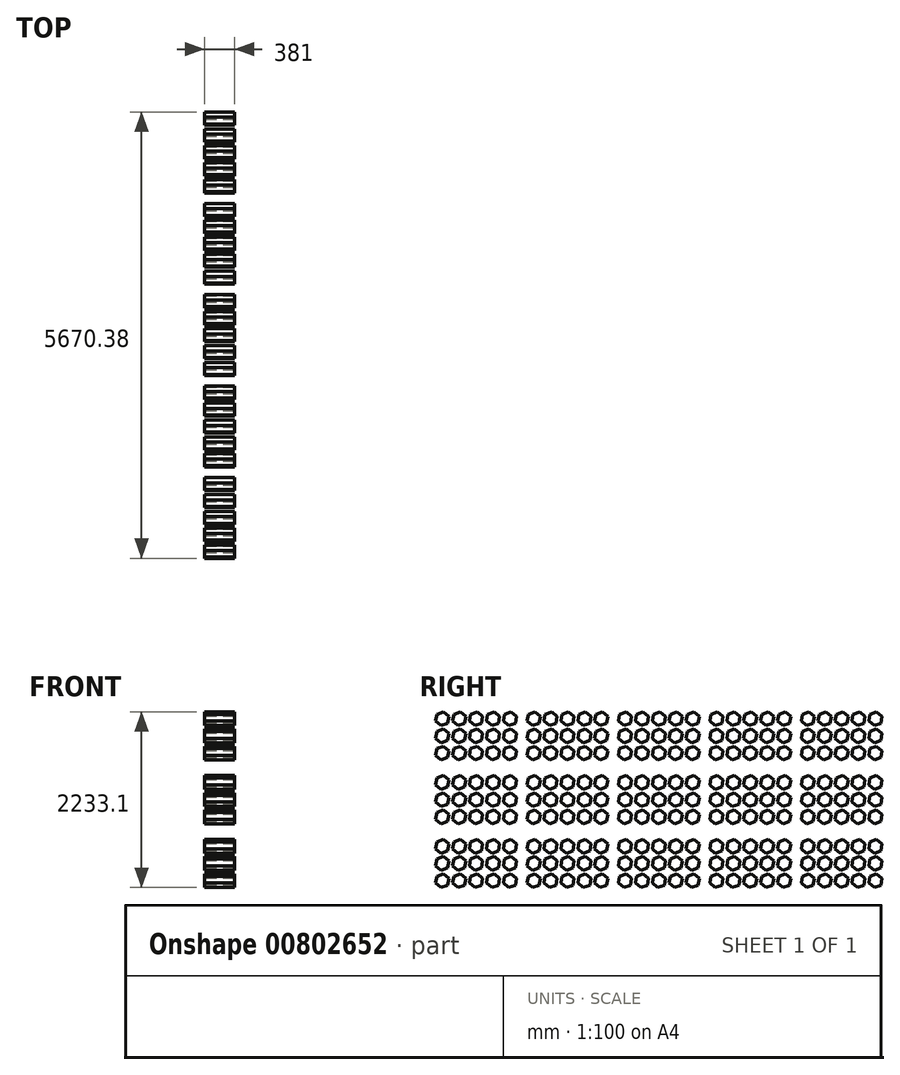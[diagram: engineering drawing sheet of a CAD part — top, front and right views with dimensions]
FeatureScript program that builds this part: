
annotation { "Feature Type Name" : "Feature", "Feature Type Description" : "" }
export const myFeature = defineFeature(function(context is Context, id is Id, definition is map)
    precondition{}
    {
        {
            var Q0;
            Q0=qCreatedBy(makeId("Right.planeOp"),FACE);
            var sketch = newSketch(context, id + "F0", { "sketchPlane" : qUnion([Q0])});
            skCircle(sketch, "E0.cCircle", {"center": v(0, 0) * mm, "radius": 77.26 * mm, "construction": true});
            skLineSegment(sketch, "E0.0", {"start": v(68.3, -57.4) * mm, "end": v(-15.56, -87.85) * mm});
            skLineSegment(sketch, "E0.1", {"start": v(-15.56, -87.85) * mm, "end": v(-83.86, -30.45) * mm});
            skLineSegment(sketch, "E0.2", {"start": v(-83.86, -30.45) * mm, "end": v(-68.3, 57.4) * mm});
            skLineSegment(sketch, "E0.3", {"start": v(-68.3, 57.4) * mm, "end": v(15.56, 87.85) * mm});
            skLineSegment(sketch, "E0.4", {"start": v(15.56, 87.85) * mm, "end": v(83.86, 30.45) * mm});
            skLineSegment(sketch, "E0.5", {"start": v(83.86, 30.45) * mm, "end": v(68.3, -57.4) * mm});
            skPoint(sketch, "E0.0.midPoint", {"position": v(26.37, -72.63) * mm});
            skCircle(sketch, "E1.0.1.0", {"center": v(0, 218.44) * mm, "radius": 77.26 * mm, "construction": true});
            skLineSegment(sketch, "E1.0.1.1", {"start": v(68.3, 161.04) * mm, "end": v(-15.56, 130.59) * mm});
            skLineSegment(sketch, "E1.0.1.2", {"start": v(-15.56, 130.59) * mm, "end": v(-83.86, 188) * mm});
            skLineSegment(sketch, "E1.0.1.3", {"start": v(-83.86, 188) * mm, "end": v(-68.3, 275.84) * mm});
            skLineSegment(sketch, "E1.0.1.4", {"start": v(-68.3, 275.84) * mm, "end": v(15.56, 306.3) * mm});
            skLineSegment(sketch, "E1.0.1.5", {"start": v(15.56, 306.3) * mm, "end": v(83.86, 248.89) * mm});
            skLineSegment(sketch, "E1.0.1.6", {"start": v(83.86, 248.89) * mm, "end": v(68.3, 161.04) * mm});
            skPoint(sketch, "E1.0.1.7", {"position": v(26.37, 145.81) * mm});
            skCircle(sketch, "E1.0.2.0", {"center": v(0, 436.88) * mm, "radius": 77.26 * mm, "construction": true});
            skLineSegment(sketch, "E1.0.2.1", {"start": v(68.3, 379.48) * mm, "end": v(-15.56, 349.03) * mm});
            skLineSegment(sketch, "E1.0.2.2", {"start": v(-15.56, 349.03) * mm, "end": v(-83.86, 406.43) * mm});
            skLineSegment(sketch, "E1.0.2.3", {"start": v(-83.86, 406.43) * mm, "end": v(-68.3, 494.28) * mm});
            skLineSegment(sketch, "E1.0.2.4", {"start": v(-68.3, 494.28) * mm, "end": v(15.56, 524.73) * mm});
            skLineSegment(sketch, "E1.0.2.5", {"start": v(15.56, 524.73) * mm, "end": v(83.86, 467.33) * mm});
            skLineSegment(sketch, "E1.0.2.6", {"start": v(83.86, 467.33) * mm, "end": v(68.3, 379.48) * mm});
            skPoint(sketch, "E1.0.2.7", {"position": v(26.37, 364.25) * mm});
            skCircle(sketch, "E1.1.0.0", {"center": v(214.88, 0) * mm, "radius": 77.26 * mm, "construction": true});
            skLineSegment(sketch, "E1.1.0.1", {"start": v(283.18, -57.4) * mm, "end": v(199.32, -87.85) * mm});
            skLineSegment(sketch, "E1.1.0.2", {"start": v(199.32, -87.85) * mm, "end": v(131.02, -30.45) * mm});
            skLineSegment(sketch, "E1.1.0.3", {"start": v(131.02, -30.45) * mm, "end": v(146.58, 57.4) * mm});
            skLineSegment(sketch, "E1.1.0.4", {"start": v(146.58, 57.4) * mm, "end": v(230.44, 87.85) * mm});
            skLineSegment(sketch, "E1.1.0.5", {"start": v(230.44, 87.85) * mm, "end": v(298.74, 30.45) * mm});
            skLineSegment(sketch, "E1.1.0.6", {"start": v(298.74, 30.45) * mm, "end": v(283.18, -57.4) * mm});
            skPoint(sketch, "E1.1.0.7", {"position": v(241.25, -72.63) * mm});
            skCircle(sketch, "E1.1.1.0", {"center": v(214.88, 218.44) * mm, "radius": 77.26 * mm, "construction": true});
            skLineSegment(sketch, "E1.1.1.1", {"start": v(283.18, 161.04) * mm, "end": v(199.32, 130.59) * mm});
            skLineSegment(sketch, "E1.1.1.2", {"start": v(199.32, 130.59) * mm, "end": v(131.02, 188) * mm});
            skLineSegment(sketch, "E1.1.1.3", {"start": v(131.02, 188) * mm, "end": v(146.58, 275.84) * mm});
            skLineSegment(sketch, "E1.1.1.4", {"start": v(146.58, 275.84) * mm, "end": v(230.44, 306.3) * mm});
            skLineSegment(sketch, "E1.1.1.5", {"start": v(230.44, 306.3) * mm, "end": v(298.74, 248.89) * mm});
            skLineSegment(sketch, "E1.1.1.6", {"start": v(298.74, 248.89) * mm, "end": v(283.18, 161.04) * mm});
            skPoint(sketch, "E1.1.1.7", {"position": v(241.25, 145.81) * mm});
            skCircle(sketch, "E1.1.2.0", {"center": v(214.88, 436.88) * mm, "radius": 77.26 * mm, "construction": true});
            skLineSegment(sketch, "E1.1.2.1", {"start": v(283.18, 379.48) * mm, "end": v(199.32, 349.03) * mm});
            skLineSegment(sketch, "E1.1.2.2", {"start": v(199.32, 349.03) * mm, "end": v(131.02, 406.43) * mm});
            skLineSegment(sketch, "E1.1.2.3", {"start": v(131.02, 406.43) * mm, "end": v(146.58, 494.28) * mm});
            skLineSegment(sketch, "E1.1.2.4", {"start": v(146.58, 494.28) * mm, "end": v(230.44, 524.73) * mm});
            skLineSegment(sketch, "E1.1.2.5", {"start": v(230.44, 524.73) * mm, "end": v(298.74, 467.33) * mm});
            skLineSegment(sketch, "E1.1.2.6", {"start": v(298.74, 467.33) * mm, "end": v(283.18, 379.48) * mm});
            skPoint(sketch, "E1.1.2.7", {"position": v(241.25, 364.25) * mm});
            skCircle(sketch, "E1.2.0.0", {"center": v(429.77, 0) * mm, "radius": 77.26 * mm, "construction": true});
            skLineSegment(sketch, "E1.2.0.1", {"start": v(498.07, -57.4) * mm, "end": v(414.2, -87.85) * mm});
            skLineSegment(sketch, "E1.2.0.2", {"start": v(414.2, -87.85) * mm, "end": v(345.9, -30.45) * mm});
            skLineSegment(sketch, "E1.2.0.3", {"start": v(345.9, -30.45) * mm, "end": v(361.47, 57.4) * mm});
            skLineSegment(sketch, "E1.2.0.4", {"start": v(361.47, 57.4) * mm, "end": v(445.33, 87.85) * mm});
            skLineSegment(sketch, "E1.2.0.5", {"start": v(445.33, 87.85) * mm, "end": v(513.63, 30.45) * mm});
            skLineSegment(sketch, "E1.2.0.6", {"start": v(513.63, 30.45) * mm, "end": v(498.07, -57.4) * mm});
            skPoint(sketch, "E1.2.0.7", {"position": v(456.14, -72.63) * mm});
            skCircle(sketch, "E1.2.1.0", {"center": v(429.77, 218.44) * mm, "radius": 77.26 * mm, "construction": true});
            skLineSegment(sketch, "E1.2.1.1", {"start": v(498.07, 161.04) * mm, "end": v(414.2, 130.59) * mm});
            skLineSegment(sketch, "E1.2.1.2", {"start": v(414.2, 130.59) * mm, "end": v(345.9, 188) * mm});
            skLineSegment(sketch, "E1.2.1.3", {"start": v(345.9, 188) * mm, "end": v(361.47, 275.84) * mm});
            skLineSegment(sketch, "E1.2.1.4", {"start": v(361.47, 275.84) * mm, "end": v(445.33, 306.3) * mm});
            skLineSegment(sketch, "E1.2.1.5", {"start": v(445.33, 306.3) * mm, "end": v(513.63, 248.89) * mm});
            skLineSegment(sketch, "E1.2.1.6", {"start": v(513.63, 248.89) * mm, "end": v(498.07, 161.04) * mm});
            skPoint(sketch, "E1.2.1.7", {"position": v(456.14, 145.81) * mm});
            skCircle(sketch, "E1.2.2.0", {"center": v(429.77, 436.88) * mm, "radius": 77.26 * mm, "construction": true});
            skLineSegment(sketch, "E1.2.2.1", {"start": v(498.07, 379.48) * mm, "end": v(414.2, 349.03) * mm});
            skLineSegment(sketch, "E1.2.2.2", {"start": v(414.2, 349.03) * mm, "end": v(345.9, 406.43) * mm});
            skLineSegment(sketch, "E1.2.2.3", {"start": v(345.9, 406.43) * mm, "end": v(361.47, 494.28) * mm});
            skLineSegment(sketch, "E1.2.2.4", {"start": v(361.47, 494.28) * mm, "end": v(445.33, 524.73) * mm});
            skLineSegment(sketch, "E1.2.2.5", {"start": v(445.33, 524.73) * mm, "end": v(513.63, 467.33) * mm});
            skLineSegment(sketch, "E1.2.2.6", {"start": v(513.63, 467.33) * mm, "end": v(498.07, 379.48) * mm});
            skPoint(sketch, "E1.2.2.7", {"position": v(456.14, 364.25) * mm});
            skCircle(sketch, "E1.3.0.0", {"center": v(644.65, 0) * mm, "radius": 77.26 * mm, "construction": true});
            skLineSegment(sketch, "E1.3.0.1", {"start": v(712.95, -57.4) * mm, "end": v(629.1, -87.85) * mm});
            skLineSegment(sketch, "E1.3.0.2", {"start": v(629.1, -87.85) * mm, "end": v(560.8, -30.45) * mm});
            skLineSegment(sketch, "E1.3.0.3", {"start": v(560.8, -30.45) * mm, "end": v(576.35, 57.4) * mm});
            skLineSegment(sketch, "E1.3.0.4", {"start": v(576.35, 57.4) * mm, "end": v(660.21, 87.85) * mm});
            skLineSegment(sketch, "E1.3.0.5", {"start": v(660.21, 87.85) * mm, "end": v(728.51, 30.45) * mm});
            skLineSegment(sketch, "E1.3.0.6", {"start": v(728.51, 30.45) * mm, "end": v(712.95, -57.4) * mm});
            skPoint(sketch, "E1.3.0.7", {"position": v(671.02, -72.63) * mm});
            skCircle(sketch, "E1.3.1.0", {"center": v(644.65, 218.44) * mm, "radius": 77.26 * mm, "construction": true});
            skLineSegment(sketch, "E1.3.1.1", {"start": v(712.95, 161.04) * mm, "end": v(629.1, 130.59) * mm});
            skLineSegment(sketch, "E1.3.1.2", {"start": v(629.1, 130.59) * mm, "end": v(560.8, 188) * mm});
            skLineSegment(sketch, "E1.3.1.3", {"start": v(560.8, 188) * mm, "end": v(576.35, 275.84) * mm});
            skLineSegment(sketch, "E1.3.1.4", {"start": v(576.35, 275.84) * mm, "end": v(660.21, 306.3) * mm});
            skLineSegment(sketch, "E1.3.1.5", {"start": v(660.21, 306.3) * mm, "end": v(728.51, 248.89) * mm});
            skLineSegment(sketch, "E1.3.1.6", {"start": v(728.51, 248.89) * mm, "end": v(712.95, 161.04) * mm});
            skPoint(sketch, "E1.3.1.7", {"position": v(671.02, 145.81) * mm});
            skCircle(sketch, "E1.3.2.0", {"center": v(644.65, 436.88) * mm, "radius": 77.26 * mm, "construction": true});
            skLineSegment(sketch, "E1.3.2.1", {"start": v(712.95, 379.48) * mm, "end": v(629.1, 349.03) * mm});
            skLineSegment(sketch, "E1.3.2.2", {"start": v(629.1, 349.03) * mm, "end": v(560.8, 406.43) * mm});
            skLineSegment(sketch, "E1.3.2.3", {"start": v(560.8, 406.43) * mm, "end": v(576.35, 494.28) * mm});
            skLineSegment(sketch, "E1.3.2.4", {"start": v(576.35, 494.28) * mm, "end": v(660.21, 524.73) * mm});
            skLineSegment(sketch, "E1.3.2.5", {"start": v(660.21, 524.73) * mm, "end": v(728.51, 467.33) * mm});
            skLineSegment(sketch, "E1.3.2.6", {"start": v(728.51, 467.33) * mm, "end": v(712.95, 379.48) * mm});
            skPoint(sketch, "E1.3.2.7", {"position": v(671.02, 364.25) * mm});
            skCircle(sketch, "E1.4.0.0", {"center": v(859.54, 0) * mm, "radius": 77.26 * mm, "construction": true});
            skLineSegment(sketch, "E1.4.0.1", {"start": v(927.84, -57.4) * mm, "end": v(843.98, -87.85) * mm});
            skLineSegment(sketch, "E1.4.0.2", {"start": v(843.98, -87.85) * mm, "end": v(775.68, -30.45) * mm});
            skLineSegment(sketch, "E1.4.0.3", {"start": v(775.68, -30.45) * mm, "end": v(791.24, 57.4) * mm});
            skLineSegment(sketch, "E1.4.0.4", {"start": v(791.24, 57.4) * mm, "end": v(875.1, 87.85) * mm});
            skLineSegment(sketch, "E1.4.0.5", {"start": v(875.1, 87.85) * mm, "end": v(943.4, 30.45) * mm});
            skLineSegment(sketch, "E1.4.0.6", {"start": v(943.4, 30.45) * mm, "end": v(927.84, -57.4) * mm});
            skPoint(sketch, "E1.4.0.7", {"position": v(885.9, -72.63) * mm});
            skCircle(sketch, "E1.4.1.0", {"center": v(859.54, 218.44) * mm, "radius": 77.26 * mm, "construction": true});
            skLineSegment(sketch, "E1.4.1.1", {"start": v(927.84, 161.04) * mm, "end": v(843.98, 130.59) * mm});
            skLineSegment(sketch, "E1.4.1.2", {"start": v(843.98, 130.59) * mm, "end": v(775.68, 188) * mm});
            skLineSegment(sketch, "E1.4.1.3", {"start": v(775.68, 188) * mm, "end": v(791.24, 275.84) * mm});
            skLineSegment(sketch, "E1.4.1.4", {"start": v(791.24, 275.84) * mm, "end": v(875.1, 306.3) * mm});
            skLineSegment(sketch, "E1.4.1.5", {"start": v(875.1, 306.3) * mm, "end": v(943.4, 248.89) * mm});
            skLineSegment(sketch, "E1.4.1.6", {"start": v(943.4, 248.89) * mm, "end": v(927.84, 161.04) * mm});
            skPoint(sketch, "E1.4.1.7", {"position": v(885.9, 145.81) * mm});
            skCircle(sketch, "E1.4.2.0", {"center": v(859.54, 436.88) * mm, "radius": 77.26 * mm, "construction": true});
            skLineSegment(sketch, "E1.4.2.1", {"start": v(927.84, 379.48) * mm, "end": v(843.98, 349.03) * mm});
            skLineSegment(sketch, "E1.4.2.2", {"start": v(843.98, 349.03) * mm, "end": v(775.68, 406.43) * mm});
            skLineSegment(sketch, "E1.4.2.3", {"start": v(775.68, 406.43) * mm, "end": v(791.24, 494.28) * mm});
            skLineSegment(sketch, "E1.4.2.4", {"start": v(791.24, 494.28) * mm, "end": v(875.1, 524.73) * mm});
            skLineSegment(sketch, "E1.4.2.5", {"start": v(875.1, 524.73) * mm, "end": v(943.4, 467.33) * mm});
            skLineSegment(sketch, "E1.4.2.6", {"start": v(943.4, 467.33) * mm, "end": v(927.84, 379.48) * mm});
            skPoint(sketch, "E1.4.2.7", {"position": v(885.9, 364.25) * mm});
            skLineSegment(sketch, "E1.direction1", {"start": v(-83.86, -30.45) * mm, "end": v(131.02, -30.45) * mm, "construction": true});
            skLineSegment(sketch, "E1.direction2", {"start": v(-83.86, -30.45) * mm, "end": v(-83.86, 188) * mm, "construction": true});
            skLineSegment(sketch, "E2.0.1.0", {"start": v(943.4, 840.7) * mm, "end": v(927.84, 752.86) * mm});
            skLineSegment(sketch, "E2.0.1.1", {"start": v(-83.86, 779.81) * mm, "end": v(-83.86, 998.25) * mm, "construction": true});
            skLineSegment(sketch, "E2.0.1.2", {"start": v(230.44, 898.11) * mm, "end": v(298.74, 840.7) * mm});
            skCircle(sketch, "E2.0.1.3", {"center": v(429.77, 810.26) * mm, "radius": 77.26 * mm, "construction": true});
            skLineSegment(sketch, "E2.0.1.4", {"start": v(414.2, 1159.29) * mm, "end": v(345.9, 1216.7) * mm});
            skPoint(sketch, "E2.0.1.5", {"position": v(885.9, 956.07) * mm});
            skPoint(sketch, "E2.0.1.6", {"position": v(241.25, 1174.51) * mm});
            skLineSegment(sketch, "E2.0.1.7", {"start": v(15.56, 1335) * mm, "end": v(83.86, 1277.59) * mm});
            skLineSegment(sketch, "E2.0.1.8", {"start": v(576.35, 867.66) * mm, "end": v(660.21, 898.11) * mm});
            skLineSegment(sketch, "E2.0.1.9", {"start": v(414.2, 940.85) * mm, "end": v(345.9, 998.25) * mm});
            skCircle(sketch, "E2.0.1.10", {"center": v(214.88, 1247.14) * mm, "radius": 77.26 * mm, "construction": true});
            skPoint(sketch, "E2.0.1.11", {"position": v(26.37, 1174.51) * mm});
            skPoint(sketch, "E2.0.1.12", {"position": v(671.02, 956.07) * mm});
            skCircle(sketch, "E2.0.1.13", {"center": v(859.54, 1028.7) * mm, "radius": 77.26 * mm, "construction": true});
            skLineSegment(sketch, "E2.0.1.14", {"start": v(83.86, 1277.59) * mm, "end": v(68.3, 1189.74) * mm});
            skCircle(sketch, "E2.0.1.15", {"center": v(644.65, 1247.14) * mm, "radius": 77.26 * mm, "construction": true});
            skCircle(sketch, "E2.0.1.16", {"center": v(859.54, 810.26) * mm, "radius": 77.26 * mm, "construction": true});
            skLineSegment(sketch, "E2.0.1.17", {"start": v(445.33, 1335) * mm, "end": v(513.63, 1277.59) * mm});
            skLineSegment(sketch, "E2.0.1.18", {"start": v(345.9, 779.81) * mm, "end": v(361.47, 867.66) * mm});
            skLineSegment(sketch, "E2.0.1.19", {"start": v(345.9, 998.25) * mm, "end": v(361.47, 1086.1) * mm});
            skPoint(sketch, "E2.0.1.20", {"position": v(671.02, 737.63) * mm});
            skPoint(sketch, "E2.0.1.21", {"position": v(26.37, 956.07) * mm});
            skPoint(sketch, "E2.0.1.22", {"position": v(456.14, 737.63) * mm});
            skPoint(sketch, "E2.0.1.23", {"position": v(885.9, 1174.51) * mm});
            skLineSegment(sketch, "E2.0.1.24", {"start": v(361.47, 1304.54) * mm, "end": v(445.33, 1335) * mm});
            skLineSegment(sketch, "E2.0.1.25", {"start": v(414.2, 722.4) * mm, "end": v(345.9, 779.81) * mm});
            skCircle(sketch, "E2.0.1.26", {"center": v(214.88, 1028.7) * mm, "radius": 77.26 * mm, "construction": true});
            skCircle(sketch, "E2.0.1.27", {"center": v(214.88, 810.26) * mm, "radius": 77.26 * mm, "construction": true});
            skLineSegment(sketch, "E2.0.1.28", {"start": v(513.63, 1277.59) * mm, "end": v(498.07, 1189.74) * mm});
            skLineSegment(sketch, "E2.0.1.29", {"start": v(361.47, 1086.1) * mm, "end": v(445.33, 1116.55) * mm});
            skLineSegment(sketch, "E2.0.1.30", {"start": v(361.47, 867.66) * mm, "end": v(445.33, 898.11) * mm});
            skLineSegment(sketch, "E2.0.1.31", {"start": v(199.32, 940.85) * mm, "end": v(131.02, 998.25) * mm});
            skLineSegment(sketch, "E2.0.1.32", {"start": v(775.68, 998.25) * mm, "end": v(791.24, 1086.1) * mm});
            skPoint(sketch, "E2.0.1.33", {"position": v(241.25, 737.63) * mm});
            skPoint(sketch, "E2.0.1.34", {"position": v(671.02, 1174.51) * mm});
            skLineSegment(sketch, "E2.0.1.35", {"start": v(629.1, 1159.29) * mm, "end": v(560.8, 1216.7) * mm});
            skCircle(sketch, "E2.0.1.36", {"center": v(644.65, 1028.7) * mm, "radius": 77.26 * mm, "construction": true});
            skCircle(sketch, "E2.0.1.37", {"center": v(644.65, 810.26) * mm, "radius": 77.26 * mm, "construction": true});
            skLineSegment(sketch, "E2.0.1.38", {"start": v(445.33, 898.11) * mm, "end": v(513.63, 840.7) * mm});
            skLineSegment(sketch, "E2.0.1.39", {"start": v(791.24, 1304.54) * mm, "end": v(875.1, 1335) * mm});
            skLineSegment(sketch, "E2.0.1.40", {"start": v(791.24, 1086.1) * mm, "end": v(875.1, 1116.55) * mm});
            skLineSegment(sketch, "E2.0.1.41", {"start": v(83.86, 1059.15) * mm, "end": v(68.3, 971.3) * mm});
            skCircle(sketch, "E2.0.1.42", {"center": v(0, 1247.14) * mm, "radius": 77.26 * mm, "construction": true});
            skCircle(sketch, "E2.0.1.43", {"center": v(0, 810.26) * mm, "radius": 77.26 * mm, "construction": true});
            skLineSegment(sketch, "E2.0.1.44", {"start": v(-15.56, 722.4) * mm, "end": v(-83.86, 779.81) * mm});
            skLineSegment(sketch, "E2.0.1.45", {"start": v(-68.3, 867.66) * mm, "end": v(15.56, 898.11) * mm});
            skCircle(sketch, "E2.0.1.46", {"center": v(0, 1028.7) * mm, "radius": 77.26 * mm, "construction": true});
            skLineSegment(sketch, "E2.0.1.47", {"start": v(-15.56, 940.85) * mm, "end": v(-83.86, 998.25) * mm});
            skLineSegment(sketch, "E2.0.1.48", {"start": v(-83.86, 998.25) * mm, "end": v(-68.3, 1086.1) * mm});
            skLineSegment(sketch, "E2.0.1.49", {"start": v(-68.3, 1086.1) * mm, "end": v(15.56, 1116.55) * mm});
            skLineSegment(sketch, "E2.0.1.50", {"start": v(15.56, 1116.55) * mm, "end": v(83.86, 1059.15) * mm});
            skPoint(sketch, "E2.0.1.51", {"position": v(456.14, 956.07) * mm});
            skLineSegment(sketch, "E2.0.1.52", {"start": v(513.63, 1059.15) * mm, "end": v(498.07, 971.3) * mm});
            skLineSegment(sketch, "E2.0.1.53", {"start": v(146.58, 1304.54) * mm, "end": v(230.44, 1335) * mm});
            skLineSegment(sketch, "E2.0.1.54", {"start": v(875.1, 1335) * mm, "end": v(943.4, 1277.59) * mm});
            skLineSegment(sketch, "E2.0.1.55", {"start": v(-15.56, 1159.29) * mm, "end": v(-83.86, 1216.7) * mm});
            skLineSegment(sketch, "E2.0.1.56", {"start": v(513.63, 840.7) * mm, "end": v(498.07, 752.86) * mm});
            skCircle(sketch, "E2.0.1.57", {"center": v(429.77, 1247.14) * mm, "radius": 77.26 * mm, "construction": true});
            skLineSegment(sketch, "E2.0.1.58", {"start": v(943.4, 1277.59) * mm, "end": v(927.84, 1189.74) * mm});
            skLineSegment(sketch, "E2.0.1.59", {"start": v(629.1, 940.85) * mm, "end": v(560.8, 998.25) * mm});
            skPoint(sketch, "E2.0.1.60", {"position": v(241.25, 956.07) * mm});
            skPoint(sketch, "E2.0.1.61", {"position": v(885.9, 737.63) * mm});
            skLineSegment(sketch, "E2.0.1.62", {"start": v(576.35, 1304.54) * mm, "end": v(660.21, 1335) * mm});
            skCircle(sketch, "E2.0.1.63", {"center": v(429.77, 1028.7) * mm, "radius": 77.26 * mm, "construction": true});
            skLineSegment(sketch, "E2.0.1.64", {"start": v(943.4, 1059.15) * mm, "end": v(927.84, 971.3) * mm});
            skLineSegment(sketch, "E2.0.1.65", {"start": v(146.58, 867.66) * mm, "end": v(230.44, 898.11) * mm});
            skLineSegment(sketch, "E2.0.1.66", {"start": v(-83.86, 779.81) * mm, "end": v(131.02, 779.81) * mm, "construction": true});
            skLineSegment(sketch, "E2.0.1.67", {"start": v(875.1, 898.11) * mm, "end": v(943.4, 840.7) * mm});
            skLineSegment(sketch, "E2.0.1.68", {"start": v(-68.3, 1304.54) * mm, "end": v(15.56, 1335) * mm});
            skLineSegment(sketch, "E2.0.1.69", {"start": v(660.21, 1335) * mm, "end": v(728.51, 1277.59) * mm});
            skCircle(sketch, "E2.0.1.70", {"center": v(859.54, 1247.14) * mm, "radius": 77.26 * mm, "construction": true});
            skPoint(sketch, "E2.0.1.71", {"position": v(456.14, 1174.51) * mm});
            skPoint(sketch, "E2.0.1.72", {"position": v(26.37, 737.63) * mm});
            skLineSegment(sketch, "E2.0.1.73", {"start": v(576.35, 1086.1) * mm, "end": v(660.21, 1116.55) * mm});
            skLineSegment(sketch, "E2.0.1.74", {"start": v(728.51, 1277.59) * mm, "end": v(712.95, 1189.74) * mm});
            skLineSegment(sketch, "E2.0.1.75", {"start": v(927.84, 1189.74) * mm, "end": v(843.98, 1159.29) * mm});
            skLineSegment(sketch, "E2.0.1.76", {"start": v(345.9, 1216.7) * mm, "end": v(361.47, 1304.54) * mm});
            skLineSegment(sketch, "E2.0.1.77", {"start": v(498.07, 752.86) * mm, "end": v(414.2, 722.4) * mm});
            skLineSegment(sketch, "E2.0.1.78", {"start": v(298.74, 840.7) * mm, "end": v(283.18, 752.86) * mm});
            skLineSegment(sketch, "E2.0.1.79", {"start": v(660.21, 1116.55) * mm, "end": v(728.51, 1059.15) * mm});
            skLineSegment(sketch, "E2.0.1.80", {"start": v(660.21, 898.11) * mm, "end": v(728.51, 840.7) * mm});
            skLineSegment(sketch, "E2.0.1.81", {"start": v(283.18, 1189.74) * mm, "end": v(199.32, 1159.29) * mm});
            skLineSegment(sketch, "E2.0.1.82", {"start": v(283.18, 971.3) * mm, "end": v(199.32, 940.85) * mm});
            skLineSegment(sketch, "E2.0.1.83", {"start": v(843.98, 1159.29) * mm, "end": v(775.68, 1216.7) * mm});
            skLineSegment(sketch, "E2.0.1.84", {"start": v(843.98, 940.85) * mm, "end": v(775.68, 998.25) * mm});
            skLineSegment(sketch, "E2.0.1.85", {"start": v(927.84, 971.3) * mm, "end": v(843.98, 940.85) * mm});
            skLineSegment(sketch, "E2.0.1.86", {"start": v(728.51, 1059.15) * mm, "end": v(712.95, 971.3) * mm});
            skLineSegment(sketch, "E2.0.1.87", {"start": v(712.95, 1189.74) * mm, "end": v(629.1, 1159.29) * mm});
            skLineSegment(sketch, "E2.0.1.88", {"start": v(927.84, 752.86) * mm, "end": v(843.98, 722.4) * mm});
            skLineSegment(sketch, "E2.0.1.89", {"start": v(728.51, 840.7) * mm, "end": v(712.95, 752.86) * mm});
            skLineSegment(sketch, "E2.0.1.90", {"start": v(199.32, 1159.29) * mm, "end": v(131.02, 1216.7) * mm});
            skLineSegment(sketch, "E2.0.1.91", {"start": v(775.68, 1216.7) * mm, "end": v(791.24, 1304.54) * mm});
            skLineSegment(sketch, "E2.0.1.92", {"start": v(283.18, 752.86) * mm, "end": v(199.32, 722.4) * mm});
            skLineSegment(sketch, "E2.0.1.93", {"start": v(843.98, 722.4) * mm, "end": v(775.68, 779.81) * mm});
            skLineSegment(sketch, "E2.0.1.94", {"start": v(445.33, 1116.55) * mm, "end": v(513.63, 1059.15) * mm});
            skLineSegment(sketch, "E2.0.1.95", {"start": v(131.02, 1216.7) * mm, "end": v(146.58, 1304.54) * mm});
            skLineSegment(sketch, "E2.0.1.96", {"start": v(131.02, 998.25) * mm, "end": v(146.58, 1086.1) * mm});
            skLineSegment(sketch, "E2.0.1.97", {"start": v(68.3, 1189.74) * mm, "end": v(-15.56, 1159.29) * mm});
            skLineSegment(sketch, "E2.0.1.98", {"start": v(68.3, 752.86) * mm, "end": v(-15.56, 722.4) * mm});
            skLineSegment(sketch, "E2.0.1.99", {"start": v(-83.86, 779.81) * mm, "end": v(-68.3, 867.66) * mm});
            skLineSegment(sketch, "E2.0.1.100", {"start": v(15.56, 898.11) * mm, "end": v(83.86, 840.7) * mm});
            skLineSegment(sketch, "E2.0.1.101", {"start": v(83.86, 840.7) * mm, "end": v(68.3, 752.86) * mm});
            skLineSegment(sketch, "E2.0.1.102", {"start": v(68.3, 971.3) * mm, "end": v(-15.56, 940.85) * mm});
            skLineSegment(sketch, "E2.0.1.103", {"start": v(875.1, 1116.55) * mm, "end": v(943.4, 1059.15) * mm});
            skLineSegment(sketch, "E2.0.1.104", {"start": v(199.32, 722.4) * mm, "end": v(131.02, 779.81) * mm});
            skLineSegment(sketch, "E2.0.1.105", {"start": v(775.68, 779.81) * mm, "end": v(791.24, 867.66) * mm});
            skLineSegment(sketch, "E2.0.1.106", {"start": v(712.95, 971.3) * mm, "end": v(629.1, 940.85) * mm});
            skLineSegment(sketch, "E2.0.1.107", {"start": v(560.8, 1216.7) * mm, "end": v(576.35, 1304.54) * mm});
            skLineSegment(sketch, "E2.0.1.108", {"start": v(712.95, 752.86) * mm, "end": v(629.1, 722.4) * mm});
            skLineSegment(sketch, "E2.0.1.109", {"start": v(146.58, 1086.1) * mm, "end": v(230.44, 1116.55) * mm});
            skLineSegment(sketch, "E2.0.1.110", {"start": v(230.44, 1335) * mm, "end": v(298.74, 1277.59) * mm});
            skLineSegment(sketch, "E2.0.1.111", {"start": v(131.02, 779.81) * mm, "end": v(146.58, 867.66) * mm});
            skLineSegment(sketch, "E2.0.1.112", {"start": v(791.24, 867.66) * mm, "end": v(875.1, 898.11) * mm});
            skLineSegment(sketch, "E2.0.1.113", {"start": v(-83.86, 1216.7) * mm, "end": v(-68.3, 1304.54) * mm});
            skLineSegment(sketch, "E2.0.1.114", {"start": v(629.1, 722.4) * mm, "end": v(560.8, 779.81) * mm});
            skLineSegment(sketch, "E2.0.1.115", {"start": v(230.44, 1116.55) * mm, "end": v(298.74, 1059.15) * mm});
            skLineSegment(sketch, "E2.0.1.116", {"start": v(498.07, 1189.74) * mm, "end": v(414.2, 1159.29) * mm});
            skLineSegment(sketch, "E2.0.1.117", {"start": v(298.74, 1277.59) * mm, "end": v(283.18, 1189.74) * mm});
            skLineSegment(sketch, "E2.0.1.118", {"start": v(560.8, 998.25) * mm, "end": v(576.35, 1086.1) * mm});
            skLineSegment(sketch, "E2.0.1.119", {"start": v(560.8, 779.81) * mm, "end": v(576.35, 867.66) * mm});
            skLineSegment(sketch, "E2.0.1.120", {"start": v(498.07, 971.3) * mm, "end": v(414.2, 940.85) * mm});
            skLineSegment(sketch, "E2.0.1.121", {"start": v(298.74, 1059.15) * mm, "end": v(283.18, 971.3) * mm});
            skLineSegment(sketch, "E2.0.2.0", {"start": v(943.4, 1650.97) * mm, "end": v(927.84, 1563.12) * mm});
            skLineSegment(sketch, "E2.0.2.1", {"start": v(-83.86, 1590.07) * mm, "end": v(-83.86, 1808.51) * mm, "construction": true});
            skLineSegment(sketch, "E2.0.2.2", {"start": v(230.44, 1708.37) * mm, "end": v(298.74, 1650.97) * mm});
            skCircle(sketch, "E2.0.2.3", {"center": v(429.77, 1620.52) * mm, "radius": 77.26 * mm, "construction": true});
            skLineSegment(sketch, "E2.0.2.4", {"start": v(414.2, 1969.55) * mm, "end": v(345.9, 2026.95) * mm});
            skPoint(sketch, "E2.0.2.5", {"position": v(885.9, 1766.33) * mm});
            skPoint(sketch, "E2.0.2.6", {"position": v(241.25, 1984.77) * mm});
            skLineSegment(sketch, "E2.0.2.7", {"start": v(15.56, 2145.25) * mm, "end": v(83.86, 2087.85) * mm});
            skLineSegment(sketch, "E2.0.2.8", {"start": v(576.35, 1677.92) * mm, "end": v(660.21, 1708.37) * mm});
            skLineSegment(sketch, "E2.0.2.9", {"start": v(414.2, 1751.1) * mm, "end": v(345.9, 1808.51) * mm});
            skCircle(sketch, "E2.0.2.10", {"center": v(214.88, 2057.4) * mm, "radius": 77.26 * mm, "construction": true});
            skPoint(sketch, "E2.0.2.11", {"position": v(26.37, 1984.77) * mm});
            skPoint(sketch, "E2.0.2.12", {"position": v(671.02, 1766.33) * mm});
            skCircle(sketch, "E2.0.2.13", {"center": v(859.54, 1838.96) * mm, "radius": 77.26 * mm, "construction": true});
            skLineSegment(sketch, "E2.0.2.14", {"start": v(83.86, 2087.85) * mm, "end": v(68.3, 2000) * mm});
            skCircle(sketch, "E2.0.2.15", {"center": v(644.65, 2057.4) * mm, "radius": 77.26 * mm, "construction": true});
            skCircle(sketch, "E2.0.2.16", {"center": v(859.54, 1620.52) * mm, "radius": 77.26 * mm, "construction": true});
            skLineSegment(sketch, "E2.0.2.17", {"start": v(445.33, 2145.25) * mm, "end": v(513.63, 2087.85) * mm});
            skLineSegment(sketch, "E2.0.2.18", {"start": v(345.9, 1590.07) * mm, "end": v(361.47, 1677.92) * mm});
            skLineSegment(sketch, "E2.0.2.19", {"start": v(345.9, 1808.51) * mm, "end": v(361.47, 1896.36) * mm});
            skPoint(sketch, "E2.0.2.20", {"position": v(671.02, 1547.9) * mm});
            skPoint(sketch, "E2.0.2.21", {"position": v(26.37, 1766.33) * mm});
            skPoint(sketch, "E2.0.2.22", {"position": v(456.14, 1547.9) * mm});
            skPoint(sketch, "E2.0.2.23", {"position": v(885.9, 1984.77) * mm});
            skLineSegment(sketch, "E2.0.2.24", {"start": v(361.47, 2114.8) * mm, "end": v(445.33, 2145.25) * mm});
            skLineSegment(sketch, "E2.0.2.25", {"start": v(414.2, 1532.67) * mm, "end": v(345.9, 1590.07) * mm});
            skCircle(sketch, "E2.0.2.26", {"center": v(214.88, 1838.96) * mm, "radius": 77.26 * mm, "construction": true});
            skCircle(sketch, "E2.0.2.27", {"center": v(214.88, 1620.52) * mm, "radius": 77.26 * mm, "construction": true});
            skLineSegment(sketch, "E2.0.2.28", {"start": v(513.63, 2087.85) * mm, "end": v(498.07, 2000) * mm});
            skLineSegment(sketch, "E2.0.2.29", {"start": v(361.47, 1896.36) * mm, "end": v(445.33, 1926.81) * mm});
            skLineSegment(sketch, "E2.0.2.30", {"start": v(361.47, 1677.92) * mm, "end": v(445.33, 1708.37) * mm});
            skLineSegment(sketch, "E2.0.2.31", {"start": v(199.32, 1751.1) * mm, "end": v(131.02, 1808.51) * mm});
            skLineSegment(sketch, "E2.0.2.32", {"start": v(775.68, 1808.51) * mm, "end": v(791.24, 1896.36) * mm});
            skPoint(sketch, "E2.0.2.33", {"position": v(241.25, 1547.9) * mm});
            skPoint(sketch, "E2.0.2.34", {"position": v(671.02, 1984.77) * mm});
            skLineSegment(sketch, "E2.0.2.35", {"start": v(629.1, 1969.55) * mm, "end": v(560.8, 2026.95) * mm});
            skCircle(sketch, "E2.0.2.36", {"center": v(644.65, 1838.96) * mm, "radius": 77.26 * mm, "construction": true});
            skCircle(sketch, "E2.0.2.37", {"center": v(644.65, 1620.52) * mm, "radius": 77.26 * mm, "construction": true});
            skLineSegment(sketch, "E2.0.2.38", {"start": v(445.33, 1708.37) * mm, "end": v(513.63, 1650.97) * mm});
            skLineSegment(sketch, "E2.0.2.39", {"start": v(791.24, 2114.8) * mm, "end": v(875.1, 2145.25) * mm});
            skLineSegment(sketch, "E2.0.2.40", {"start": v(791.24, 1896.36) * mm, "end": v(875.1, 1926.81) * mm});
            skLineSegment(sketch, "E2.0.2.41", {"start": v(83.86, 1869.4) * mm, "end": v(68.3, 1781.56) * mm});
            skCircle(sketch, "E2.0.2.42", {"center": v(0, 2057.4) * mm, "radius": 77.26 * mm, "construction": true});
            skCircle(sketch, "E2.0.2.43", {"center": v(0, 1620.52) * mm, "radius": 77.26 * mm, "construction": true});
            skLineSegment(sketch, "E2.0.2.44", {"start": v(-15.56, 1532.67) * mm, "end": v(-83.86, 1590.07) * mm});
            skLineSegment(sketch, "E2.0.2.45", {"start": v(-68.3, 1677.92) * mm, "end": v(15.56, 1708.37) * mm});
            skCircle(sketch, "E2.0.2.46", {"center": v(0, 1838.96) * mm, "radius": 77.26 * mm, "construction": true});
            skLineSegment(sketch, "E2.0.2.47", {"start": v(-15.56, 1751.1) * mm, "end": v(-83.86, 1808.51) * mm});
            skLineSegment(sketch, "E2.0.2.48", {"start": v(-83.86, 1808.51) * mm, "end": v(-68.3, 1896.36) * mm});
            skLineSegment(sketch, "E2.0.2.49", {"start": v(-68.3, 1896.36) * mm, "end": v(15.56, 1926.81) * mm});
            skLineSegment(sketch, "E2.0.2.50", {"start": v(15.56, 1926.81) * mm, "end": v(83.86, 1869.4) * mm});
            skPoint(sketch, "E2.0.2.51", {"position": v(456.14, 1766.33) * mm});
            skLineSegment(sketch, "E2.0.2.52", {"start": v(513.63, 1869.4) * mm, "end": v(498.07, 1781.56) * mm});
            skLineSegment(sketch, "E2.0.2.53", {"start": v(146.58, 2114.8) * mm, "end": v(230.44, 2145.25) * mm});
            skLineSegment(sketch, "E2.0.2.54", {"start": v(875.1, 2145.25) * mm, "end": v(943.4, 2087.85) * mm});
            skLineSegment(sketch, "E2.0.2.55", {"start": v(-15.56, 1969.55) * mm, "end": v(-83.86, 2026.95) * mm});
            skLineSegment(sketch, "E2.0.2.56", {"start": v(513.63, 1650.97) * mm, "end": v(498.07, 1563.12) * mm});
            skCircle(sketch, "E2.0.2.57", {"center": v(429.77, 2057.4) * mm, "radius": 77.26 * mm, "construction": true});
            skLineSegment(sketch, "E2.0.2.58", {"start": v(943.4, 2087.85) * mm, "end": v(927.84, 2000) * mm});
            skLineSegment(sketch, "E2.0.2.59", {"start": v(629.1, 1751.1) * mm, "end": v(560.8, 1808.51) * mm});
            skPoint(sketch, "E2.0.2.60", {"position": v(241.25, 1766.33) * mm});
            skPoint(sketch, "E2.0.2.61", {"position": v(885.9, 1547.9) * mm});
            skLineSegment(sketch, "E2.0.2.62", {"start": v(576.35, 2114.8) * mm, "end": v(660.21, 2145.25) * mm});
            skCircle(sketch, "E2.0.2.63", {"center": v(429.77, 1838.96) * mm, "radius": 77.26 * mm, "construction": true});
            skLineSegment(sketch, "E2.0.2.64", {"start": v(943.4, 1869.4) * mm, "end": v(927.84, 1781.56) * mm});
            skLineSegment(sketch, "E2.0.2.65", {"start": v(146.58, 1677.92) * mm, "end": v(230.44, 1708.37) * mm});
            skLineSegment(sketch, "E2.0.2.66", {"start": v(-83.86, 1590.07) * mm, "end": v(131.02, 1590.07) * mm, "construction": true});
            skLineSegment(sketch, "E2.0.2.67", {"start": v(875.1, 1708.37) * mm, "end": v(943.4, 1650.97) * mm});
            skLineSegment(sketch, "E2.0.2.68", {"start": v(-68.3, 2114.8) * mm, "end": v(15.56, 2145.25) * mm});
            skLineSegment(sketch, "E2.0.2.69", {"start": v(660.21, 2145.25) * mm, "end": v(728.51, 2087.85) * mm});
            skCircle(sketch, "E2.0.2.70", {"center": v(859.54, 2057.4) * mm, "radius": 77.26 * mm, "construction": true});
            skPoint(sketch, "E2.0.2.71", {"position": v(456.14, 1984.77) * mm});
            skPoint(sketch, "E2.0.2.72", {"position": v(26.37, 1547.9) * mm});
            skLineSegment(sketch, "E2.0.2.73", {"start": v(576.35, 1896.36) * mm, "end": v(660.21, 1926.81) * mm});
            skLineSegment(sketch, "E2.0.2.74", {"start": v(728.51, 2087.85) * mm, "end": v(712.95, 2000) * mm});
            skLineSegment(sketch, "E2.0.2.75", {"start": v(927.84, 2000) * mm, "end": v(843.98, 1969.55) * mm});
            skLineSegment(sketch, "E2.0.2.76", {"start": v(345.9, 2026.95) * mm, "end": v(361.47, 2114.8) * mm});
            skLineSegment(sketch, "E2.0.2.77", {"start": v(498.07, 1563.12) * mm, "end": v(414.2, 1532.67) * mm});
            skLineSegment(sketch, "E2.0.2.78", {"start": v(298.74, 1650.97) * mm, "end": v(283.18, 1563.12) * mm});
            skLineSegment(sketch, "E2.0.2.79", {"start": v(660.21, 1926.81) * mm, "end": v(728.51, 1869.4) * mm});
            skLineSegment(sketch, "E2.0.2.80", {"start": v(660.21, 1708.37) * mm, "end": v(728.51, 1650.97) * mm});
            skLineSegment(sketch, "E2.0.2.81", {"start": v(283.18, 2000) * mm, "end": v(199.32, 1969.55) * mm});
            skLineSegment(sketch, "E2.0.2.82", {"start": v(283.18, 1781.56) * mm, "end": v(199.32, 1751.1) * mm});
            skLineSegment(sketch, "E2.0.2.83", {"start": v(843.98, 1969.55) * mm, "end": v(775.68, 2026.95) * mm});
            skLineSegment(sketch, "E2.0.2.84", {"start": v(843.98, 1751.1) * mm, "end": v(775.68, 1808.51) * mm});
            skLineSegment(sketch, "E2.0.2.85", {"start": v(927.84, 1781.56) * mm, "end": v(843.98, 1751.1) * mm});
            skLineSegment(sketch, "E2.0.2.86", {"start": v(728.51, 1869.4) * mm, "end": v(712.95, 1781.56) * mm});
            skLineSegment(sketch, "E2.0.2.87", {"start": v(712.95, 2000) * mm, "end": v(629.1, 1969.55) * mm});
            skLineSegment(sketch, "E2.0.2.88", {"start": v(927.84, 1563.12) * mm, "end": v(843.98, 1532.67) * mm});
            skLineSegment(sketch, "E2.0.2.89", {"start": v(728.51, 1650.97) * mm, "end": v(712.95, 1563.12) * mm});
            skLineSegment(sketch, "E2.0.2.90", {"start": v(199.32, 1969.55) * mm, "end": v(131.02, 2026.95) * mm});
            skLineSegment(sketch, "E2.0.2.91", {"start": v(775.68, 2026.95) * mm, "end": v(791.24, 2114.8) * mm});
            skLineSegment(sketch, "E2.0.2.92", {"start": v(283.18, 1563.12) * mm, "end": v(199.32, 1532.67) * mm});
            skLineSegment(sketch, "E2.0.2.93", {"start": v(843.98, 1532.67) * mm, "end": v(775.68, 1590.07) * mm});
            skLineSegment(sketch, "E2.0.2.94", {"start": v(445.33, 1926.81) * mm, "end": v(513.63, 1869.4) * mm});
            skLineSegment(sketch, "E2.0.2.95", {"start": v(131.02, 2026.95) * mm, "end": v(146.58, 2114.8) * mm});
            skLineSegment(sketch, "E2.0.2.96", {"start": v(131.02, 1808.51) * mm, "end": v(146.58, 1896.36) * mm});
            skLineSegment(sketch, "E2.0.2.97", {"start": v(68.3, 2000) * mm, "end": v(-15.56, 1969.55) * mm});
            skLineSegment(sketch, "E2.0.2.98", {"start": v(68.3, 1563.12) * mm, "end": v(-15.56, 1532.67) * mm});
            skLineSegment(sketch, "E2.0.2.99", {"start": v(-83.86, 1590.07) * mm, "end": v(-68.3, 1677.92) * mm});
            skLineSegment(sketch, "E2.0.2.100", {"start": v(15.56, 1708.37) * mm, "end": v(83.86, 1650.97) * mm});
            skLineSegment(sketch, "E2.0.2.101", {"start": v(83.86, 1650.97) * mm, "end": v(68.3, 1563.12) * mm});
            skLineSegment(sketch, "E2.0.2.102", {"start": v(68.3, 1781.56) * mm, "end": v(-15.56, 1751.1) * mm});
            skLineSegment(sketch, "E2.0.2.103", {"start": v(875.1, 1926.81) * mm, "end": v(943.4, 1869.4) * mm});
            skLineSegment(sketch, "E2.0.2.104", {"start": v(199.32, 1532.67) * mm, "end": v(131.02, 1590.07) * mm});
            skLineSegment(sketch, "E2.0.2.105", {"start": v(775.68, 1590.07) * mm, "end": v(791.24, 1677.92) * mm});
            skLineSegment(sketch, "E2.0.2.106", {"start": v(712.95, 1781.56) * mm, "end": v(629.1, 1751.1) * mm});
            skLineSegment(sketch, "E2.0.2.107", {"start": v(560.8, 2026.95) * mm, "end": v(576.35, 2114.8) * mm});
            skLineSegment(sketch, "E2.0.2.108", {"start": v(712.95, 1563.12) * mm, "end": v(629.1, 1532.67) * mm});
            skLineSegment(sketch, "E2.0.2.109", {"start": v(146.58, 1896.36) * mm, "end": v(230.44, 1926.81) * mm});
            skLineSegment(sketch, "E2.0.2.110", {"start": v(230.44, 2145.25) * mm, "end": v(298.74, 2087.85) * mm});
            skLineSegment(sketch, "E2.0.2.111", {"start": v(131.02, 1590.07) * mm, "end": v(146.58, 1677.92) * mm});
            skLineSegment(sketch, "E2.0.2.112", {"start": v(791.24, 1677.92) * mm, "end": v(875.1, 1708.37) * mm});
            skLineSegment(sketch, "E2.0.2.113", {"start": v(-83.86, 2026.95) * mm, "end": v(-68.3, 2114.8) * mm});
            skLineSegment(sketch, "E2.0.2.114", {"start": v(629.1, 1532.67) * mm, "end": v(560.8, 1590.07) * mm});
            skLineSegment(sketch, "E2.0.2.115", {"start": v(230.44, 1926.81) * mm, "end": v(298.74, 1869.4) * mm});
            skLineSegment(sketch, "E2.0.2.116", {"start": v(498.07, 2000) * mm, "end": v(414.2, 1969.55) * mm});
            skLineSegment(sketch, "E2.0.2.117", {"start": v(298.74, 2087.85) * mm, "end": v(283.18, 2000) * mm});
            skLineSegment(sketch, "E2.0.2.118", {"start": v(560.8, 1808.51) * mm, "end": v(576.35, 1896.36) * mm});
            skLineSegment(sketch, "E2.0.2.119", {"start": v(560.8, 1590.07) * mm, "end": v(576.35, 1677.92) * mm});
            skLineSegment(sketch, "E2.0.2.120", {"start": v(498.07, 1781.56) * mm, "end": v(414.2, 1751.1) * mm});
            skLineSegment(sketch, "E2.0.2.121", {"start": v(298.74, 1869.4) * mm, "end": v(283.18, 1781.56) * mm});
            skLineSegment(sketch, "E2.1.0.0", {"start": v(2104.18, 30.45) * mm, "end": v(2088.62, -57.4) * mm});
            skLineSegment(sketch, "E2.1.0.1", {"start": v(1076.92, -30.45) * mm, "end": v(1076.92, 188) * mm, "construction": true});
            skLineSegment(sketch, "E2.1.0.2", {"start": v(1391.22, 87.85) * mm, "end": v(1459.52, 30.45) * mm});
            skCircle(sketch, "E2.1.0.3", {"center": v(1590.55, 0) * mm, "radius": 77.26 * mm, "construction": true});
            skLineSegment(sketch, "E2.1.0.4", {"start": v(1574.99, 349.03) * mm, "end": v(1506.69, 406.43) * mm});
            skPoint(sketch, "E2.1.0.5", {"position": v(2046.69, 145.81) * mm});
            skPoint(sketch, "E2.1.0.6", {"position": v(1402.03, 364.25) * mm});
            skLineSegment(sketch, "E2.1.0.7", {"start": v(1176.34, 524.73) * mm, "end": v(1244.64, 467.33) * mm});
            skLineSegment(sketch, "E2.1.0.8", {"start": v(1737.13, 57.4) * mm, "end": v(1821, 87.85) * mm});
            skLineSegment(sketch, "E2.1.0.9", {"start": v(1574.99, 130.59) * mm, "end": v(1506.69, 188) * mm});
            skCircle(sketch, "E2.1.0.10", {"center": v(1375.66, 436.88) * mm, "radius": 77.26 * mm, "construction": true});
            skPoint(sketch, "E2.1.0.11", {"position": v(1187.15, 364.25) * mm});
            skPoint(sketch, "E2.1.0.12", {"position": v(1831.8, 145.81) * mm});
            skCircle(sketch, "E2.1.0.13", {"center": v(2020.32, 218.44) * mm, "radius": 77.26 * mm, "construction": true});
            skLineSegment(sketch, "E2.1.0.14", {"start": v(1244.64, 467.33) * mm, "end": v(1229.08, 379.48) * mm});
            skCircle(sketch, "E2.1.0.15", {"center": v(1805.43, 436.88) * mm, "radius": 77.26 * mm, "construction": true});
            skCircle(sketch, "E2.1.0.16", {"center": v(2020.32, 0) * mm, "radius": 77.26 * mm, "construction": true});
            skLineSegment(sketch, "E2.1.0.17", {"start": v(1606.1, 524.73) * mm, "end": v(1674.4, 467.33) * mm});
            skLineSegment(sketch, "E2.1.0.18", {"start": v(1506.69, -30.45) * mm, "end": v(1522.25, 57.4) * mm});
            skLineSegment(sketch, "E2.1.0.19", {"start": v(1506.69, 188) * mm, "end": v(1522.25, 275.84) * mm});
            skPoint(sketch, "E2.1.0.20", {"position": v(1831.8, -72.63) * mm});
            skPoint(sketch, "E2.1.0.21", {"position": v(1187.15, 145.81) * mm});
            skPoint(sketch, "E2.1.0.22", {"position": v(1616.92, -72.63) * mm});
            skPoint(sketch, "E2.1.0.23", {"position": v(2046.69, 364.25) * mm});
            skLineSegment(sketch, "E2.1.0.24", {"start": v(1522.25, 494.28) * mm, "end": v(1606.1, 524.73) * mm});
            skLineSegment(sketch, "E2.1.0.25", {"start": v(1574.99, -87.85) * mm, "end": v(1506.69, -30.45) * mm});
            skCircle(sketch, "E2.1.0.26", {"center": v(1375.66, 218.44) * mm, "radius": 77.26 * mm, "construction": true});
            skCircle(sketch, "E2.1.0.27", {"center": v(1375.66, 0) * mm, "radius": 77.26 * mm, "construction": true});
            skLineSegment(sketch, "E2.1.0.28", {"start": v(1674.4, 467.33) * mm, "end": v(1658.85, 379.48) * mm});
            skLineSegment(sketch, "E2.1.0.29", {"start": v(1522.25, 275.84) * mm, "end": v(1606.1, 306.3) * mm});
            skLineSegment(sketch, "E2.1.0.30", {"start": v(1522.25, 57.4) * mm, "end": v(1606.1, 87.85) * mm});
            skLineSegment(sketch, "E2.1.0.31", {"start": v(1360.1, 130.59) * mm, "end": v(1291.8, 188) * mm});
            skLineSegment(sketch, "E2.1.0.32", {"start": v(1936.46, 188) * mm, "end": v(1952.02, 275.84) * mm});
            skPoint(sketch, "E2.1.0.33", {"position": v(1402.03, -72.63) * mm});
            skPoint(sketch, "E2.1.0.34", {"position": v(1831.8, 364.25) * mm});
            skLineSegment(sketch, "E2.1.0.35", {"start": v(1789.87, 349.03) * mm, "end": v(1721.57, 406.43) * mm});
            skCircle(sketch, "E2.1.0.36", {"center": v(1805.43, 218.44) * mm, "radius": 77.26 * mm, "construction": true});
            skCircle(sketch, "E2.1.0.37", {"center": v(1805.43, 0) * mm, "radius": 77.26 * mm, "construction": true});
            skLineSegment(sketch, "E2.1.0.38", {"start": v(1606.1, 87.85) * mm, "end": v(1674.4, 30.45) * mm});
            skLineSegment(sketch, "E2.1.0.39", {"start": v(1952.02, 494.28) * mm, "end": v(2035.88, 524.73) * mm});
            skLineSegment(sketch, "E2.1.0.40", {"start": v(1952.02, 275.84) * mm, "end": v(2035.88, 306.3) * mm});
            skLineSegment(sketch, "E2.1.0.41", {"start": v(1244.64, 248.89) * mm, "end": v(1229.08, 161.04) * mm});
            skCircle(sketch, "E2.1.0.42", {"center": v(1160.78, 436.88) * mm, "radius": 77.26 * mm, "construction": true});
            skCircle(sketch, "E2.1.0.43", {"center": v(1160.78, 0) * mm, "radius": 77.26 * mm, "construction": true});
            skLineSegment(sketch, "E2.1.0.44", {"start": v(1145.22, -87.85) * mm, "end": v(1076.92, -30.45) * mm});
            skLineSegment(sketch, "E2.1.0.45", {"start": v(1092.48, 57.4) * mm, "end": v(1176.34, 87.85) * mm});
            skCircle(sketch, "E2.1.0.46", {"center": v(1160.78, 218.44) * mm, "radius": 77.26 * mm, "construction": true});
            skLineSegment(sketch, "E2.1.0.47", {"start": v(1145.22, 130.59) * mm, "end": v(1076.92, 188) * mm});
            skLineSegment(sketch, "E2.1.0.48", {"start": v(1076.92, 188) * mm, "end": v(1092.48, 275.84) * mm});
            skLineSegment(sketch, "E2.1.0.49", {"start": v(1092.48, 275.84) * mm, "end": v(1176.34, 306.3) * mm});
            skLineSegment(sketch, "E2.1.0.50", {"start": v(1176.34, 306.3) * mm, "end": v(1244.64, 248.89) * mm});
            skPoint(sketch, "E2.1.0.51", {"position": v(1616.92, 145.81) * mm});
            skLineSegment(sketch, "E2.1.0.52", {"start": v(1674.4, 248.89) * mm, "end": v(1658.85, 161.04) * mm});
            skLineSegment(sketch, "E2.1.0.53", {"start": v(1307.36, 494.28) * mm, "end": v(1391.22, 524.73) * mm});
            skLineSegment(sketch, "E2.1.0.54", {"start": v(2035.88, 524.73) * mm, "end": v(2104.18, 467.33) * mm});
            skLineSegment(sketch, "E2.1.0.55", {"start": v(1145.22, 349.03) * mm, "end": v(1076.92, 406.43) * mm});
            skLineSegment(sketch, "E2.1.0.56", {"start": v(1674.4, 30.45) * mm, "end": v(1658.85, -57.4) * mm});
            skCircle(sketch, "E2.1.0.57", {"center": v(1590.55, 436.88) * mm, "radius": 77.26 * mm, "construction": true});
            skLineSegment(sketch, "E2.1.0.58", {"start": v(2104.18, 467.33) * mm, "end": v(2088.62, 379.48) * mm});
            skLineSegment(sketch, "E2.1.0.59", {"start": v(1789.87, 130.59) * mm, "end": v(1721.57, 188) * mm});
            skPoint(sketch, "E2.1.0.60", {"position": v(1402.03, 145.81) * mm});
            skPoint(sketch, "E2.1.0.61", {"position": v(2046.69, -72.63) * mm});
            skLineSegment(sketch, "E2.1.0.62", {"start": v(1737.13, 494.28) * mm, "end": v(1821, 524.73) * mm});
            skCircle(sketch, "E2.1.0.63", {"center": v(1590.55, 218.44) * mm, "radius": 77.26 * mm, "construction": true});
            skLineSegment(sketch, "E2.1.0.64", {"start": v(2104.18, 248.89) * mm, "end": v(2088.62, 161.04) * mm});
            skLineSegment(sketch, "E2.1.0.65", {"start": v(1307.36, 57.4) * mm, "end": v(1391.22, 87.85) * mm});
            skLineSegment(sketch, "E2.1.0.66", {"start": v(1076.92, -30.45) * mm, "end": v(1291.8, -30.45) * mm, "construction": true});
            skLineSegment(sketch, "E2.1.0.67", {"start": v(2035.88, 87.85) * mm, "end": v(2104.18, 30.45) * mm});
            skLineSegment(sketch, "E2.1.0.68", {"start": v(1092.48, 494.28) * mm, "end": v(1176.34, 524.73) * mm});
            skLineSegment(sketch, "E2.1.0.69", {"start": v(1821, 524.73) * mm, "end": v(1889.3, 467.33) * mm});
            skCircle(sketch, "E2.1.0.70", {"center": v(2020.32, 436.88) * mm, "radius": 77.26 * mm, "construction": true});
            skPoint(sketch, "E2.1.0.71", {"position": v(1616.92, 364.25) * mm});
            skPoint(sketch, "E2.1.0.72", {"position": v(1187.15, -72.63) * mm});
            skLineSegment(sketch, "E2.1.0.73", {"start": v(1737.13, 275.84) * mm, "end": v(1821, 306.3) * mm});
            skLineSegment(sketch, "E2.1.0.74", {"start": v(1889.3, 467.33) * mm, "end": v(1873.73, 379.48) * mm});
            skLineSegment(sketch, "E2.1.0.75", {"start": v(2088.62, 379.48) * mm, "end": v(2004.76, 349.03) * mm});
            skLineSegment(sketch, "E2.1.0.76", {"start": v(1506.69, 406.43) * mm, "end": v(1522.25, 494.28) * mm});
            skLineSegment(sketch, "E2.1.0.77", {"start": v(1658.85, -57.4) * mm, "end": v(1574.99, -87.85) * mm});
            skLineSegment(sketch, "E2.1.0.78", {"start": v(1459.52, 30.45) * mm, "end": v(1443.96, -57.4) * mm});
            skLineSegment(sketch, "E2.1.0.79", {"start": v(1821, 306.3) * mm, "end": v(1889.3, 248.89) * mm});
            skLineSegment(sketch, "E2.1.0.80", {"start": v(1821, 87.85) * mm, "end": v(1889.3, 30.45) * mm});
            skLineSegment(sketch, "E2.1.0.81", {"start": v(1443.96, 379.48) * mm, "end": v(1360.1, 349.03) * mm});
            skLineSegment(sketch, "E2.1.0.82", {"start": v(1443.96, 161.04) * mm, "end": v(1360.1, 130.59) * mm});
            skLineSegment(sketch, "E2.1.0.83", {"start": v(2004.76, 349.03) * mm, "end": v(1936.46, 406.43) * mm});
            skLineSegment(sketch, "E2.1.0.84", {"start": v(2004.76, 130.59) * mm, "end": v(1936.46, 188) * mm});
            skLineSegment(sketch, "E2.1.0.85", {"start": v(2088.62, 161.04) * mm, "end": v(2004.76, 130.59) * mm});
            skLineSegment(sketch, "E2.1.0.86", {"start": v(1889.3, 248.89) * mm, "end": v(1873.73, 161.04) * mm});
            skLineSegment(sketch, "E2.1.0.87", {"start": v(1873.73, 379.48) * mm, "end": v(1789.87, 349.03) * mm});
            skLineSegment(sketch, "E2.1.0.88", {"start": v(2088.62, -57.4) * mm, "end": v(2004.76, -87.85) * mm});
            skLineSegment(sketch, "E2.1.0.89", {"start": v(1889.3, 30.45) * mm, "end": v(1873.73, -57.4) * mm});
            skLineSegment(sketch, "E2.1.0.90", {"start": v(1360.1, 349.03) * mm, "end": v(1291.8, 406.43) * mm});
            skLineSegment(sketch, "E2.1.0.91", {"start": v(1936.46, 406.43) * mm, "end": v(1952.02, 494.28) * mm});
            skLineSegment(sketch, "E2.1.0.92", {"start": v(1443.96, -57.4) * mm, "end": v(1360.1, -87.85) * mm});
            skLineSegment(sketch, "E2.1.0.93", {"start": v(2004.76, -87.85) * mm, "end": v(1936.46, -30.45) * mm});
            skLineSegment(sketch, "E2.1.0.94", {"start": v(1606.1, 306.3) * mm, "end": v(1674.4, 248.89) * mm});
            skLineSegment(sketch, "E2.1.0.95", {"start": v(1291.8, 406.43) * mm, "end": v(1307.36, 494.28) * mm});
            skLineSegment(sketch, "E2.1.0.96", {"start": v(1291.8, 188) * mm, "end": v(1307.36, 275.84) * mm});
            skLineSegment(sketch, "E2.1.0.97", {"start": v(1229.08, 379.48) * mm, "end": v(1145.22, 349.03) * mm});
            skLineSegment(sketch, "E2.1.0.98", {"start": v(1229.08, -57.4) * mm, "end": v(1145.22, -87.85) * mm});
            skLineSegment(sketch, "E2.1.0.99", {"start": v(1076.92, -30.45) * mm, "end": v(1092.48, 57.4) * mm});
            skLineSegment(sketch, "E2.1.0.100", {"start": v(1176.34, 87.85) * mm, "end": v(1244.64, 30.45) * mm});
            skLineSegment(sketch, "E2.1.0.101", {"start": v(1244.64, 30.45) * mm, "end": v(1229.08, -57.4) * mm});
            skLineSegment(sketch, "E2.1.0.102", {"start": v(1229.08, 161.04) * mm, "end": v(1145.22, 130.59) * mm});
            skLineSegment(sketch, "E2.1.0.103", {"start": v(2035.88, 306.3) * mm, "end": v(2104.18, 248.89) * mm});
            skLineSegment(sketch, "E2.1.0.104", {"start": v(1360.1, -87.85) * mm, "end": v(1291.8, -30.45) * mm});
            skLineSegment(sketch, "E2.1.0.105", {"start": v(1936.46, -30.45) * mm, "end": v(1952.02, 57.4) * mm});
            skLineSegment(sketch, "E2.1.0.106", {"start": v(1873.73, 161.04) * mm, "end": v(1789.87, 130.59) * mm});
            skLineSegment(sketch, "E2.1.0.107", {"start": v(1721.57, 406.43) * mm, "end": v(1737.13, 494.28) * mm});
            skLineSegment(sketch, "E2.1.0.108", {"start": v(1873.73, -57.4) * mm, "end": v(1789.87, -87.85) * mm});
            skLineSegment(sketch, "E2.1.0.109", {"start": v(1307.36, 275.84) * mm, "end": v(1391.22, 306.3) * mm});
            skLineSegment(sketch, "E2.1.0.110", {"start": v(1391.22, 524.73) * mm, "end": v(1459.52, 467.33) * mm});
            skLineSegment(sketch, "E2.1.0.111", {"start": v(1291.8, -30.45) * mm, "end": v(1307.36, 57.4) * mm});
            skLineSegment(sketch, "E2.1.0.112", {"start": v(1952.02, 57.4) * mm, "end": v(2035.88, 87.85) * mm});
            skLineSegment(sketch, "E2.1.0.113", {"start": v(1076.92, 406.43) * mm, "end": v(1092.48, 494.28) * mm});
            skLineSegment(sketch, "E2.1.0.114", {"start": v(1789.87, -87.85) * mm, "end": v(1721.57, -30.45) * mm});
            skLineSegment(sketch, "E2.1.0.115", {"start": v(1391.22, 306.3) * mm, "end": v(1459.52, 248.89) * mm});
            skLineSegment(sketch, "E2.1.0.116", {"start": v(1658.85, 379.48) * mm, "end": v(1574.99, 349.03) * mm});
            skLineSegment(sketch, "E2.1.0.117", {"start": v(1459.52, 467.33) * mm, "end": v(1443.96, 379.48) * mm});
            skLineSegment(sketch, "E2.1.0.118", {"start": v(1721.57, 188) * mm, "end": v(1737.13, 275.84) * mm});
            skLineSegment(sketch, "E2.1.0.119", {"start": v(1721.57, -30.45) * mm, "end": v(1737.13, 57.4) * mm});
            skLineSegment(sketch, "E2.1.0.120", {"start": v(1658.85, 161.04) * mm, "end": v(1574.99, 130.59) * mm});
            skLineSegment(sketch, "E2.1.0.121", {"start": v(1459.52, 248.89) * mm, "end": v(1443.96, 161.04) * mm});
            skLineSegment(sketch, "E2.1.1.0", {"start": v(2104.18, 840.7) * mm, "end": v(2088.62, 752.86) * mm});
            skLineSegment(sketch, "E2.1.1.1", {"start": v(1076.92, 779.81) * mm, "end": v(1076.92, 998.25) * mm, "construction": true});
            skLineSegment(sketch, "E2.1.1.2", {"start": v(1391.22, 898.11) * mm, "end": v(1459.52, 840.7) * mm});
            skCircle(sketch, "E2.1.1.3", {"center": v(1590.55, 810.26) * mm, "radius": 77.26 * mm, "construction": true});
            skLineSegment(sketch, "E2.1.1.4", {"start": v(1574.99, 1159.29) * mm, "end": v(1506.69, 1216.7) * mm});
            skPoint(sketch, "E2.1.1.5", {"position": v(2046.69, 956.07) * mm});
            skPoint(sketch, "E2.1.1.6", {"position": v(1402.03, 1174.51) * mm});
            skLineSegment(sketch, "E2.1.1.7", {"start": v(1176.34, 1335) * mm, "end": v(1244.64, 1277.59) * mm});
            skLineSegment(sketch, "E2.1.1.8", {"start": v(1737.13, 867.66) * mm, "end": v(1821, 898.11) * mm});
            skLineSegment(sketch, "E2.1.1.9", {"start": v(1574.99, 940.85) * mm, "end": v(1506.69, 998.25) * mm});
            skCircle(sketch, "E2.1.1.10", {"center": v(1375.66, 1247.14) * mm, "radius": 77.26 * mm, "construction": true});
            skPoint(sketch, "E2.1.1.11", {"position": v(1187.15, 1174.51) * mm});
            skPoint(sketch, "E2.1.1.12", {"position": v(1831.8, 956.07) * mm});
            skCircle(sketch, "E2.1.1.13", {"center": v(2020.32, 1028.7) * mm, "radius": 77.26 * mm, "construction": true});
            skLineSegment(sketch, "E2.1.1.14", {"start": v(1244.64, 1277.59) * mm, "end": v(1229.08, 1189.74) * mm});
            skCircle(sketch, "E2.1.1.15", {"center": v(1805.43, 1247.14) * mm, "radius": 77.26 * mm, "construction": true});
            skCircle(sketch, "E2.1.1.16", {"center": v(2020.32, 810.26) * mm, "radius": 77.26 * mm, "construction": true});
            skLineSegment(sketch, "E2.1.1.17", {"start": v(1606.1, 1335) * mm, "end": v(1674.4, 1277.59) * mm});
            skLineSegment(sketch, "E2.1.1.18", {"start": v(1506.69, 779.81) * mm, "end": v(1522.25, 867.66) * mm});
            skLineSegment(sketch, "E2.1.1.19", {"start": v(1506.69, 998.25) * mm, "end": v(1522.25, 1086.1) * mm});
            skPoint(sketch, "E2.1.1.20", {"position": v(1831.8, 737.63) * mm});
            skPoint(sketch, "E2.1.1.21", {"position": v(1187.15, 956.07) * mm});
            skPoint(sketch, "E2.1.1.22", {"position": v(1616.92, 737.63) * mm});
            skPoint(sketch, "E2.1.1.23", {"position": v(2046.69, 1174.51) * mm});
            skLineSegment(sketch, "E2.1.1.24", {"start": v(1522.25, 1304.54) * mm, "end": v(1606.1, 1335) * mm});
            skLineSegment(sketch, "E2.1.1.25", {"start": v(1574.99, 722.4) * mm, "end": v(1506.69, 779.81) * mm});
            skCircle(sketch, "E2.1.1.26", {"center": v(1375.66, 1028.7) * mm, "radius": 77.26 * mm, "construction": true});
            skCircle(sketch, "E2.1.1.27", {"center": v(1375.66, 810.26) * mm, "radius": 77.26 * mm, "construction": true});
            skLineSegment(sketch, "E2.1.1.28", {"start": v(1674.4, 1277.59) * mm, "end": v(1658.85, 1189.74) * mm});
            skLineSegment(sketch, "E2.1.1.29", {"start": v(1522.25, 1086.1) * mm, "end": v(1606.1, 1116.55) * mm});
            skLineSegment(sketch, "E2.1.1.30", {"start": v(1522.25, 867.66) * mm, "end": v(1606.1, 898.11) * mm});
            skLineSegment(sketch, "E2.1.1.31", {"start": v(1360.1, 940.85) * mm, "end": v(1291.8, 998.25) * mm});
            skLineSegment(sketch, "E2.1.1.32", {"start": v(1936.46, 998.25) * mm, "end": v(1952.02, 1086.1) * mm});
            skPoint(sketch, "E2.1.1.33", {"position": v(1402.03, 737.63) * mm});
            skPoint(sketch, "E2.1.1.34", {"position": v(1831.8, 1174.51) * mm});
            skLineSegment(sketch, "E2.1.1.35", {"start": v(1789.87, 1159.29) * mm, "end": v(1721.57, 1216.7) * mm});
            skCircle(sketch, "E2.1.1.36", {"center": v(1805.43, 1028.7) * mm, "radius": 77.26 * mm, "construction": true});
            skCircle(sketch, "E2.1.1.37", {"center": v(1805.43, 810.26) * mm, "radius": 77.26 * mm, "construction": true});
            skLineSegment(sketch, "E2.1.1.38", {"start": v(1606.1, 898.11) * mm, "end": v(1674.4, 840.7) * mm});
            skLineSegment(sketch, "E2.1.1.39", {"start": v(1952.02, 1304.54) * mm, "end": v(2035.88, 1335) * mm});
            skLineSegment(sketch, "E2.1.1.40", {"start": v(1952.02, 1086.1) * mm, "end": v(2035.88, 1116.55) * mm});
            skLineSegment(sketch, "E2.1.1.41", {"start": v(1244.64, 1059.15) * mm, "end": v(1229.08, 971.3) * mm});
            skCircle(sketch, "E2.1.1.42", {"center": v(1160.78, 1247.14) * mm, "radius": 77.26 * mm, "construction": true});
            skCircle(sketch, "E2.1.1.43", {"center": v(1160.78, 810.26) * mm, "radius": 77.26 * mm, "construction": true});
            skLineSegment(sketch, "E2.1.1.44", {"start": v(1145.22, 722.4) * mm, "end": v(1076.92, 779.81) * mm});
            skLineSegment(sketch, "E2.1.1.45", {"start": v(1092.48, 867.66) * mm, "end": v(1176.34, 898.11) * mm});
            skCircle(sketch, "E2.1.1.46", {"center": v(1160.78, 1028.7) * mm, "radius": 77.26 * mm, "construction": true});
            skLineSegment(sketch, "E2.1.1.47", {"start": v(1145.22, 940.85) * mm, "end": v(1076.92, 998.25) * mm});
            skLineSegment(sketch, "E2.1.1.48", {"start": v(1076.92, 998.25) * mm, "end": v(1092.48, 1086.1) * mm});
            skLineSegment(sketch, "E2.1.1.49", {"start": v(1092.48, 1086.1) * mm, "end": v(1176.34, 1116.55) * mm});
            skLineSegment(sketch, "E2.1.1.50", {"start": v(1176.34, 1116.55) * mm, "end": v(1244.64, 1059.15) * mm});
            skPoint(sketch, "E2.1.1.51", {"position": v(1616.92, 956.07) * mm});
            skLineSegment(sketch, "E2.1.1.52", {"start": v(1674.4, 1059.15) * mm, "end": v(1658.85, 971.3) * mm});
            skLineSegment(sketch, "E2.1.1.53", {"start": v(1307.36, 1304.54) * mm, "end": v(1391.22, 1335) * mm});
            skLineSegment(sketch, "E2.1.1.54", {"start": v(2035.88, 1335) * mm, "end": v(2104.18, 1277.59) * mm});
            skLineSegment(sketch, "E2.1.1.55", {"start": v(1145.22, 1159.29) * mm, "end": v(1076.92, 1216.7) * mm});
            skLineSegment(sketch, "E2.1.1.56", {"start": v(1674.4, 840.7) * mm, "end": v(1658.85, 752.86) * mm});
            skCircle(sketch, "E2.1.1.57", {"center": v(1590.55, 1247.14) * mm, "radius": 77.26 * mm, "construction": true});
            skLineSegment(sketch, "E2.1.1.58", {"start": v(2104.18, 1277.59) * mm, "end": v(2088.62, 1189.74) * mm});
            skLineSegment(sketch, "E2.1.1.59", {"start": v(1789.87, 940.85) * mm, "end": v(1721.57, 998.25) * mm});
            skPoint(sketch, "E2.1.1.60", {"position": v(1402.03, 956.07) * mm});
            skPoint(sketch, "E2.1.1.61", {"position": v(2046.69, 737.63) * mm});
            skLineSegment(sketch, "E2.1.1.62", {"start": v(1737.13, 1304.54) * mm, "end": v(1821, 1335) * mm});
            skCircle(sketch, "E2.1.1.63", {"center": v(1590.55, 1028.7) * mm, "radius": 77.26 * mm, "construction": true});
            skLineSegment(sketch, "E2.1.1.64", {"start": v(2104.18, 1059.15) * mm, "end": v(2088.62, 971.3) * mm});
            skLineSegment(sketch, "E2.1.1.65", {"start": v(1307.36, 867.66) * mm, "end": v(1391.22, 898.11) * mm});
            skLineSegment(sketch, "E2.1.1.66", {"start": v(1076.92, 779.81) * mm, "end": v(1291.8, 779.81) * mm, "construction": true});
            skLineSegment(sketch, "E2.1.1.67", {"start": v(2035.88, 898.11) * mm, "end": v(2104.18, 840.7) * mm});
            skLineSegment(sketch, "E2.1.1.68", {"start": v(1092.48, 1304.54) * mm, "end": v(1176.34, 1335) * mm});
            skLineSegment(sketch, "E2.1.1.69", {"start": v(1821, 1335) * mm, "end": v(1889.3, 1277.59) * mm});
            skCircle(sketch, "E2.1.1.70", {"center": v(2020.32, 1247.14) * mm, "radius": 77.26 * mm, "construction": true});
            skPoint(sketch, "E2.1.1.71", {"position": v(1616.92, 1174.51) * mm});
            skPoint(sketch, "E2.1.1.72", {"position": v(1187.15, 737.63) * mm});
            skLineSegment(sketch, "E2.1.1.73", {"start": v(1737.13, 1086.1) * mm, "end": v(1821, 1116.55) * mm});
            skLineSegment(sketch, "E2.1.1.74", {"start": v(1889.3, 1277.59) * mm, "end": v(1873.73, 1189.74) * mm});
            skLineSegment(sketch, "E2.1.1.75", {"start": v(2088.62, 1189.74) * mm, "end": v(2004.76, 1159.29) * mm});
            skLineSegment(sketch, "E2.1.1.76", {"start": v(1506.69, 1216.7) * mm, "end": v(1522.25, 1304.54) * mm});
            skLineSegment(sketch, "E2.1.1.77", {"start": v(1658.85, 752.86) * mm, "end": v(1574.99, 722.4) * mm});
            skLineSegment(sketch, "E2.1.1.78", {"start": v(1459.52, 840.7) * mm, "end": v(1443.96, 752.86) * mm});
            skLineSegment(sketch, "E2.1.1.79", {"start": v(1821, 1116.55) * mm, "end": v(1889.3, 1059.15) * mm});
            skLineSegment(sketch, "E2.1.1.80", {"start": v(1821, 898.11) * mm, "end": v(1889.3, 840.7) * mm});
            skLineSegment(sketch, "E2.1.1.81", {"start": v(1443.96, 1189.74) * mm, "end": v(1360.1, 1159.29) * mm});
            skLineSegment(sketch, "E2.1.1.82", {"start": v(1443.96, 971.3) * mm, "end": v(1360.1, 940.85) * mm});
            skLineSegment(sketch, "E2.1.1.83", {"start": v(2004.76, 1159.29) * mm, "end": v(1936.46, 1216.7) * mm});
            skLineSegment(sketch, "E2.1.1.84", {"start": v(2004.76, 940.85) * mm, "end": v(1936.46, 998.25) * mm});
            skLineSegment(sketch, "E2.1.1.85", {"start": v(2088.62, 971.3) * mm, "end": v(2004.76, 940.85) * mm});
            skLineSegment(sketch, "E2.1.1.86", {"start": v(1889.3, 1059.15) * mm, "end": v(1873.73, 971.3) * mm});
            skLineSegment(sketch, "E2.1.1.87", {"start": v(1873.73, 1189.74) * mm, "end": v(1789.87, 1159.29) * mm});
            skLineSegment(sketch, "E2.1.1.88", {"start": v(2088.62, 752.86) * mm, "end": v(2004.76, 722.4) * mm});
            skLineSegment(sketch, "E2.1.1.89", {"start": v(1889.3, 840.7) * mm, "end": v(1873.73, 752.86) * mm});
            skLineSegment(sketch, "E2.1.1.90", {"start": v(1360.1, 1159.29) * mm, "end": v(1291.8, 1216.7) * mm});
            skLineSegment(sketch, "E2.1.1.91", {"start": v(1936.46, 1216.7) * mm, "end": v(1952.02, 1304.54) * mm});
            skLineSegment(sketch, "E2.1.1.92", {"start": v(1443.96, 752.86) * mm, "end": v(1360.1, 722.4) * mm});
            skLineSegment(sketch, "E2.1.1.93", {"start": v(2004.76, 722.4) * mm, "end": v(1936.46, 779.81) * mm});
            skLineSegment(sketch, "E2.1.1.94", {"start": v(1606.1, 1116.55) * mm, "end": v(1674.4, 1059.15) * mm});
            skLineSegment(sketch, "E2.1.1.95", {"start": v(1291.8, 1216.7) * mm, "end": v(1307.36, 1304.54) * mm});
            skLineSegment(sketch, "E2.1.1.96", {"start": v(1291.8, 998.25) * mm, "end": v(1307.36, 1086.1) * mm});
            skLineSegment(sketch, "E2.1.1.97", {"start": v(1229.08, 1189.74) * mm, "end": v(1145.22, 1159.29) * mm});
            skLineSegment(sketch, "E2.1.1.98", {"start": v(1229.08, 752.86) * mm, "end": v(1145.22, 722.4) * mm});
            skLineSegment(sketch, "E2.1.1.99", {"start": v(1076.92, 779.81) * mm, "end": v(1092.48, 867.66) * mm});
            skLineSegment(sketch, "E2.1.1.100", {"start": v(1176.34, 898.11) * mm, "end": v(1244.64, 840.7) * mm});
            skLineSegment(sketch, "E2.1.1.101", {"start": v(1244.64, 840.7) * mm, "end": v(1229.08, 752.86) * mm});
            skLineSegment(sketch, "E2.1.1.102", {"start": v(1229.08, 971.3) * mm, "end": v(1145.22, 940.85) * mm});
            skLineSegment(sketch, "E2.1.1.103", {"start": v(2035.88, 1116.55) * mm, "end": v(2104.18, 1059.15) * mm});
            skLineSegment(sketch, "E2.1.1.104", {"start": v(1360.1, 722.4) * mm, "end": v(1291.8, 779.81) * mm});
            skLineSegment(sketch, "E2.1.1.105", {"start": v(1936.46, 779.81) * mm, "end": v(1952.02, 867.66) * mm});
            skLineSegment(sketch, "E2.1.1.106", {"start": v(1873.73, 971.3) * mm, "end": v(1789.87, 940.85) * mm});
            skLineSegment(sketch, "E2.1.1.107", {"start": v(1721.57, 1216.7) * mm, "end": v(1737.13, 1304.54) * mm});
            skLineSegment(sketch, "E2.1.1.108", {"start": v(1873.73, 752.86) * mm, "end": v(1789.87, 722.4) * mm});
            skLineSegment(sketch, "E2.1.1.109", {"start": v(1307.36, 1086.1) * mm, "end": v(1391.22, 1116.55) * mm});
            skLineSegment(sketch, "E2.1.1.110", {"start": v(1391.22, 1335) * mm, "end": v(1459.52, 1277.59) * mm});
            skLineSegment(sketch, "E2.1.1.111", {"start": v(1291.8, 779.81) * mm, "end": v(1307.36, 867.66) * mm});
            skLineSegment(sketch, "E2.1.1.112", {"start": v(1952.02, 867.66) * mm, "end": v(2035.88, 898.11) * mm});
            skLineSegment(sketch, "E2.1.1.113", {"start": v(1076.92, 1216.7) * mm, "end": v(1092.48, 1304.54) * mm});
            skLineSegment(sketch, "E2.1.1.114", {"start": v(1789.87, 722.4) * mm, "end": v(1721.57, 779.81) * mm});
            skLineSegment(sketch, "E2.1.1.115", {"start": v(1391.22, 1116.55) * mm, "end": v(1459.52, 1059.15) * mm});
            skLineSegment(sketch, "E2.1.1.116", {"start": v(1658.85, 1189.74) * mm, "end": v(1574.99, 1159.29) * mm});
            skLineSegment(sketch, "E2.1.1.117", {"start": v(1459.52, 1277.59) * mm, "end": v(1443.96, 1189.74) * mm});
            skLineSegment(sketch, "E2.1.1.118", {"start": v(1721.57, 998.25) * mm, "end": v(1737.13, 1086.1) * mm});
            skLineSegment(sketch, "E2.1.1.119", {"start": v(1721.57, 779.81) * mm, "end": v(1737.13, 867.66) * mm});
            skLineSegment(sketch, "E2.1.1.120", {"start": v(1658.85, 971.3) * mm, "end": v(1574.99, 940.85) * mm});
            skLineSegment(sketch, "E2.1.1.121", {"start": v(1459.52, 1059.15) * mm, "end": v(1443.96, 971.3) * mm});
            skLineSegment(sketch, "E2.1.2.0", {"start": v(2104.18, 1650.97) * mm, "end": v(2088.62, 1563.12) * mm});
            skLineSegment(sketch, "E2.1.2.1", {"start": v(1076.92, 1590.07) * mm, "end": v(1076.92, 1808.51) * mm, "construction": true});
            skLineSegment(sketch, "E2.1.2.2", {"start": v(1391.22, 1708.37) * mm, "end": v(1459.52, 1650.97) * mm});
            skCircle(sketch, "E2.1.2.3", {"center": v(1590.55, 1620.52) * mm, "radius": 77.26 * mm, "construction": true});
            skLineSegment(sketch, "E2.1.2.4", {"start": v(1574.99, 1969.55) * mm, "end": v(1506.69, 2026.95) * mm});
            skPoint(sketch, "E2.1.2.5", {"position": v(2046.69, 1766.33) * mm});
            skPoint(sketch, "E2.1.2.6", {"position": v(1402.03, 1984.77) * mm});
            skLineSegment(sketch, "E2.1.2.7", {"start": v(1176.34, 2145.25) * mm, "end": v(1244.64, 2087.85) * mm});
            skLineSegment(sketch, "E2.1.2.8", {"start": v(1737.13, 1677.92) * mm, "end": v(1821, 1708.37) * mm});
            skLineSegment(sketch, "E2.1.2.9", {"start": v(1574.99, 1751.1) * mm, "end": v(1506.69, 1808.51) * mm});
            skCircle(sketch, "E2.1.2.10", {"center": v(1375.66, 2057.4) * mm, "radius": 77.26 * mm, "construction": true});
            skPoint(sketch, "E2.1.2.11", {"position": v(1187.15, 1984.77) * mm});
            skPoint(sketch, "E2.1.2.12", {"position": v(1831.8, 1766.33) * mm});
            skCircle(sketch, "E2.1.2.13", {"center": v(2020.32, 1838.96) * mm, "radius": 77.26 * mm, "construction": true});
            skLineSegment(sketch, "E2.1.2.14", {"start": v(1244.64, 2087.85) * mm, "end": v(1229.08, 2000) * mm});
            skCircle(sketch, "E2.1.2.15", {"center": v(1805.43, 2057.4) * mm, "radius": 77.26 * mm, "construction": true});
            skCircle(sketch, "E2.1.2.16", {"center": v(2020.32, 1620.52) * mm, "radius": 77.26 * mm, "construction": true});
            skLineSegment(sketch, "E2.1.2.17", {"start": v(1606.1, 2145.25) * mm, "end": v(1674.4, 2087.85) * mm});
            skLineSegment(sketch, "E2.1.2.18", {"start": v(1506.69, 1590.07) * mm, "end": v(1522.25, 1677.92) * mm});
            skLineSegment(sketch, "E2.1.2.19", {"start": v(1506.69, 1808.51) * mm, "end": v(1522.25, 1896.36) * mm});
            skPoint(sketch, "E2.1.2.20", {"position": v(1831.8, 1547.9) * mm});
            skPoint(sketch, "E2.1.2.21", {"position": v(1187.15, 1766.33) * mm});
            skPoint(sketch, "E2.1.2.22", {"position": v(1616.92, 1547.9) * mm});
            skPoint(sketch, "E2.1.2.23", {"position": v(2046.69, 1984.77) * mm});
            skLineSegment(sketch, "E2.1.2.24", {"start": v(1522.25, 2114.8) * mm, "end": v(1606.1, 2145.25) * mm});
            skLineSegment(sketch, "E2.1.2.25", {"start": v(1574.99, 1532.67) * mm, "end": v(1506.69, 1590.07) * mm});
            skCircle(sketch, "E2.1.2.26", {"center": v(1375.66, 1838.96) * mm, "radius": 77.26 * mm, "construction": true});
            skCircle(sketch, "E2.1.2.27", {"center": v(1375.66, 1620.52) * mm, "radius": 77.26 * mm, "construction": true});
            skLineSegment(sketch, "E2.1.2.28", {"start": v(1674.4, 2087.85) * mm, "end": v(1658.85, 2000) * mm});
            skLineSegment(sketch, "E2.1.2.29", {"start": v(1522.25, 1896.36) * mm, "end": v(1606.1, 1926.81) * mm});
            skLineSegment(sketch, "E2.1.2.30", {"start": v(1522.25, 1677.92) * mm, "end": v(1606.1, 1708.37) * mm});
            skLineSegment(sketch, "E2.1.2.31", {"start": v(1360.1, 1751.1) * mm, "end": v(1291.8, 1808.51) * mm});
            skLineSegment(sketch, "E2.1.2.32", {"start": v(1936.46, 1808.51) * mm, "end": v(1952.02, 1896.36) * mm});
            skPoint(sketch, "E2.1.2.33", {"position": v(1402.03, 1547.9) * mm});
            skPoint(sketch, "E2.1.2.34", {"position": v(1831.8, 1984.77) * mm});
            skLineSegment(sketch, "E2.1.2.35", {"start": v(1789.87, 1969.55) * mm, "end": v(1721.57, 2026.95) * mm});
            skCircle(sketch, "E2.1.2.36", {"center": v(1805.43, 1838.96) * mm, "radius": 77.26 * mm, "construction": true});
            skCircle(sketch, "E2.1.2.37", {"center": v(1805.43, 1620.52) * mm, "radius": 77.26 * mm, "construction": true});
            skLineSegment(sketch, "E2.1.2.38", {"start": v(1606.1, 1708.37) * mm, "end": v(1674.4, 1650.97) * mm});
            skLineSegment(sketch, "E2.1.2.39", {"start": v(1952.02, 2114.8) * mm, "end": v(2035.88, 2145.25) * mm});
            skLineSegment(sketch, "E2.1.2.40", {"start": v(1952.02, 1896.36) * mm, "end": v(2035.88, 1926.81) * mm});
            skLineSegment(sketch, "E2.1.2.41", {"start": v(1244.64, 1869.4) * mm, "end": v(1229.08, 1781.56) * mm});
            skCircle(sketch, "E2.1.2.42", {"center": v(1160.78, 2057.4) * mm, "radius": 77.26 * mm, "construction": true});
            skCircle(sketch, "E2.1.2.43", {"center": v(1160.78, 1620.52) * mm, "radius": 77.26 * mm, "construction": true});
            skLineSegment(sketch, "E2.1.2.44", {"start": v(1145.22, 1532.67) * mm, "end": v(1076.92, 1590.07) * mm});
            skLineSegment(sketch, "E2.1.2.45", {"start": v(1092.48, 1677.92) * mm, "end": v(1176.34, 1708.37) * mm});
            skCircle(sketch, "E2.1.2.46", {"center": v(1160.78, 1838.96) * mm, "radius": 77.26 * mm, "construction": true});
            skLineSegment(sketch, "E2.1.2.47", {"start": v(1145.22, 1751.1) * mm, "end": v(1076.92, 1808.51) * mm});
            skLineSegment(sketch, "E2.1.2.48", {"start": v(1076.92, 1808.51) * mm, "end": v(1092.48, 1896.36) * mm});
            skLineSegment(sketch, "E2.1.2.49", {"start": v(1092.48, 1896.36) * mm, "end": v(1176.34, 1926.81) * mm});
            skLineSegment(sketch, "E2.1.2.50", {"start": v(1176.34, 1926.81) * mm, "end": v(1244.64, 1869.4) * mm});
            skPoint(sketch, "E2.1.2.51", {"position": v(1616.92, 1766.33) * mm});
            skLineSegment(sketch, "E2.1.2.52", {"start": v(1674.4, 1869.4) * mm, "end": v(1658.85, 1781.56) * mm});
            skLineSegment(sketch, "E2.1.2.53", {"start": v(1307.36, 2114.8) * mm, "end": v(1391.22, 2145.25) * mm});
            skLineSegment(sketch, "E2.1.2.54", {"start": v(2035.88, 2145.25) * mm, "end": v(2104.18, 2087.85) * mm});
            skLineSegment(sketch, "E2.1.2.55", {"start": v(1145.22, 1969.55) * mm, "end": v(1076.92, 2026.95) * mm});
            skLineSegment(sketch, "E2.1.2.56", {"start": v(1674.4, 1650.97) * mm, "end": v(1658.85, 1563.12) * mm});
            skCircle(sketch, "E2.1.2.57", {"center": v(1590.55, 2057.4) * mm, "radius": 77.26 * mm, "construction": true});
            skLineSegment(sketch, "E2.1.2.58", {"start": v(2104.18, 2087.85) * mm, "end": v(2088.62, 2000) * mm});
            skLineSegment(sketch, "E2.1.2.59", {"start": v(1789.87, 1751.1) * mm, "end": v(1721.57, 1808.51) * mm});
            skPoint(sketch, "E2.1.2.60", {"position": v(1402.03, 1766.33) * mm});
            skPoint(sketch, "E2.1.2.61", {"position": v(2046.69, 1547.9) * mm});
            skLineSegment(sketch, "E2.1.2.62", {"start": v(1737.13, 2114.8) * mm, "end": v(1821, 2145.25) * mm});
            skCircle(sketch, "E2.1.2.63", {"center": v(1590.55, 1838.96) * mm, "radius": 77.26 * mm, "construction": true});
            skLineSegment(sketch, "E2.1.2.64", {"start": v(2104.18, 1869.4) * mm, "end": v(2088.62, 1781.56) * mm});
            skLineSegment(sketch, "E2.1.2.65", {"start": v(1307.36, 1677.92) * mm, "end": v(1391.22, 1708.37) * mm});
            skLineSegment(sketch, "E2.1.2.66", {"start": v(1076.92, 1590.07) * mm, "end": v(1291.8, 1590.07) * mm, "construction": true});
            skLineSegment(sketch, "E2.1.2.67", {"start": v(2035.88, 1708.37) * mm, "end": v(2104.18, 1650.97) * mm});
            skLineSegment(sketch, "E2.1.2.68", {"start": v(1092.48, 2114.8) * mm, "end": v(1176.34, 2145.25) * mm});
            skLineSegment(sketch, "E2.1.2.69", {"start": v(1821, 2145.25) * mm, "end": v(1889.3, 2087.85) * mm});
            skCircle(sketch, "E2.1.2.70", {"center": v(2020.32, 2057.4) * mm, "radius": 77.26 * mm, "construction": true});
            skPoint(sketch, "E2.1.2.71", {"position": v(1616.92, 1984.77) * mm});
            skPoint(sketch, "E2.1.2.72", {"position": v(1187.15, 1547.9) * mm});
            skLineSegment(sketch, "E2.1.2.73", {"start": v(1737.13, 1896.36) * mm, "end": v(1821, 1926.81) * mm});
            skLineSegment(sketch, "E2.1.2.74", {"start": v(1889.3, 2087.85) * mm, "end": v(1873.73, 2000) * mm});
            skLineSegment(sketch, "E2.1.2.75", {"start": v(2088.62, 2000) * mm, "end": v(2004.76, 1969.55) * mm});
            skLineSegment(sketch, "E2.1.2.76", {"start": v(1506.69, 2026.95) * mm, "end": v(1522.25, 2114.8) * mm});
            skLineSegment(sketch, "E2.1.2.77", {"start": v(1658.85, 1563.12) * mm, "end": v(1574.99, 1532.67) * mm});
            skLineSegment(sketch, "E2.1.2.78", {"start": v(1459.52, 1650.97) * mm, "end": v(1443.96, 1563.12) * mm});
            skLineSegment(sketch, "E2.1.2.79", {"start": v(1821, 1926.81) * mm, "end": v(1889.3, 1869.4) * mm});
            skLineSegment(sketch, "E2.1.2.80", {"start": v(1821, 1708.37) * mm, "end": v(1889.3, 1650.97) * mm});
            skLineSegment(sketch, "E2.1.2.81", {"start": v(1443.96, 2000) * mm, "end": v(1360.1, 1969.55) * mm});
            skLineSegment(sketch, "E2.1.2.82", {"start": v(1443.96, 1781.56) * mm, "end": v(1360.1, 1751.1) * mm});
            skLineSegment(sketch, "E2.1.2.83", {"start": v(2004.76, 1969.55) * mm, "end": v(1936.46, 2026.95) * mm});
            skLineSegment(sketch, "E2.1.2.84", {"start": v(2004.76, 1751.1) * mm, "end": v(1936.46, 1808.51) * mm});
            skLineSegment(sketch, "E2.1.2.85", {"start": v(2088.62, 1781.56) * mm, "end": v(2004.76, 1751.1) * mm});
            skLineSegment(sketch, "E2.1.2.86", {"start": v(1889.3, 1869.4) * mm, "end": v(1873.73, 1781.56) * mm});
            skLineSegment(sketch, "E2.1.2.87", {"start": v(1873.73, 2000) * mm, "end": v(1789.87, 1969.55) * mm});
            skLineSegment(sketch, "E2.1.2.88", {"start": v(2088.62, 1563.12) * mm, "end": v(2004.76, 1532.67) * mm});
            skLineSegment(sketch, "E2.1.2.89", {"start": v(1889.3, 1650.97) * mm, "end": v(1873.73, 1563.12) * mm});
            skLineSegment(sketch, "E2.1.2.90", {"start": v(1360.1, 1969.55) * mm, "end": v(1291.8, 2026.95) * mm});
            skLineSegment(sketch, "E2.1.2.91", {"start": v(1936.46, 2026.95) * mm, "end": v(1952.02, 2114.8) * mm});
            skLineSegment(sketch, "E2.1.2.92", {"start": v(1443.96, 1563.12) * mm, "end": v(1360.1, 1532.67) * mm});
            skLineSegment(sketch, "E2.1.2.93", {"start": v(2004.76, 1532.67) * mm, "end": v(1936.46, 1590.07) * mm});
            skLineSegment(sketch, "E2.1.2.94", {"start": v(1606.1, 1926.81) * mm, "end": v(1674.4, 1869.4) * mm});
            skLineSegment(sketch, "E2.1.2.95", {"start": v(1291.8, 2026.95) * mm, "end": v(1307.36, 2114.8) * mm});
            skLineSegment(sketch, "E2.1.2.96", {"start": v(1291.8, 1808.51) * mm, "end": v(1307.36, 1896.36) * mm});
            skLineSegment(sketch, "E2.1.2.97", {"start": v(1229.08, 2000) * mm, "end": v(1145.22, 1969.55) * mm});
            skLineSegment(sketch, "E2.1.2.98", {"start": v(1229.08, 1563.12) * mm, "end": v(1145.22, 1532.67) * mm});
            skLineSegment(sketch, "E2.1.2.99", {"start": v(1076.92, 1590.07) * mm, "end": v(1092.48, 1677.92) * mm});
            skLineSegment(sketch, "E2.1.2.100", {"start": v(1176.34, 1708.37) * mm, "end": v(1244.64, 1650.97) * mm});
            skLineSegment(sketch, "E2.1.2.101", {"start": v(1244.64, 1650.97) * mm, "end": v(1229.08, 1563.12) * mm});
            skLineSegment(sketch, "E2.1.2.102", {"start": v(1229.08, 1781.56) * mm, "end": v(1145.22, 1751.1) * mm});
            skLineSegment(sketch, "E2.1.2.103", {"start": v(2035.88, 1926.81) * mm, "end": v(2104.18, 1869.4) * mm});
            skLineSegment(sketch, "E2.1.2.104", {"start": v(1360.1, 1532.67) * mm, "end": v(1291.8, 1590.07) * mm});
            skLineSegment(sketch, "E2.1.2.105", {"start": v(1936.46, 1590.07) * mm, "end": v(1952.02, 1677.92) * mm});
            skLineSegment(sketch, "E2.1.2.106", {"start": v(1873.73, 1781.56) * mm, "end": v(1789.87, 1751.1) * mm});
            skLineSegment(sketch, "E2.1.2.107", {"start": v(1721.57, 2026.95) * mm, "end": v(1737.13, 2114.8) * mm});
            skLineSegment(sketch, "E2.1.2.108", {"start": v(1873.73, 1563.12) * mm, "end": v(1789.87, 1532.67) * mm});
            skLineSegment(sketch, "E2.1.2.109", {"start": v(1307.36, 1896.36) * mm, "end": v(1391.22, 1926.81) * mm});
            skLineSegment(sketch, "E2.1.2.110", {"start": v(1391.22, 2145.25) * mm, "end": v(1459.52, 2087.85) * mm});
            skLineSegment(sketch, "E2.1.2.111", {"start": v(1291.8, 1590.07) * mm, "end": v(1307.36, 1677.92) * mm});
            skLineSegment(sketch, "E2.1.2.112", {"start": v(1952.02, 1677.92) * mm, "end": v(2035.88, 1708.37) * mm});
            skLineSegment(sketch, "E2.1.2.113", {"start": v(1076.92, 2026.95) * mm, "end": v(1092.48, 2114.8) * mm});
            skLineSegment(sketch, "E2.1.2.114", {"start": v(1789.87, 1532.67) * mm, "end": v(1721.57, 1590.07) * mm});
            skLineSegment(sketch, "E2.1.2.115", {"start": v(1391.22, 1926.81) * mm, "end": v(1459.52, 1869.4) * mm});
            skLineSegment(sketch, "E2.1.2.116", {"start": v(1658.85, 2000) * mm, "end": v(1574.99, 1969.55) * mm});
            skLineSegment(sketch, "E2.1.2.117", {"start": v(1459.52, 2087.85) * mm, "end": v(1443.96, 2000) * mm});
            skLineSegment(sketch, "E2.1.2.118", {"start": v(1721.57, 1808.51) * mm, "end": v(1737.13, 1896.36) * mm});
            skLineSegment(sketch, "E2.1.2.119", {"start": v(1721.57, 1590.07) * mm, "end": v(1737.13, 1677.92) * mm});
            skLineSegment(sketch, "E2.1.2.120", {"start": v(1658.85, 1781.56) * mm, "end": v(1574.99, 1751.1) * mm});
            skLineSegment(sketch, "E2.1.2.121", {"start": v(1459.52, 1869.4) * mm, "end": v(1443.96, 1781.56) * mm});
            skLineSegment(sketch, "E2.2.0.0", {"start": v(3264.96, 30.45) * mm, "end": v(3249.4, -57.4) * mm});
            skLineSegment(sketch, "E2.2.0.1", {"start": v(2237.7, -30.45) * mm, "end": v(2237.7, 188) * mm, "construction": true});
            skLineSegment(sketch, "E2.2.0.2", {"start": v(2552, 87.85) * mm, "end": v(2620.3, 30.45) * mm});
            skCircle(sketch, "E2.2.0.3", {"center": v(2751.33, 0) * mm, "radius": 77.26 * mm, "construction": true});
            skLineSegment(sketch, "E2.2.0.4", {"start": v(2735.77, 349.03) * mm, "end": v(2667.47, 406.43) * mm});
            skPoint(sketch, "E2.2.0.5", {"position": v(3207.47, 145.81) * mm});
            skPoint(sketch, "E2.2.0.6", {"position": v(2562.81, 364.25) * mm});
            skLineSegment(sketch, "E2.2.0.7", {"start": v(2337.12, 524.73) * mm, "end": v(2405.42, 467.33) * mm});
            skLineSegment(sketch, "E2.2.0.8", {"start": v(2897.91, 57.4) * mm, "end": v(2981.77, 87.85) * mm});
            skLineSegment(sketch, "E2.2.0.9", {"start": v(2735.77, 130.59) * mm, "end": v(2667.47, 188) * mm});
            skCircle(sketch, "E2.2.0.10", {"center": v(2536.44, 436.88) * mm, "radius": 77.26 * mm, "construction": true});
            skPoint(sketch, "E2.2.0.11", {"position": v(2347.93, 364.25) * mm});
            skPoint(sketch, "E2.2.0.12", {"position": v(2992.58, 145.81) * mm});
            skCircle(sketch, "E2.2.0.13", {"center": v(3181.1, 218.44) * mm, "radius": 77.26 * mm, "construction": true});
            skLineSegment(sketch, "E2.2.0.14", {"start": v(2405.42, 467.33) * mm, "end": v(2389.86, 379.48) * mm});
            skCircle(sketch, "E2.2.0.15", {"center": v(2966.21, 436.88) * mm, "radius": 77.26 * mm, "construction": true});
            skCircle(sketch, "E2.2.0.16", {"center": v(3181.1, 0) * mm, "radius": 77.26 * mm, "construction": true});
            skLineSegment(sketch, "E2.2.0.17", {"start": v(2766.89, 524.73) * mm, "end": v(2835.19, 467.33) * mm});
            skLineSegment(sketch, "E2.2.0.18", {"start": v(2667.47, -30.45) * mm, "end": v(2683.03, 57.4) * mm});
            skLineSegment(sketch, "E2.2.0.19", {"start": v(2667.47, 188) * mm, "end": v(2683.03, 275.84) * mm});
            skPoint(sketch, "E2.2.0.20", {"position": v(2992.58, -72.63) * mm});
            skPoint(sketch, "E2.2.0.21", {"position": v(2347.93, 145.81) * mm});
            skPoint(sketch, "E2.2.0.22", {"position": v(2777.7, -72.63) * mm});
            skPoint(sketch, "E2.2.0.23", {"position": v(3207.47, 364.25) * mm});
            skLineSegment(sketch, "E2.2.0.24", {"start": v(2683.03, 494.28) * mm, "end": v(2766.89, 524.73) * mm});
            skLineSegment(sketch, "E2.2.0.25", {"start": v(2735.77, -87.85) * mm, "end": v(2667.47, -30.45) * mm});
            skCircle(sketch, "E2.2.0.26", {"center": v(2536.44, 218.44) * mm, "radius": 77.26 * mm, "construction": true});
            skCircle(sketch, "E2.2.0.27", {"center": v(2536.44, 0) * mm, "radius": 77.26 * mm, "construction": true});
            skLineSegment(sketch, "E2.2.0.28", {"start": v(2835.19, 467.33) * mm, "end": v(2819.63, 379.48) * mm});
            skLineSegment(sketch, "E2.2.0.29", {"start": v(2683.03, 275.84) * mm, "end": v(2766.89, 306.3) * mm});
            skLineSegment(sketch, "E2.2.0.30", {"start": v(2683.03, 57.4) * mm, "end": v(2766.89, 87.85) * mm});
            skLineSegment(sketch, "E2.2.0.31", {"start": v(2520.88, 130.59) * mm, "end": v(2452.58, 188) * mm});
            skLineSegment(sketch, "E2.2.0.32", {"start": v(3097.24, 188) * mm, "end": v(3112.8, 275.84) * mm});
            skPoint(sketch, "E2.2.0.33", {"position": v(2562.81, -72.63) * mm});
            skPoint(sketch, "E2.2.0.34", {"position": v(2992.58, 364.25) * mm});
            skLineSegment(sketch, "E2.2.0.35", {"start": v(2950.65, 349.03) * mm, "end": v(2882.35, 406.43) * mm});
            skCircle(sketch, "E2.2.0.36", {"center": v(2966.21, 218.44) * mm, "radius": 77.26 * mm, "construction": true});
            skCircle(sketch, "E2.2.0.37", {"center": v(2966.21, 0) * mm, "radius": 77.26 * mm, "construction": true});
            skLineSegment(sketch, "E2.2.0.38", {"start": v(2766.89, 87.85) * mm, "end": v(2835.19, 30.45) * mm});
            skLineSegment(sketch, "E2.2.0.39", {"start": v(3112.8, 494.28) * mm, "end": v(3196.66, 524.73) * mm});
            skLineSegment(sketch, "E2.2.0.40", {"start": v(3112.8, 275.84) * mm, "end": v(3196.66, 306.3) * mm});
            skLineSegment(sketch, "E2.2.0.41", {"start": v(2405.42, 248.89) * mm, "end": v(2389.86, 161.04) * mm});
            skCircle(sketch, "E2.2.0.42", {"center": v(2321.56, 436.88) * mm, "radius": 77.26 * mm, "construction": true});
            skCircle(sketch, "E2.2.0.43", {"center": v(2321.56, 0) * mm, "radius": 77.26 * mm, "construction": true});
            skLineSegment(sketch, "E2.2.0.44", {"start": v(2306, -87.85) * mm, "end": v(2237.7, -30.45) * mm});
            skLineSegment(sketch, "E2.2.0.45", {"start": v(2253.26, 57.4) * mm, "end": v(2337.12, 87.85) * mm});
            skCircle(sketch, "E2.2.0.46", {"center": v(2321.56, 218.44) * mm, "radius": 77.26 * mm, "construction": true});
            skLineSegment(sketch, "E2.2.0.47", {"start": v(2306, 130.59) * mm, "end": v(2237.7, 188) * mm});
            skLineSegment(sketch, "E2.2.0.48", {"start": v(2237.7, 188) * mm, "end": v(2253.26, 275.84) * mm});
            skLineSegment(sketch, "E2.2.0.49", {"start": v(2253.26, 275.84) * mm, "end": v(2337.12, 306.3) * mm});
            skLineSegment(sketch, "E2.2.0.50", {"start": v(2337.12, 306.3) * mm, "end": v(2405.42, 248.89) * mm});
            skPoint(sketch, "E2.2.0.51", {"position": v(2777.7, 145.81) * mm});
            skLineSegment(sketch, "E2.2.0.52", {"start": v(2835.19, 248.89) * mm, "end": v(2819.63, 161.04) * mm});
            skLineSegment(sketch, "E2.2.0.53", {"start": v(2468.14, 494.28) * mm, "end": v(2552, 524.73) * mm});
            skLineSegment(sketch, "E2.2.0.54", {"start": v(3196.66, 524.73) * mm, "end": v(3264.96, 467.33) * mm});
            skLineSegment(sketch, "E2.2.0.55", {"start": v(2306, 349.03) * mm, "end": v(2237.7, 406.43) * mm});
            skLineSegment(sketch, "E2.2.0.56", {"start": v(2835.19, 30.45) * mm, "end": v(2819.63, -57.4) * mm});
            skCircle(sketch, "E2.2.0.57", {"center": v(2751.33, 436.88) * mm, "radius": 77.26 * mm, "construction": true});
            skLineSegment(sketch, "E2.2.0.58", {"start": v(3264.96, 467.33) * mm, "end": v(3249.4, 379.48) * mm});
            skLineSegment(sketch, "E2.2.0.59", {"start": v(2950.65, 130.59) * mm, "end": v(2882.35, 188) * mm});
            skPoint(sketch, "E2.2.0.60", {"position": v(2562.81, 145.81) * mm});
            skPoint(sketch, "E2.2.0.61", {"position": v(3207.47, -72.63) * mm});
            skLineSegment(sketch, "E2.2.0.62", {"start": v(2897.91, 494.28) * mm, "end": v(2981.77, 524.73) * mm});
            skCircle(sketch, "E2.2.0.63", {"center": v(2751.33, 218.44) * mm, "radius": 77.26 * mm, "construction": true});
            skLineSegment(sketch, "E2.2.0.64", {"start": v(3264.96, 248.89) * mm, "end": v(3249.4, 161.04) * mm});
            skLineSegment(sketch, "E2.2.0.65", {"start": v(2468.14, 57.4) * mm, "end": v(2552, 87.85) * mm});
            skLineSegment(sketch, "E2.2.0.66", {"start": v(2237.7, -30.45) * mm, "end": v(2452.58, -30.45) * mm, "construction": true});
            skLineSegment(sketch, "E2.2.0.67", {"start": v(3196.66, 87.85) * mm, "end": v(3264.96, 30.45) * mm});
            skLineSegment(sketch, "E2.2.0.68", {"start": v(2253.26, 494.28) * mm, "end": v(2337.12, 524.73) * mm});
            skLineSegment(sketch, "E2.2.0.69", {"start": v(2981.77, 524.73) * mm, "end": v(3050.07, 467.33) * mm});
            skCircle(sketch, "E2.2.0.70", {"center": v(3181.1, 436.88) * mm, "radius": 77.26 * mm, "construction": true});
            skPoint(sketch, "E2.2.0.71", {"position": v(2777.7, 364.25) * mm});
            skPoint(sketch, "E2.2.0.72", {"position": v(2347.93, -72.63) * mm});
            skLineSegment(sketch, "E2.2.0.73", {"start": v(2897.91, 275.84) * mm, "end": v(2981.77, 306.3) * mm});
            skLineSegment(sketch, "E2.2.0.74", {"start": v(3050.07, 467.33) * mm, "end": v(3034.51, 379.48) * mm});
            skLineSegment(sketch, "E2.2.0.75", {"start": v(3249.4, 379.48) * mm, "end": v(3165.54, 349.03) * mm});
            skLineSegment(sketch, "E2.2.0.76", {"start": v(2667.47, 406.43) * mm, "end": v(2683.03, 494.28) * mm});
            skLineSegment(sketch, "E2.2.0.77", {"start": v(2819.63, -57.4) * mm, "end": v(2735.77, -87.85) * mm});
            skLineSegment(sketch, "E2.2.0.78", {"start": v(2620.3, 30.45) * mm, "end": v(2604.74, -57.4) * mm});
            skLineSegment(sketch, "E2.2.0.79", {"start": v(2981.77, 306.3) * mm, "end": v(3050.07, 248.89) * mm});
            skLineSegment(sketch, "E2.2.0.80", {"start": v(2981.77, 87.85) * mm, "end": v(3050.07, 30.45) * mm});
            skLineSegment(sketch, "E2.2.0.81", {"start": v(2604.74, 379.48) * mm, "end": v(2520.88, 349.03) * mm});
            skLineSegment(sketch, "E2.2.0.82", {"start": v(2604.74, 161.04) * mm, "end": v(2520.88, 130.59) * mm});
            skLineSegment(sketch, "E2.2.0.83", {"start": v(3165.54, 349.03) * mm, "end": v(3097.24, 406.43) * mm});
            skLineSegment(sketch, "E2.2.0.84", {"start": v(3165.54, 130.59) * mm, "end": v(3097.24, 188) * mm});
            skLineSegment(sketch, "E2.2.0.85", {"start": v(3249.4, 161.04) * mm, "end": v(3165.54, 130.59) * mm});
            skLineSegment(sketch, "E2.2.0.86", {"start": v(3050.07, 248.89) * mm, "end": v(3034.51, 161.04) * mm});
            skLineSegment(sketch, "E2.2.0.87", {"start": v(3034.51, 379.48) * mm, "end": v(2950.65, 349.03) * mm});
            skLineSegment(sketch, "E2.2.0.88", {"start": v(3249.4, -57.4) * mm, "end": v(3165.54, -87.85) * mm});
            skLineSegment(sketch, "E2.2.0.89", {"start": v(3050.07, 30.45) * mm, "end": v(3034.51, -57.4) * mm});
            skLineSegment(sketch, "E2.2.0.90", {"start": v(2520.88, 349.03) * mm, "end": v(2452.58, 406.43) * mm});
            skLineSegment(sketch, "E2.2.0.91", {"start": v(3097.24, 406.43) * mm, "end": v(3112.8, 494.28) * mm});
            skLineSegment(sketch, "E2.2.0.92", {"start": v(2604.74, -57.4) * mm, "end": v(2520.88, -87.85) * mm});
            skLineSegment(sketch, "E2.2.0.93", {"start": v(3165.54, -87.85) * mm, "end": v(3097.24, -30.45) * mm});
            skLineSegment(sketch, "E2.2.0.94", {"start": v(2766.89, 306.3) * mm, "end": v(2835.19, 248.89) * mm});
            skLineSegment(sketch, "E2.2.0.95", {"start": v(2452.58, 406.43) * mm, "end": v(2468.14, 494.28) * mm});
            skLineSegment(sketch, "E2.2.0.96", {"start": v(2452.58, 188) * mm, "end": v(2468.14, 275.84) * mm});
            skLineSegment(sketch, "E2.2.0.97", {"start": v(2389.86, 379.48) * mm, "end": v(2306, 349.03) * mm});
            skLineSegment(sketch, "E2.2.0.98", {"start": v(2389.86, -57.4) * mm, "end": v(2306, -87.85) * mm});
            skLineSegment(sketch, "E2.2.0.99", {"start": v(2237.7, -30.45) * mm, "end": v(2253.26, 57.4) * mm});
            skLineSegment(sketch, "E2.2.0.100", {"start": v(2337.12, 87.85) * mm, "end": v(2405.42, 30.45) * mm});
            skLineSegment(sketch, "E2.2.0.101", {"start": v(2405.42, 30.45) * mm, "end": v(2389.86, -57.4) * mm});
            skLineSegment(sketch, "E2.2.0.102", {"start": v(2389.86, 161.04) * mm, "end": v(2306, 130.59) * mm});
            skLineSegment(sketch, "E2.2.0.103", {"start": v(3196.66, 306.3) * mm, "end": v(3264.96, 248.89) * mm});
            skLineSegment(sketch, "E2.2.0.104", {"start": v(2520.88, -87.85) * mm, "end": v(2452.58, -30.45) * mm});
            skLineSegment(sketch, "E2.2.0.105", {"start": v(3097.24, -30.45) * mm, "end": v(3112.8, 57.4) * mm});
            skLineSegment(sketch, "E2.2.0.106", {"start": v(3034.51, 161.04) * mm, "end": v(2950.65, 130.59) * mm});
            skLineSegment(sketch, "E2.2.0.107", {"start": v(2882.35, 406.43) * mm, "end": v(2897.91, 494.28) * mm});
            skLineSegment(sketch, "E2.2.0.108", {"start": v(3034.51, -57.4) * mm, "end": v(2950.65, -87.85) * mm});
            skLineSegment(sketch, "E2.2.0.109", {"start": v(2468.14, 275.84) * mm, "end": v(2552, 306.3) * mm});
            skLineSegment(sketch, "E2.2.0.110", {"start": v(2552, 524.73) * mm, "end": v(2620.3, 467.33) * mm});
            skLineSegment(sketch, "E2.2.0.111", {"start": v(2452.58, -30.45) * mm, "end": v(2468.14, 57.4) * mm});
            skLineSegment(sketch, "E2.2.0.112", {"start": v(3112.8, 57.4) * mm, "end": v(3196.66, 87.85) * mm});
            skLineSegment(sketch, "E2.2.0.113", {"start": v(2237.7, 406.43) * mm, "end": v(2253.26, 494.28) * mm});
            skLineSegment(sketch, "E2.2.0.114", {"start": v(2950.65, -87.85) * mm, "end": v(2882.35, -30.45) * mm});
            skLineSegment(sketch, "E2.2.0.115", {"start": v(2552, 306.3) * mm, "end": v(2620.3, 248.89) * mm});
            skLineSegment(sketch, "E2.2.0.116", {"start": v(2819.63, 379.48) * mm, "end": v(2735.77, 349.03) * mm});
            skLineSegment(sketch, "E2.2.0.117", {"start": v(2620.3, 467.33) * mm, "end": v(2604.74, 379.48) * mm});
            skLineSegment(sketch, "E2.2.0.118", {"start": v(2882.35, 188) * mm, "end": v(2897.91, 275.84) * mm});
            skLineSegment(sketch, "E2.2.0.119", {"start": v(2882.35, -30.45) * mm, "end": v(2897.91, 57.4) * mm});
            skLineSegment(sketch, "E2.2.0.120", {"start": v(2819.63, 161.04) * mm, "end": v(2735.77, 130.59) * mm});
            skLineSegment(sketch, "E2.2.0.121", {"start": v(2620.3, 248.89) * mm, "end": v(2604.74, 161.04) * mm});
            skLineSegment(sketch, "E2.2.1.0", {"start": v(3264.96, 840.7) * mm, "end": v(3249.4, 752.86) * mm});
            skLineSegment(sketch, "E2.2.1.1", {"start": v(2237.7, 779.81) * mm, "end": v(2237.7, 998.25) * mm, "construction": true});
            skLineSegment(sketch, "E2.2.1.2", {"start": v(2552, 898.11) * mm, "end": v(2620.3, 840.7) * mm});
            skCircle(sketch, "E2.2.1.3", {"center": v(2751.33, 810.26) * mm, "radius": 77.26 * mm, "construction": true});
            skLineSegment(sketch, "E2.2.1.4", {"start": v(2735.77, 1159.29) * mm, "end": v(2667.47, 1216.7) * mm});
            skPoint(sketch, "E2.2.1.5", {"position": v(3207.47, 956.07) * mm});
            skPoint(sketch, "E2.2.1.6", {"position": v(2562.81, 1174.51) * mm});
            skLineSegment(sketch, "E2.2.1.7", {"start": v(2337.12, 1335) * mm, "end": v(2405.42, 1277.59) * mm});
            skLineSegment(sketch, "E2.2.1.8", {"start": v(2897.91, 867.66) * mm, "end": v(2981.77, 898.11) * mm});
            skLineSegment(sketch, "E2.2.1.9", {"start": v(2735.77, 940.85) * mm, "end": v(2667.47, 998.25) * mm});
            skCircle(sketch, "E2.2.1.10", {"center": v(2536.44, 1247.14) * mm, "radius": 77.26 * mm, "construction": true});
            skPoint(sketch, "E2.2.1.11", {"position": v(2347.93, 1174.51) * mm});
            skPoint(sketch, "E2.2.1.12", {"position": v(2992.58, 956.07) * mm});
            skCircle(sketch, "E2.2.1.13", {"center": v(3181.1, 1028.7) * mm, "radius": 77.26 * mm, "construction": true});
            skLineSegment(sketch, "E2.2.1.14", {"start": v(2405.42, 1277.59) * mm, "end": v(2389.86, 1189.74) * mm});
            skCircle(sketch, "E2.2.1.15", {"center": v(2966.21, 1247.14) * mm, "radius": 77.26 * mm, "construction": true});
            skCircle(sketch, "E2.2.1.16", {"center": v(3181.1, 810.26) * mm, "radius": 77.26 * mm, "construction": true});
            skLineSegment(sketch, "E2.2.1.17", {"start": v(2766.89, 1335) * mm, "end": v(2835.19, 1277.59) * mm});
            skLineSegment(sketch, "E2.2.1.18", {"start": v(2667.47, 779.81) * mm, "end": v(2683.03, 867.66) * mm});
            skLineSegment(sketch, "E2.2.1.19", {"start": v(2667.47, 998.25) * mm, "end": v(2683.03, 1086.1) * mm});
            skPoint(sketch, "E2.2.1.20", {"position": v(2992.58, 737.63) * mm});
            skPoint(sketch, "E2.2.1.21", {"position": v(2347.93, 956.07) * mm});
            skPoint(sketch, "E2.2.1.22", {"position": v(2777.7, 737.63) * mm});
            skPoint(sketch, "E2.2.1.23", {"position": v(3207.47, 1174.51) * mm});
            skLineSegment(sketch, "E2.2.1.24", {"start": v(2683.03, 1304.54) * mm, "end": v(2766.89, 1335) * mm});
            skLineSegment(sketch, "E2.2.1.25", {"start": v(2735.77, 722.4) * mm, "end": v(2667.47, 779.81) * mm});
            skCircle(sketch, "E2.2.1.26", {"center": v(2536.44, 1028.7) * mm, "radius": 77.26 * mm, "construction": true});
            skCircle(sketch, "E2.2.1.27", {"center": v(2536.44, 810.26) * mm, "radius": 77.26 * mm, "construction": true});
            skLineSegment(sketch, "E2.2.1.28", {"start": v(2835.19, 1277.59) * mm, "end": v(2819.63, 1189.74) * mm});
            skLineSegment(sketch, "E2.2.1.29", {"start": v(2683.03, 1086.1) * mm, "end": v(2766.89, 1116.55) * mm});
            skLineSegment(sketch, "E2.2.1.30", {"start": v(2683.03, 867.66) * mm, "end": v(2766.89, 898.11) * mm});
            skLineSegment(sketch, "E2.2.1.31", {"start": v(2520.88, 940.85) * mm, "end": v(2452.58, 998.25) * mm});
            skLineSegment(sketch, "E2.2.1.32", {"start": v(3097.24, 998.25) * mm, "end": v(3112.8, 1086.1) * mm});
            skPoint(sketch, "E2.2.1.33", {"position": v(2562.81, 737.63) * mm});
            skPoint(sketch, "E2.2.1.34", {"position": v(2992.58, 1174.51) * mm});
            skLineSegment(sketch, "E2.2.1.35", {"start": v(2950.65, 1159.29) * mm, "end": v(2882.35, 1216.7) * mm});
            skCircle(sketch, "E2.2.1.36", {"center": v(2966.21, 1028.7) * mm, "radius": 77.26 * mm, "construction": true});
            skCircle(sketch, "E2.2.1.37", {"center": v(2966.21, 810.26) * mm, "radius": 77.26 * mm, "construction": true});
            skLineSegment(sketch, "E2.2.1.38", {"start": v(2766.89, 898.11) * mm, "end": v(2835.19, 840.7) * mm});
            skLineSegment(sketch, "E2.2.1.39", {"start": v(3112.8, 1304.54) * mm, "end": v(3196.66, 1335) * mm});
            skLineSegment(sketch, "E2.2.1.40", {"start": v(3112.8, 1086.1) * mm, "end": v(3196.66, 1116.55) * mm});
            skLineSegment(sketch, "E2.2.1.41", {"start": v(2405.42, 1059.15) * mm, "end": v(2389.86, 971.3) * mm});
            skCircle(sketch, "E2.2.1.42", {"center": v(2321.56, 1247.14) * mm, "radius": 77.26 * mm, "construction": true});
            skCircle(sketch, "E2.2.1.43", {"center": v(2321.56, 810.26) * mm, "radius": 77.26 * mm, "construction": true});
            skLineSegment(sketch, "E2.2.1.44", {"start": v(2306, 722.4) * mm, "end": v(2237.7, 779.81) * mm});
            skLineSegment(sketch, "E2.2.1.45", {"start": v(2253.26, 867.66) * mm, "end": v(2337.12, 898.11) * mm});
            skCircle(sketch, "E2.2.1.46", {"center": v(2321.56, 1028.7) * mm, "radius": 77.26 * mm, "construction": true});
            skLineSegment(sketch, "E2.2.1.47", {"start": v(2306, 940.85) * mm, "end": v(2237.7, 998.25) * mm});
            skLineSegment(sketch, "E2.2.1.48", {"start": v(2237.7, 998.25) * mm, "end": v(2253.26, 1086.1) * mm});
            skLineSegment(sketch, "E2.2.1.49", {"start": v(2253.26, 1086.1) * mm, "end": v(2337.12, 1116.55) * mm});
            skLineSegment(sketch, "E2.2.1.50", {"start": v(2337.12, 1116.55) * mm, "end": v(2405.42, 1059.15) * mm});
            skPoint(sketch, "E2.2.1.51", {"position": v(2777.7, 956.07) * mm});
            skLineSegment(sketch, "E2.2.1.52", {"start": v(2835.19, 1059.15) * mm, "end": v(2819.63, 971.3) * mm});
            skLineSegment(sketch, "E2.2.1.53", {"start": v(2468.14, 1304.54) * mm, "end": v(2552, 1335) * mm});
            skLineSegment(sketch, "E2.2.1.54", {"start": v(3196.66, 1335) * mm, "end": v(3264.96, 1277.59) * mm});
            skLineSegment(sketch, "E2.2.1.55", {"start": v(2306, 1159.29) * mm, "end": v(2237.7, 1216.7) * mm});
            skLineSegment(sketch, "E2.2.1.56", {"start": v(2835.19, 840.7) * mm, "end": v(2819.63, 752.86) * mm});
            skCircle(sketch, "E2.2.1.57", {"center": v(2751.33, 1247.14) * mm, "radius": 77.26 * mm, "construction": true});
            skLineSegment(sketch, "E2.2.1.58", {"start": v(3264.96, 1277.59) * mm, "end": v(3249.4, 1189.74) * mm});
            skLineSegment(sketch, "E2.2.1.59", {"start": v(2950.65, 940.85) * mm, "end": v(2882.35, 998.25) * mm});
            skPoint(sketch, "E2.2.1.60", {"position": v(2562.81, 956.07) * mm});
            skPoint(sketch, "E2.2.1.61", {"position": v(3207.47, 737.63) * mm});
            skLineSegment(sketch, "E2.2.1.62", {"start": v(2897.91, 1304.54) * mm, "end": v(2981.77, 1335) * mm});
            skCircle(sketch, "E2.2.1.63", {"center": v(2751.33, 1028.7) * mm, "radius": 77.26 * mm, "construction": true});
            skLineSegment(sketch, "E2.2.1.64", {"start": v(3264.96, 1059.15) * mm, "end": v(3249.4, 971.3) * mm});
            skLineSegment(sketch, "E2.2.1.65", {"start": v(2468.14, 867.66) * mm, "end": v(2552, 898.11) * mm});
            skLineSegment(sketch, "E2.2.1.66", {"start": v(2237.7, 779.81) * mm, "end": v(2452.58, 779.81) * mm, "construction": true});
            skLineSegment(sketch, "E2.2.1.67", {"start": v(3196.66, 898.11) * mm, "end": v(3264.96, 840.7) * mm});
            skLineSegment(sketch, "E2.2.1.68", {"start": v(2253.26, 1304.54) * mm, "end": v(2337.12, 1335) * mm});
            skLineSegment(sketch, "E2.2.1.69", {"start": v(2981.77, 1335) * mm, "end": v(3050.07, 1277.59) * mm});
            skCircle(sketch, "E2.2.1.70", {"center": v(3181.1, 1247.14) * mm, "radius": 77.26 * mm, "construction": true});
            skPoint(sketch, "E2.2.1.71", {"position": v(2777.7, 1174.51) * mm});
            skPoint(sketch, "E2.2.1.72", {"position": v(2347.93, 737.63) * mm});
            skLineSegment(sketch, "E2.2.1.73", {"start": v(2897.91, 1086.1) * mm, "end": v(2981.77, 1116.55) * mm});
            skLineSegment(sketch, "E2.2.1.74", {"start": v(3050.07, 1277.59) * mm, "end": v(3034.51, 1189.74) * mm});
            skLineSegment(sketch, "E2.2.1.75", {"start": v(3249.4, 1189.74) * mm, "end": v(3165.54, 1159.29) * mm});
            skLineSegment(sketch, "E2.2.1.76", {"start": v(2667.47, 1216.7) * mm, "end": v(2683.03, 1304.54) * mm});
            skLineSegment(sketch, "E2.2.1.77", {"start": v(2819.63, 752.86) * mm, "end": v(2735.77, 722.4) * mm});
            skLineSegment(sketch, "E2.2.1.78", {"start": v(2620.3, 840.7) * mm, "end": v(2604.74, 752.86) * mm});
            skLineSegment(sketch, "E2.2.1.79", {"start": v(2981.77, 1116.55) * mm, "end": v(3050.07, 1059.15) * mm});
            skLineSegment(sketch, "E2.2.1.80", {"start": v(2981.77, 898.11) * mm, "end": v(3050.07, 840.7) * mm});
            skLineSegment(sketch, "E2.2.1.81", {"start": v(2604.74, 1189.74) * mm, "end": v(2520.88, 1159.29) * mm});
            skLineSegment(sketch, "E2.2.1.82", {"start": v(2604.74, 971.3) * mm, "end": v(2520.88, 940.85) * mm});
            skLineSegment(sketch, "E2.2.1.83", {"start": v(3165.54, 1159.29) * mm, "end": v(3097.24, 1216.7) * mm});
            skLineSegment(sketch, "E2.2.1.84", {"start": v(3165.54, 940.85) * mm, "end": v(3097.24, 998.25) * mm});
            skLineSegment(sketch, "E2.2.1.85", {"start": v(3249.4, 971.3) * mm, "end": v(3165.54, 940.85) * mm});
            skLineSegment(sketch, "E2.2.1.86", {"start": v(3050.07, 1059.15) * mm, "end": v(3034.51, 971.3) * mm});
            skLineSegment(sketch, "E2.2.1.87", {"start": v(3034.51, 1189.74) * mm, "end": v(2950.65, 1159.29) * mm});
            skLineSegment(sketch, "E2.2.1.88", {"start": v(3249.4, 752.86) * mm, "end": v(3165.54, 722.4) * mm});
            skLineSegment(sketch, "E2.2.1.89", {"start": v(3050.07, 840.7) * mm, "end": v(3034.51, 752.86) * mm});
            skLineSegment(sketch, "E2.2.1.90", {"start": v(2520.88, 1159.29) * mm, "end": v(2452.58, 1216.7) * mm});
            skLineSegment(sketch, "E2.2.1.91", {"start": v(3097.24, 1216.7) * mm, "end": v(3112.8, 1304.54) * mm});
            skLineSegment(sketch, "E2.2.1.92", {"start": v(2604.74, 752.86) * mm, "end": v(2520.88, 722.4) * mm});
            skLineSegment(sketch, "E2.2.1.93", {"start": v(3165.54, 722.4) * mm, "end": v(3097.24, 779.81) * mm});
            skLineSegment(sketch, "E2.2.1.94", {"start": v(2766.89, 1116.55) * mm, "end": v(2835.19, 1059.15) * mm});
            skLineSegment(sketch, "E2.2.1.95", {"start": v(2452.58, 1216.7) * mm, "end": v(2468.14, 1304.54) * mm});
            skLineSegment(sketch, "E2.2.1.96", {"start": v(2452.58, 998.25) * mm, "end": v(2468.14, 1086.1) * mm});
            skLineSegment(sketch, "E2.2.1.97", {"start": v(2389.86, 1189.74) * mm, "end": v(2306, 1159.29) * mm});
            skLineSegment(sketch, "E2.2.1.98", {"start": v(2389.86, 752.86) * mm, "end": v(2306, 722.4) * mm});
            skLineSegment(sketch, "E2.2.1.99", {"start": v(2237.7, 779.81) * mm, "end": v(2253.26, 867.66) * mm});
            skLineSegment(sketch, "E2.2.1.100", {"start": v(2337.12, 898.11) * mm, "end": v(2405.42, 840.7) * mm});
            skLineSegment(sketch, "E2.2.1.101", {"start": v(2405.42, 840.7) * mm, "end": v(2389.86, 752.86) * mm});
            skLineSegment(sketch, "E2.2.1.102", {"start": v(2389.86, 971.3) * mm, "end": v(2306, 940.85) * mm});
            skLineSegment(sketch, "E2.2.1.103", {"start": v(3196.66, 1116.55) * mm, "end": v(3264.96, 1059.15) * mm});
            skLineSegment(sketch, "E2.2.1.104", {"start": v(2520.88, 722.4) * mm, "end": v(2452.58, 779.81) * mm});
            skLineSegment(sketch, "E2.2.1.105", {"start": v(3097.24, 779.81) * mm, "end": v(3112.8, 867.66) * mm});
            skLineSegment(sketch, "E2.2.1.106", {"start": v(3034.51, 971.3) * mm, "end": v(2950.65, 940.85) * mm});
            skLineSegment(sketch, "E2.2.1.107", {"start": v(2882.35, 1216.7) * mm, "end": v(2897.91, 1304.54) * mm});
            skLineSegment(sketch, "E2.2.1.108", {"start": v(3034.51, 752.86) * mm, "end": v(2950.65, 722.4) * mm});
            skLineSegment(sketch, "E2.2.1.109", {"start": v(2468.14, 1086.1) * mm, "end": v(2552, 1116.55) * mm});
            skLineSegment(sketch, "E2.2.1.110", {"start": v(2552, 1335) * mm, "end": v(2620.3, 1277.59) * mm});
            skLineSegment(sketch, "E2.2.1.111", {"start": v(2452.58, 779.81) * mm, "end": v(2468.14, 867.66) * mm});
            skLineSegment(sketch, "E2.2.1.112", {"start": v(3112.8, 867.66) * mm, "end": v(3196.66, 898.11) * mm});
            skLineSegment(sketch, "E2.2.1.113", {"start": v(2237.7, 1216.7) * mm, "end": v(2253.26, 1304.54) * mm});
            skLineSegment(sketch, "E2.2.1.114", {"start": v(2950.65, 722.4) * mm, "end": v(2882.35, 779.81) * mm});
            skLineSegment(sketch, "E2.2.1.115", {"start": v(2552, 1116.55) * mm, "end": v(2620.3, 1059.15) * mm});
            skLineSegment(sketch, "E2.2.1.116", {"start": v(2819.63, 1189.74) * mm, "end": v(2735.77, 1159.29) * mm});
            skLineSegment(sketch, "E2.2.1.117", {"start": v(2620.3, 1277.59) * mm, "end": v(2604.74, 1189.74) * mm});
            skLineSegment(sketch, "E2.2.1.118", {"start": v(2882.35, 998.25) * mm, "end": v(2897.91, 1086.1) * mm});
            skLineSegment(sketch, "E2.2.1.119", {"start": v(2882.35, 779.81) * mm, "end": v(2897.91, 867.66) * mm});
            skLineSegment(sketch, "E2.2.1.120", {"start": v(2819.63, 971.3) * mm, "end": v(2735.77, 940.85) * mm});
            skLineSegment(sketch, "E2.2.1.121", {"start": v(2620.3, 1059.15) * mm, "end": v(2604.74, 971.3) * mm});
            skLineSegment(sketch, "E2.2.2.0", {"start": v(3264.96, 1650.97) * mm, "end": v(3249.4, 1563.12) * mm});
            skLineSegment(sketch, "E2.2.2.1", {"start": v(2237.7, 1590.07) * mm, "end": v(2237.7, 1808.51) * mm, "construction": true});
            skLineSegment(sketch, "E2.2.2.2", {"start": v(2552, 1708.37) * mm, "end": v(2620.3, 1650.97) * mm});
            skCircle(sketch, "E2.2.2.3", {"center": v(2751.33, 1620.52) * mm, "radius": 77.26 * mm, "construction": true});
            skLineSegment(sketch, "E2.2.2.4", {"start": v(2735.77, 1969.55) * mm, "end": v(2667.47, 2026.95) * mm});
            skPoint(sketch, "E2.2.2.5", {"position": v(3207.47, 1766.33) * mm});
            skPoint(sketch, "E2.2.2.6", {"position": v(2562.81, 1984.77) * mm});
            skLineSegment(sketch, "E2.2.2.7", {"start": v(2337.12, 2145.25) * mm, "end": v(2405.42, 2087.85) * mm});
            skLineSegment(sketch, "E2.2.2.8", {"start": v(2897.91, 1677.92) * mm, "end": v(2981.77, 1708.37) * mm});
            skLineSegment(sketch, "E2.2.2.9", {"start": v(2735.77, 1751.1) * mm, "end": v(2667.47, 1808.51) * mm});
            skCircle(sketch, "E2.2.2.10", {"center": v(2536.44, 2057.4) * mm, "radius": 77.26 * mm, "construction": true});
            skPoint(sketch, "E2.2.2.11", {"position": v(2347.93, 1984.77) * mm});
            skPoint(sketch, "E2.2.2.12", {"position": v(2992.58, 1766.33) * mm});
            skCircle(sketch, "E2.2.2.13", {"center": v(3181.1, 1838.96) * mm, "radius": 77.26 * mm, "construction": true});
            skLineSegment(sketch, "E2.2.2.14", {"start": v(2405.42, 2087.85) * mm, "end": v(2389.86, 2000) * mm});
            skCircle(sketch, "E2.2.2.15", {"center": v(2966.21, 2057.4) * mm, "radius": 77.26 * mm, "construction": true});
            skCircle(sketch, "E2.2.2.16", {"center": v(3181.1, 1620.52) * mm, "radius": 77.26 * mm, "construction": true});
            skLineSegment(sketch, "E2.2.2.17", {"start": v(2766.89, 2145.25) * mm, "end": v(2835.19, 2087.85) * mm});
            skLineSegment(sketch, "E2.2.2.18", {"start": v(2667.47, 1590.07) * mm, "end": v(2683.03, 1677.92) * mm});
            skLineSegment(sketch, "E2.2.2.19", {"start": v(2667.47, 1808.51) * mm, "end": v(2683.03, 1896.36) * mm});
            skPoint(sketch, "E2.2.2.20", {"position": v(2992.58, 1547.9) * mm});
            skPoint(sketch, "E2.2.2.21", {"position": v(2347.93, 1766.33) * mm});
            skPoint(sketch, "E2.2.2.22", {"position": v(2777.7, 1547.9) * mm});
            skPoint(sketch, "E2.2.2.23", {"position": v(3207.47, 1984.77) * mm});
            skLineSegment(sketch, "E2.2.2.24", {"start": v(2683.03, 2114.8) * mm, "end": v(2766.89, 2145.25) * mm});
            skLineSegment(sketch, "E2.2.2.25", {"start": v(2735.77, 1532.67) * mm, "end": v(2667.47, 1590.07) * mm});
            skCircle(sketch, "E2.2.2.26", {"center": v(2536.44, 1838.96) * mm, "radius": 77.26 * mm, "construction": true});
            skCircle(sketch, "E2.2.2.27", {"center": v(2536.44, 1620.52) * mm, "radius": 77.26 * mm, "construction": true});
            skLineSegment(sketch, "E2.2.2.28", {"start": v(2835.19, 2087.85) * mm, "end": v(2819.63, 2000) * mm});
            skLineSegment(sketch, "E2.2.2.29", {"start": v(2683.03, 1896.36) * mm, "end": v(2766.89, 1926.81) * mm});
            skLineSegment(sketch, "E2.2.2.30", {"start": v(2683.03, 1677.92) * mm, "end": v(2766.89, 1708.37) * mm});
            skLineSegment(sketch, "E2.2.2.31", {"start": v(2520.88, 1751.1) * mm, "end": v(2452.58, 1808.51) * mm});
            skLineSegment(sketch, "E2.2.2.32", {"start": v(3097.24, 1808.51) * mm, "end": v(3112.8, 1896.36) * mm});
            skPoint(sketch, "E2.2.2.33", {"position": v(2562.81, 1547.9) * mm});
            skPoint(sketch, "E2.2.2.34", {"position": v(2992.58, 1984.77) * mm});
            skLineSegment(sketch, "E2.2.2.35", {"start": v(2950.65, 1969.55) * mm, "end": v(2882.35, 2026.95) * mm});
            skCircle(sketch, "E2.2.2.36", {"center": v(2966.21, 1838.96) * mm, "radius": 77.26 * mm, "construction": true});
            skCircle(sketch, "E2.2.2.37", {"center": v(2966.21, 1620.52) * mm, "radius": 77.26 * mm, "construction": true});
            skLineSegment(sketch, "E2.2.2.38", {"start": v(2766.89, 1708.37) * mm, "end": v(2835.19, 1650.97) * mm});
            skLineSegment(sketch, "E2.2.2.39", {"start": v(3112.8, 2114.8) * mm, "end": v(3196.66, 2145.25) * mm});
            skLineSegment(sketch, "E2.2.2.40", {"start": v(3112.8, 1896.36) * mm, "end": v(3196.66, 1926.81) * mm});
            skLineSegment(sketch, "E2.2.2.41", {"start": v(2405.42, 1869.4) * mm, "end": v(2389.86, 1781.56) * mm});
            skCircle(sketch, "E2.2.2.42", {"center": v(2321.56, 2057.4) * mm, "radius": 77.26 * mm, "construction": true});
            skCircle(sketch, "E2.2.2.43", {"center": v(2321.56, 1620.52) * mm, "radius": 77.26 * mm, "construction": true});
            skLineSegment(sketch, "E2.2.2.44", {"start": v(2306, 1532.67) * mm, "end": v(2237.7, 1590.07) * mm});
            skLineSegment(sketch, "E2.2.2.45", {"start": v(2253.26, 1677.92) * mm, "end": v(2337.12, 1708.37) * mm});
            skCircle(sketch, "E2.2.2.46", {"center": v(2321.56, 1838.96) * mm, "radius": 77.26 * mm, "construction": true});
            skLineSegment(sketch, "E2.2.2.47", {"start": v(2306, 1751.1) * mm, "end": v(2237.7, 1808.51) * mm});
            skLineSegment(sketch, "E2.2.2.48", {"start": v(2237.7, 1808.51) * mm, "end": v(2253.26, 1896.36) * mm});
            skLineSegment(sketch, "E2.2.2.49", {"start": v(2253.26, 1896.36) * mm, "end": v(2337.12, 1926.81) * mm});
            skLineSegment(sketch, "E2.2.2.50", {"start": v(2337.12, 1926.81) * mm, "end": v(2405.42, 1869.4) * mm});
            skPoint(sketch, "E2.2.2.51", {"position": v(2777.7, 1766.33) * mm});
            skLineSegment(sketch, "E2.2.2.52", {"start": v(2835.19, 1869.4) * mm, "end": v(2819.63, 1781.56) * mm});
            skLineSegment(sketch, "E2.2.2.53", {"start": v(2468.14, 2114.8) * mm, "end": v(2552, 2145.25) * mm});
            skLineSegment(sketch, "E2.2.2.54", {"start": v(3196.66, 2145.25) * mm, "end": v(3264.96, 2087.85) * mm});
            skLineSegment(sketch, "E2.2.2.55", {"start": v(2306, 1969.55) * mm, "end": v(2237.7, 2026.95) * mm});
            skLineSegment(sketch, "E2.2.2.56", {"start": v(2835.19, 1650.97) * mm, "end": v(2819.63, 1563.12) * mm});
            skCircle(sketch, "E2.2.2.57", {"center": v(2751.33, 2057.4) * mm, "radius": 77.26 * mm, "construction": true});
            skLineSegment(sketch, "E2.2.2.58", {"start": v(3264.96, 2087.85) * mm, "end": v(3249.4, 2000) * mm});
            skLineSegment(sketch, "E2.2.2.59", {"start": v(2950.65, 1751.1) * mm, "end": v(2882.35, 1808.51) * mm});
            skPoint(sketch, "E2.2.2.60", {"position": v(2562.81, 1766.33) * mm});
            skPoint(sketch, "E2.2.2.61", {"position": v(3207.47, 1547.9) * mm});
            skLineSegment(sketch, "E2.2.2.62", {"start": v(2897.91, 2114.8) * mm, "end": v(2981.77, 2145.25) * mm});
            skCircle(sketch, "E2.2.2.63", {"center": v(2751.33, 1838.96) * mm, "radius": 77.26 * mm, "construction": true});
            skLineSegment(sketch, "E2.2.2.64", {"start": v(3264.96, 1869.4) * mm, "end": v(3249.4, 1781.56) * mm});
            skLineSegment(sketch, "E2.2.2.65", {"start": v(2468.14, 1677.92) * mm, "end": v(2552, 1708.37) * mm});
            skLineSegment(sketch, "E2.2.2.66", {"start": v(2237.7, 1590.07) * mm, "end": v(2452.58, 1590.07) * mm, "construction": true});
            skLineSegment(sketch, "E2.2.2.67", {"start": v(3196.66, 1708.37) * mm, "end": v(3264.96, 1650.97) * mm});
            skLineSegment(sketch, "E2.2.2.68", {"start": v(2253.26, 2114.8) * mm, "end": v(2337.12, 2145.25) * mm});
            skLineSegment(sketch, "E2.2.2.69", {"start": v(2981.77, 2145.25) * mm, "end": v(3050.07, 2087.85) * mm});
            skCircle(sketch, "E2.2.2.70", {"center": v(3181.1, 2057.4) * mm, "radius": 77.26 * mm, "construction": true});
            skPoint(sketch, "E2.2.2.71", {"position": v(2777.7, 1984.77) * mm});
            skPoint(sketch, "E2.2.2.72", {"position": v(2347.93, 1547.9) * mm});
            skLineSegment(sketch, "E2.2.2.73", {"start": v(2897.91, 1896.36) * mm, "end": v(2981.77, 1926.81) * mm});
            skLineSegment(sketch, "E2.2.2.74", {"start": v(3050.07, 2087.85) * mm, "end": v(3034.51, 2000) * mm});
            skLineSegment(sketch, "E2.2.2.75", {"start": v(3249.4, 2000) * mm, "end": v(3165.54, 1969.55) * mm});
            skLineSegment(sketch, "E2.2.2.76", {"start": v(2667.47, 2026.95) * mm, "end": v(2683.03, 2114.8) * mm});
            skLineSegment(sketch, "E2.2.2.77", {"start": v(2819.63, 1563.12) * mm, "end": v(2735.77, 1532.67) * mm});
            skLineSegment(sketch, "E2.2.2.78", {"start": v(2620.3, 1650.97) * mm, "end": v(2604.74, 1563.12) * mm});
            skLineSegment(sketch, "E2.2.2.79", {"start": v(2981.77, 1926.81) * mm, "end": v(3050.07, 1869.4) * mm});
            skLineSegment(sketch, "E2.2.2.80", {"start": v(2981.77, 1708.37) * mm, "end": v(3050.07, 1650.97) * mm});
            skLineSegment(sketch, "E2.2.2.81", {"start": v(2604.74, 2000) * mm, "end": v(2520.88, 1969.55) * mm});
            skLineSegment(sketch, "E2.2.2.82", {"start": v(2604.74, 1781.56) * mm, "end": v(2520.88, 1751.1) * mm});
            skLineSegment(sketch, "E2.2.2.83", {"start": v(3165.54, 1969.55) * mm, "end": v(3097.24, 2026.95) * mm});
            skLineSegment(sketch, "E2.2.2.84", {"start": v(3165.54, 1751.1) * mm, "end": v(3097.24, 1808.51) * mm});
            skLineSegment(sketch, "E2.2.2.85", {"start": v(3249.4, 1781.56) * mm, "end": v(3165.54, 1751.1) * mm});
            skLineSegment(sketch, "E2.2.2.86", {"start": v(3050.07, 1869.4) * mm, "end": v(3034.51, 1781.56) * mm});
            skLineSegment(sketch, "E2.2.2.87", {"start": v(3034.51, 2000) * mm, "end": v(2950.65, 1969.55) * mm});
            skLineSegment(sketch, "E2.2.2.88", {"start": v(3249.4, 1563.12) * mm, "end": v(3165.54, 1532.67) * mm});
            skLineSegment(sketch, "E2.2.2.89", {"start": v(3050.07, 1650.97) * mm, "end": v(3034.51, 1563.12) * mm});
            skLineSegment(sketch, "E2.2.2.90", {"start": v(2520.88, 1969.55) * mm, "end": v(2452.58, 2026.95) * mm});
            skLineSegment(sketch, "E2.2.2.91", {"start": v(3097.24, 2026.95) * mm, "end": v(3112.8, 2114.8) * mm});
            skLineSegment(sketch, "E2.2.2.92", {"start": v(2604.74, 1563.12) * mm, "end": v(2520.88, 1532.67) * mm});
            skLineSegment(sketch, "E2.2.2.93", {"start": v(3165.54, 1532.67) * mm, "end": v(3097.24, 1590.07) * mm});
            skLineSegment(sketch, "E2.2.2.94", {"start": v(2766.89, 1926.81) * mm, "end": v(2835.19, 1869.4) * mm});
            skLineSegment(sketch, "E2.2.2.95", {"start": v(2452.58, 2026.95) * mm, "end": v(2468.14, 2114.8) * mm});
            skLineSegment(sketch, "E2.2.2.96", {"start": v(2452.58, 1808.51) * mm, "end": v(2468.14, 1896.36) * mm});
            skLineSegment(sketch, "E2.2.2.97", {"start": v(2389.86, 2000) * mm, "end": v(2306, 1969.55) * mm});
            skLineSegment(sketch, "E2.2.2.98", {"start": v(2389.86, 1563.12) * mm, "end": v(2306, 1532.67) * mm});
            skLineSegment(sketch, "E2.2.2.99", {"start": v(2237.7, 1590.07) * mm, "end": v(2253.26, 1677.92) * mm});
            skLineSegment(sketch, "E2.2.2.100", {"start": v(2337.12, 1708.37) * mm, "end": v(2405.42, 1650.97) * mm});
            skLineSegment(sketch, "E2.2.2.101", {"start": v(2405.42, 1650.97) * mm, "end": v(2389.86, 1563.12) * mm});
            skLineSegment(sketch, "E2.2.2.102", {"start": v(2389.86, 1781.56) * mm, "end": v(2306, 1751.1) * mm});
            skLineSegment(sketch, "E2.2.2.103", {"start": v(3196.66, 1926.81) * mm, "end": v(3264.96, 1869.4) * mm});
            skLineSegment(sketch, "E2.2.2.104", {"start": v(2520.88, 1532.67) * mm, "end": v(2452.58, 1590.07) * mm});
            skLineSegment(sketch, "E2.2.2.105", {"start": v(3097.24, 1590.07) * mm, "end": v(3112.8, 1677.92) * mm});
            skLineSegment(sketch, "E2.2.2.106", {"start": v(3034.51, 1781.56) * mm, "end": v(2950.65, 1751.1) * mm});
            skLineSegment(sketch, "E2.2.2.107", {"start": v(2882.35, 2026.95) * mm, "end": v(2897.91, 2114.8) * mm});
            skLineSegment(sketch, "E2.2.2.108", {"start": v(3034.51, 1563.12) * mm, "end": v(2950.65, 1532.67) * mm});
            skLineSegment(sketch, "E2.2.2.109", {"start": v(2468.14, 1896.36) * mm, "end": v(2552, 1926.81) * mm});
            skLineSegment(sketch, "E2.2.2.110", {"start": v(2552, 2145.25) * mm, "end": v(2620.3, 2087.85) * mm});
            skLineSegment(sketch, "E2.2.2.111", {"start": v(2452.58, 1590.07) * mm, "end": v(2468.14, 1677.92) * mm});
            skLineSegment(sketch, "E2.2.2.112", {"start": v(3112.8, 1677.92) * mm, "end": v(3196.66, 1708.37) * mm});
            skLineSegment(sketch, "E2.2.2.113", {"start": v(2237.7, 2026.95) * mm, "end": v(2253.26, 2114.8) * mm});
            skLineSegment(sketch, "E2.2.2.114", {"start": v(2950.65, 1532.67) * mm, "end": v(2882.35, 1590.07) * mm});
            skLineSegment(sketch, "E2.2.2.115", {"start": v(2552, 1926.81) * mm, "end": v(2620.3, 1869.4) * mm});
            skLineSegment(sketch, "E2.2.2.116", {"start": v(2819.63, 2000) * mm, "end": v(2735.77, 1969.55) * mm});
            skLineSegment(sketch, "E2.2.2.117", {"start": v(2620.3, 2087.85) * mm, "end": v(2604.74, 2000) * mm});
            skLineSegment(sketch, "E2.2.2.118", {"start": v(2882.35, 1808.51) * mm, "end": v(2897.91, 1896.36) * mm});
            skLineSegment(sketch, "E2.2.2.119", {"start": v(2882.35, 1590.07) * mm, "end": v(2897.91, 1677.92) * mm});
            skLineSegment(sketch, "E2.2.2.120", {"start": v(2819.63, 1781.56) * mm, "end": v(2735.77, 1751.1) * mm});
            skLineSegment(sketch, "E2.2.2.121", {"start": v(2620.3, 1869.4) * mm, "end": v(2604.74, 1781.56) * mm});
            skLineSegment(sketch, "E2.3.0.0", {"start": v(4425.74, 30.45) * mm, "end": v(4410.18, -57.4) * mm});
            skLineSegment(sketch, "E2.3.0.1", {"start": v(3398.48, -30.45) * mm, "end": v(3398.48, 188) * mm, "construction": true});
            skLineSegment(sketch, "E2.3.0.2", {"start": v(3712.78, 87.85) * mm, "end": v(3781.08, 30.45) * mm});
            skCircle(sketch, "E2.3.0.3", {"center": v(3912.1, 0) * mm, "radius": 77.26 * mm, "construction": true});
            skLineSegment(sketch, "E2.3.0.4", {"start": v(3896.55, 349.03) * mm, "end": v(3828.25, 406.43) * mm});
            skPoint(sketch, "E2.3.0.5", {"position": v(4368.25, 145.81) * mm});
            skPoint(sketch, "E2.3.0.6", {"position": v(3723.6, 364.25) * mm});
            skLineSegment(sketch, "E2.3.0.7", {"start": v(3497.9, 524.73) * mm, "end": v(3566.2, 467.33) * mm});
            skLineSegment(sketch, "E2.3.0.8", {"start": v(4058.7, 57.4) * mm, "end": v(4142.55, 87.85) * mm});
            skLineSegment(sketch, "E2.3.0.9", {"start": v(3896.55, 130.59) * mm, "end": v(3828.25, 188) * mm});
            skCircle(sketch, "E2.3.0.10", {"center": v(3697.22, 436.88) * mm, "radius": 77.26 * mm, "construction": true});
            skPoint(sketch, "E2.3.0.11", {"position": v(3508.7, 364.25) * mm});
            skPoint(sketch, "E2.3.0.12", {"position": v(4153.36, 145.81) * mm});
            skCircle(sketch, "E2.3.0.13", {"center": v(4341.88, 218.44) * mm, "radius": 77.26 * mm, "construction": true});
            skLineSegment(sketch, "E2.3.0.14", {"start": v(3566.2, 467.33) * mm, "end": v(3550.64, 379.48) * mm});
            skCircle(sketch, "E2.3.0.15", {"center": v(4127, 436.88) * mm, "radius": 77.26 * mm, "construction": true});
            skCircle(sketch, "E2.3.0.16", {"center": v(4341.88, 0) * mm, "radius": 77.26 * mm, "construction": true});
            skLineSegment(sketch, "E2.3.0.17", {"start": v(3927.67, 524.73) * mm, "end": v(3995.97, 467.33) * mm});
            skLineSegment(sketch, "E2.3.0.18", {"start": v(3828.25, -30.45) * mm, "end": v(3843.8, 57.4) * mm});
            skLineSegment(sketch, "E2.3.0.19", {"start": v(3828.25, 188) * mm, "end": v(3843.8, 275.84) * mm});
            skPoint(sketch, "E2.3.0.20", {"position": v(4153.36, -72.63) * mm});
            skPoint(sketch, "E2.3.0.21", {"position": v(3508.7, 145.81) * mm});
            skPoint(sketch, "E2.3.0.22", {"position": v(3938.48, -72.63) * mm});
            skPoint(sketch, "E2.3.0.23", {"position": v(4368.25, 364.25) * mm});
            skLineSegment(sketch, "E2.3.0.24", {"start": v(3843.8, 494.28) * mm, "end": v(3927.67, 524.73) * mm});
            skLineSegment(sketch, "E2.3.0.25", {"start": v(3896.55, -87.85) * mm, "end": v(3828.25, -30.45) * mm});
            skCircle(sketch, "E2.3.0.26", {"center": v(3697.22, 218.44) * mm, "radius": 77.26 * mm, "construction": true});
            skCircle(sketch, "E2.3.0.27", {"center": v(3697.22, 0) * mm, "radius": 77.26 * mm, "construction": true});
            skLineSegment(sketch, "E2.3.0.28", {"start": v(3995.97, 467.33) * mm, "end": v(3980.4, 379.48) * mm});
            skLineSegment(sketch, "E2.3.0.29", {"start": v(3843.8, 275.84) * mm, "end": v(3927.67, 306.3) * mm});
            skLineSegment(sketch, "E2.3.0.30", {"start": v(3843.8, 57.4) * mm, "end": v(3927.67, 87.85) * mm});
            skLineSegment(sketch, "E2.3.0.31", {"start": v(3681.66, 130.59) * mm, "end": v(3613.36, 188) * mm});
            skLineSegment(sketch, "E2.3.0.32", {"start": v(4258.02, 188) * mm, "end": v(4273.58, 275.84) * mm});
            skPoint(sketch, "E2.3.0.33", {"position": v(3723.6, -72.63) * mm});
            skPoint(sketch, "E2.3.0.34", {"position": v(4153.36, 364.25) * mm});
            skLineSegment(sketch, "E2.3.0.35", {"start": v(4111.43, 349.03) * mm, "end": v(4043.13, 406.43) * mm});
            skCircle(sketch, "E2.3.0.36", {"center": v(4127, 218.44) * mm, "radius": 77.26 * mm, "construction": true});
            skCircle(sketch, "E2.3.0.37", {"center": v(4127, 0) * mm, "radius": 77.26 * mm, "construction": true});
            skLineSegment(sketch, "E2.3.0.38", {"start": v(3927.67, 87.85) * mm, "end": v(3995.97, 30.45) * mm});
            skLineSegment(sketch, "E2.3.0.39", {"start": v(4273.58, 494.28) * mm, "end": v(4357.44, 524.73) * mm});
            skLineSegment(sketch, "E2.3.0.40", {"start": v(4273.58, 275.84) * mm, "end": v(4357.44, 306.3) * mm});
            skLineSegment(sketch, "E2.3.0.41", {"start": v(3566.2, 248.89) * mm, "end": v(3550.64, 161.04) * mm});
            skCircle(sketch, "E2.3.0.42", {"center": v(3482.34, 436.88) * mm, "radius": 77.26 * mm, "construction": true});
            skCircle(sketch, "E2.3.0.43", {"center": v(3482.34, 0) * mm, "radius": 77.26 * mm, "construction": true});
            skLineSegment(sketch, "E2.3.0.44", {"start": v(3466.78, -87.85) * mm, "end": v(3398.48, -30.45) * mm});
            skLineSegment(sketch, "E2.3.0.45", {"start": v(3414.04, 57.4) * mm, "end": v(3497.9, 87.85) * mm});
            skCircle(sketch, "E2.3.0.46", {"center": v(3482.34, 218.44) * mm, "radius": 77.26 * mm, "construction": true});
            skLineSegment(sketch, "E2.3.0.47", {"start": v(3466.78, 130.59) * mm, "end": v(3398.48, 188) * mm});
            skLineSegment(sketch, "E2.3.0.48", {"start": v(3398.48, 188) * mm, "end": v(3414.04, 275.84) * mm});
            skLineSegment(sketch, "E2.3.0.49", {"start": v(3414.04, 275.84) * mm, "end": v(3497.9, 306.3) * mm});
            skLineSegment(sketch, "E2.3.0.50", {"start": v(3497.9, 306.3) * mm, "end": v(3566.2, 248.89) * mm});
            skPoint(sketch, "E2.3.0.51", {"position": v(3938.48, 145.81) * mm});
            skLineSegment(sketch, "E2.3.0.52", {"start": v(3995.97, 248.89) * mm, "end": v(3980.4, 161.04) * mm});
            skLineSegment(sketch, "E2.3.0.53", {"start": v(3628.92, 494.28) * mm, "end": v(3712.78, 524.73) * mm});
            skLineSegment(sketch, "E2.3.0.54", {"start": v(4357.44, 524.73) * mm, "end": v(4425.74, 467.33) * mm});
            skLineSegment(sketch, "E2.3.0.55", {"start": v(3466.78, 349.03) * mm, "end": v(3398.48, 406.43) * mm});
            skLineSegment(sketch, "E2.3.0.56", {"start": v(3995.97, 30.45) * mm, "end": v(3980.4, -57.4) * mm});
            skCircle(sketch, "E2.3.0.57", {"center": v(3912.1, 436.88) * mm, "radius": 77.26 * mm, "construction": true});
            skLineSegment(sketch, "E2.3.0.58", {"start": v(4425.74, 467.33) * mm, "end": v(4410.18, 379.48) * mm});
            skLineSegment(sketch, "E2.3.0.59", {"start": v(4111.43, 130.59) * mm, "end": v(4043.13, 188) * mm});
            skPoint(sketch, "E2.3.0.60", {"position": v(3723.6, 145.81) * mm});
            skPoint(sketch, "E2.3.0.61", {"position": v(4368.25, -72.63) * mm});
            skLineSegment(sketch, "E2.3.0.62", {"start": v(4058.7, 494.28) * mm, "end": v(4142.55, 524.73) * mm});
            skCircle(sketch, "E2.3.0.63", {"center": v(3912.1, 218.44) * mm, "radius": 77.26 * mm, "construction": true});
            skLineSegment(sketch, "E2.3.0.64", {"start": v(4425.74, 248.89) * mm, "end": v(4410.18, 161.04) * mm});
            skLineSegment(sketch, "E2.3.0.65", {"start": v(3628.92, 57.4) * mm, "end": v(3712.78, 87.85) * mm});
            skLineSegment(sketch, "E2.3.0.66", {"start": v(3398.48, -30.45) * mm, "end": v(3613.36, -30.45) * mm, "construction": true});
            skLineSegment(sketch, "E2.3.0.67", {"start": v(4357.44, 87.85) * mm, "end": v(4425.74, 30.45) * mm});
            skLineSegment(sketch, "E2.3.0.68", {"start": v(3414.04, 494.28) * mm, "end": v(3497.9, 524.73) * mm});
            skLineSegment(sketch, "E2.3.0.69", {"start": v(4142.55, 524.73) * mm, "end": v(4210.85, 467.33) * mm});
            skCircle(sketch, "E2.3.0.70", {"center": v(4341.88, 436.88) * mm, "radius": 77.26 * mm, "construction": true});
            skPoint(sketch, "E2.3.0.71", {"position": v(3938.48, 364.25) * mm});
            skPoint(sketch, "E2.3.0.72", {"position": v(3508.7, -72.63) * mm});
            skLineSegment(sketch, "E2.3.0.73", {"start": v(4058.7, 275.84) * mm, "end": v(4142.55, 306.3) * mm});
            skLineSegment(sketch, "E2.3.0.74", {"start": v(4210.85, 467.33) * mm, "end": v(4195.3, 379.48) * mm});
            skLineSegment(sketch, "E2.3.0.75", {"start": v(4410.18, 379.48) * mm, "end": v(4326.32, 349.03) * mm});
            skLineSegment(sketch, "E2.3.0.76", {"start": v(3828.25, 406.43) * mm, "end": v(3843.8, 494.28) * mm});
            skLineSegment(sketch, "E2.3.0.77", {"start": v(3980.4, -57.4) * mm, "end": v(3896.55, -87.85) * mm});
            skLineSegment(sketch, "E2.3.0.78", {"start": v(3781.08, 30.45) * mm, "end": v(3765.52, -57.4) * mm});
            skLineSegment(sketch, "E2.3.0.79", {"start": v(4142.55, 306.3) * mm, "end": v(4210.85, 248.89) * mm});
            skLineSegment(sketch, "E2.3.0.80", {"start": v(4142.55, 87.85) * mm, "end": v(4210.85, 30.45) * mm});
            skLineSegment(sketch, "E2.3.0.81", {"start": v(3765.52, 379.48) * mm, "end": v(3681.66, 349.03) * mm});
            skLineSegment(sketch, "E2.3.0.82", {"start": v(3765.52, 161.04) * mm, "end": v(3681.66, 130.59) * mm});
            skLineSegment(sketch, "E2.3.0.83", {"start": v(4326.32, 349.03) * mm, "end": v(4258.02, 406.43) * mm});
            skLineSegment(sketch, "E2.3.0.84", {"start": v(4326.32, 130.59) * mm, "end": v(4258.02, 188) * mm});
            skLineSegment(sketch, "E2.3.0.85", {"start": v(4410.18, 161.04) * mm, "end": v(4326.32, 130.59) * mm});
            skLineSegment(sketch, "E2.3.0.86", {"start": v(4210.85, 248.89) * mm, "end": v(4195.3, 161.04) * mm});
            skLineSegment(sketch, "E2.3.0.87", {"start": v(4195.3, 379.48) * mm, "end": v(4111.43, 349.03) * mm});
            skLineSegment(sketch, "E2.3.0.88", {"start": v(4410.18, -57.4) * mm, "end": v(4326.32, -87.85) * mm});
            skLineSegment(sketch, "E2.3.0.89", {"start": v(4210.85, 30.45) * mm, "end": v(4195.3, -57.4) * mm});
            skLineSegment(sketch, "E2.3.0.90", {"start": v(3681.66, 349.03) * mm, "end": v(3613.36, 406.43) * mm});
            skLineSegment(sketch, "E2.3.0.91", {"start": v(4258.02, 406.43) * mm, "end": v(4273.58, 494.28) * mm});
            skLineSegment(sketch, "E2.3.0.92", {"start": v(3765.52, -57.4) * mm, "end": v(3681.66, -87.85) * mm});
            skLineSegment(sketch, "E2.3.0.93", {"start": v(4326.32, -87.85) * mm, "end": v(4258.02, -30.45) * mm});
            skLineSegment(sketch, "E2.3.0.94", {"start": v(3927.67, 306.3) * mm, "end": v(3995.97, 248.89) * mm});
            skLineSegment(sketch, "E2.3.0.95", {"start": v(3613.36, 406.43) * mm, "end": v(3628.92, 494.28) * mm});
            skLineSegment(sketch, "E2.3.0.96", {"start": v(3613.36, 188) * mm, "end": v(3628.92, 275.84) * mm});
            skLineSegment(sketch, "E2.3.0.97", {"start": v(3550.64, 379.48) * mm, "end": v(3466.78, 349.03) * mm});
            skLineSegment(sketch, "E2.3.0.98", {"start": v(3550.64, -57.4) * mm, "end": v(3466.78, -87.85) * mm});
            skLineSegment(sketch, "E2.3.0.99", {"start": v(3398.48, -30.45) * mm, "end": v(3414.04, 57.4) * mm});
            skLineSegment(sketch, "E2.3.0.100", {"start": v(3497.9, 87.85) * mm, "end": v(3566.2, 30.45) * mm});
            skLineSegment(sketch, "E2.3.0.101", {"start": v(3566.2, 30.45) * mm, "end": v(3550.64, -57.4) * mm});
            skLineSegment(sketch, "E2.3.0.102", {"start": v(3550.64, 161.04) * mm, "end": v(3466.78, 130.59) * mm});
            skLineSegment(sketch, "E2.3.0.103", {"start": v(4357.44, 306.3) * mm, "end": v(4425.74, 248.89) * mm});
            skLineSegment(sketch, "E2.3.0.104", {"start": v(3681.66, -87.85) * mm, "end": v(3613.36, -30.45) * mm});
            skLineSegment(sketch, "E2.3.0.105", {"start": v(4258.02, -30.45) * mm, "end": v(4273.58, 57.4) * mm});
            skLineSegment(sketch, "E2.3.0.106", {"start": v(4195.3, 161.04) * mm, "end": v(4111.43, 130.59) * mm});
            skLineSegment(sketch, "E2.3.0.107", {"start": v(4043.13, 406.43) * mm, "end": v(4058.7, 494.28) * mm});
            skLineSegment(sketch, "E2.3.0.108", {"start": v(4195.3, -57.4) * mm, "end": v(4111.43, -87.85) * mm});
            skLineSegment(sketch, "E2.3.0.109", {"start": v(3628.92, 275.84) * mm, "end": v(3712.78, 306.3) * mm});
            skLineSegment(sketch, "E2.3.0.110", {"start": v(3712.78, 524.73) * mm, "end": v(3781.08, 467.33) * mm});
            skLineSegment(sketch, "E2.3.0.111", {"start": v(3613.36, -30.45) * mm, "end": v(3628.92, 57.4) * mm});
            skLineSegment(sketch, "E2.3.0.112", {"start": v(4273.58, 57.4) * mm, "end": v(4357.44, 87.85) * mm});
            skLineSegment(sketch, "E2.3.0.113", {"start": v(3398.48, 406.43) * mm, "end": v(3414.04, 494.28) * mm});
            skLineSegment(sketch, "E2.3.0.114", {"start": v(4111.43, -87.85) * mm, "end": v(4043.13, -30.45) * mm});
            skLineSegment(sketch, "E2.3.0.115", {"start": v(3712.78, 306.3) * mm, "end": v(3781.08, 248.89) * mm});
            skLineSegment(sketch, "E2.3.0.116", {"start": v(3980.4, 379.48) * mm, "end": v(3896.55, 349.03) * mm});
            skLineSegment(sketch, "E2.3.0.117", {"start": v(3781.08, 467.33) * mm, "end": v(3765.52, 379.48) * mm});
            skLineSegment(sketch, "E2.3.0.118", {"start": v(4043.13, 188) * mm, "end": v(4058.7, 275.84) * mm});
            skLineSegment(sketch, "E2.3.0.119", {"start": v(4043.13, -30.45) * mm, "end": v(4058.7, 57.4) * mm});
            skLineSegment(sketch, "E2.3.0.120", {"start": v(3980.4, 161.04) * mm, "end": v(3896.55, 130.59) * mm});
            skLineSegment(sketch, "E2.3.0.121", {"start": v(3781.08, 248.89) * mm, "end": v(3765.52, 161.04) * mm});
            skLineSegment(sketch, "E2.3.1.0", {"start": v(4425.74, 840.7) * mm, "end": v(4410.18, 752.86) * mm});
            skLineSegment(sketch, "E2.3.1.1", {"start": v(3398.48, 779.81) * mm, "end": v(3398.48, 998.25) * mm, "construction": true});
            skLineSegment(sketch, "E2.3.1.2", {"start": v(3712.78, 898.11) * mm, "end": v(3781.08, 840.7) * mm});
            skCircle(sketch, "E2.3.1.3", {"center": v(3912.1, 810.26) * mm, "radius": 77.26 * mm, "construction": true});
            skLineSegment(sketch, "E2.3.1.4", {"start": v(3896.55, 1159.29) * mm, "end": v(3828.25, 1216.7) * mm});
            skPoint(sketch, "E2.3.1.5", {"position": v(4368.25, 956.07) * mm});
            skPoint(sketch, "E2.3.1.6", {"position": v(3723.6, 1174.51) * mm});
            skLineSegment(sketch, "E2.3.1.7", {"start": v(3497.9, 1335) * mm, "end": v(3566.2, 1277.59) * mm});
            skLineSegment(sketch, "E2.3.1.8", {"start": v(4058.7, 867.66) * mm, "end": v(4142.55, 898.11) * mm});
            skLineSegment(sketch, "E2.3.1.9", {"start": v(3896.55, 940.85) * mm, "end": v(3828.25, 998.25) * mm});
            skCircle(sketch, "E2.3.1.10", {"center": v(3697.22, 1247.14) * mm, "radius": 77.26 * mm, "construction": true});
            skPoint(sketch, "E2.3.1.11", {"position": v(3508.7, 1174.51) * mm});
            skPoint(sketch, "E2.3.1.12", {"position": v(4153.36, 956.07) * mm});
            skCircle(sketch, "E2.3.1.13", {"center": v(4341.88, 1028.7) * mm, "radius": 77.26 * mm, "construction": true});
            skLineSegment(sketch, "E2.3.1.14", {"start": v(3566.2, 1277.59) * mm, "end": v(3550.64, 1189.74) * mm});
            skCircle(sketch, "E2.3.1.15", {"center": v(4127, 1247.14) * mm, "radius": 77.26 * mm, "construction": true});
            skCircle(sketch, "E2.3.1.16", {"center": v(4341.88, 810.26) * mm, "radius": 77.26 * mm, "construction": true});
            skLineSegment(sketch, "E2.3.1.17", {"start": v(3927.67, 1335) * mm, "end": v(3995.97, 1277.59) * mm});
            skLineSegment(sketch, "E2.3.1.18", {"start": v(3828.25, 779.81) * mm, "end": v(3843.8, 867.66) * mm});
            skLineSegment(sketch, "E2.3.1.19", {"start": v(3828.25, 998.25) * mm, "end": v(3843.8, 1086.1) * mm});
            skPoint(sketch, "E2.3.1.20", {"position": v(4153.36, 737.63) * mm});
            skPoint(sketch, "E2.3.1.21", {"position": v(3508.7, 956.07) * mm});
            skPoint(sketch, "E2.3.1.22", {"position": v(3938.48, 737.63) * mm});
            skPoint(sketch, "E2.3.1.23", {"position": v(4368.25, 1174.51) * mm});
            skLineSegment(sketch, "E2.3.1.24", {"start": v(3843.8, 1304.54) * mm, "end": v(3927.67, 1335) * mm});
            skLineSegment(sketch, "E2.3.1.25", {"start": v(3896.55, 722.4) * mm, "end": v(3828.25, 779.81) * mm});
            skCircle(sketch, "E2.3.1.26", {"center": v(3697.22, 1028.7) * mm, "radius": 77.26 * mm, "construction": true});
            skCircle(sketch, "E2.3.1.27", {"center": v(3697.22, 810.26) * mm, "radius": 77.26 * mm, "construction": true});
            skLineSegment(sketch, "E2.3.1.28", {"start": v(3995.97, 1277.59) * mm, "end": v(3980.4, 1189.74) * mm});
            skLineSegment(sketch, "E2.3.1.29", {"start": v(3843.8, 1086.1) * mm, "end": v(3927.67, 1116.55) * mm});
            skLineSegment(sketch, "E2.3.1.30", {"start": v(3843.8, 867.66) * mm, "end": v(3927.67, 898.11) * mm});
            skLineSegment(sketch, "E2.3.1.31", {"start": v(3681.66, 940.85) * mm, "end": v(3613.36, 998.25) * mm});
            skLineSegment(sketch, "E2.3.1.32", {"start": v(4258.02, 998.25) * mm, "end": v(4273.58, 1086.1) * mm});
            skPoint(sketch, "E2.3.1.33", {"position": v(3723.6, 737.63) * mm});
            skPoint(sketch, "E2.3.1.34", {"position": v(4153.36, 1174.51) * mm});
            skLineSegment(sketch, "E2.3.1.35", {"start": v(4111.43, 1159.29) * mm, "end": v(4043.13, 1216.7) * mm});
            skCircle(sketch, "E2.3.1.36", {"center": v(4127, 1028.7) * mm, "radius": 77.26 * mm, "construction": true});
            skCircle(sketch, "E2.3.1.37", {"center": v(4127, 810.26) * mm, "radius": 77.26 * mm, "construction": true});
            skLineSegment(sketch, "E2.3.1.38", {"start": v(3927.67, 898.11) * mm, "end": v(3995.97, 840.7) * mm});
            skLineSegment(sketch, "E2.3.1.39", {"start": v(4273.58, 1304.54) * mm, "end": v(4357.44, 1335) * mm});
            skLineSegment(sketch, "E2.3.1.40", {"start": v(4273.58, 1086.1) * mm, "end": v(4357.44, 1116.55) * mm});
            skLineSegment(sketch, "E2.3.1.41", {"start": v(3566.2, 1059.15) * mm, "end": v(3550.64, 971.3) * mm});
            skCircle(sketch, "E2.3.1.42", {"center": v(3482.34, 1247.14) * mm, "radius": 77.26 * mm, "construction": true});
            skCircle(sketch, "E2.3.1.43", {"center": v(3482.34, 810.26) * mm, "radius": 77.26 * mm, "construction": true});
            skLineSegment(sketch, "E2.3.1.44", {"start": v(3466.78, 722.4) * mm, "end": v(3398.48, 779.81) * mm});
            skLineSegment(sketch, "E2.3.1.45", {"start": v(3414.04, 867.66) * mm, "end": v(3497.9, 898.11) * mm});
            skCircle(sketch, "E2.3.1.46", {"center": v(3482.34, 1028.7) * mm, "radius": 77.26 * mm, "construction": true});
            skLineSegment(sketch, "E2.3.1.47", {"start": v(3466.78, 940.85) * mm, "end": v(3398.48, 998.25) * mm});
            skLineSegment(sketch, "E2.3.1.48", {"start": v(3398.48, 998.25) * mm, "end": v(3414.04, 1086.1) * mm});
            skLineSegment(sketch, "E2.3.1.49", {"start": v(3414.04, 1086.1) * mm, "end": v(3497.9, 1116.55) * mm});
            skLineSegment(sketch, "E2.3.1.50", {"start": v(3497.9, 1116.55) * mm, "end": v(3566.2, 1059.15) * mm});
            skPoint(sketch, "E2.3.1.51", {"position": v(3938.48, 956.07) * mm});
            skLineSegment(sketch, "E2.3.1.52", {"start": v(3995.97, 1059.15) * mm, "end": v(3980.4, 971.3) * mm});
            skLineSegment(sketch, "E2.3.1.53", {"start": v(3628.92, 1304.54) * mm, "end": v(3712.78, 1335) * mm});
            skLineSegment(sketch, "E2.3.1.54", {"start": v(4357.44, 1335) * mm, "end": v(4425.74, 1277.59) * mm});
            skLineSegment(sketch, "E2.3.1.55", {"start": v(3466.78, 1159.29) * mm, "end": v(3398.48, 1216.7) * mm});
            skLineSegment(sketch, "E2.3.1.56", {"start": v(3995.97, 840.7) * mm, "end": v(3980.4, 752.86) * mm});
            skCircle(sketch, "E2.3.1.57", {"center": v(3912.1, 1247.14) * mm, "radius": 77.26 * mm, "construction": true});
            skLineSegment(sketch, "E2.3.1.58", {"start": v(4425.74, 1277.59) * mm, "end": v(4410.18, 1189.74) * mm});
            skLineSegment(sketch, "E2.3.1.59", {"start": v(4111.43, 940.85) * mm, "end": v(4043.13, 998.25) * mm});
            skPoint(sketch, "E2.3.1.60", {"position": v(3723.6, 956.07) * mm});
            skPoint(sketch, "E2.3.1.61", {"position": v(4368.25, 737.63) * mm});
            skLineSegment(sketch, "E2.3.1.62", {"start": v(4058.7, 1304.54) * mm, "end": v(4142.55, 1335) * mm});
            skCircle(sketch, "E2.3.1.63", {"center": v(3912.1, 1028.7) * mm, "radius": 77.26 * mm, "construction": true});
            skLineSegment(sketch, "E2.3.1.64", {"start": v(4425.74, 1059.15) * mm, "end": v(4410.18, 971.3) * mm});
            skLineSegment(sketch, "E2.3.1.65", {"start": v(3628.92, 867.66) * mm, "end": v(3712.78, 898.11) * mm});
            skLineSegment(sketch, "E2.3.1.66", {"start": v(3398.48, 779.81) * mm, "end": v(3613.36, 779.81) * mm, "construction": true});
            skLineSegment(sketch, "E2.3.1.67", {"start": v(4357.44, 898.11) * mm, "end": v(4425.74, 840.7) * mm});
            skLineSegment(sketch, "E2.3.1.68", {"start": v(3414.04, 1304.54) * mm, "end": v(3497.9, 1335) * mm});
            skLineSegment(sketch, "E2.3.1.69", {"start": v(4142.55, 1335) * mm, "end": v(4210.85, 1277.59) * mm});
            skCircle(sketch, "E2.3.1.70", {"center": v(4341.88, 1247.14) * mm, "radius": 77.26 * mm, "construction": true});
            skPoint(sketch, "E2.3.1.71", {"position": v(3938.48, 1174.51) * mm});
            skPoint(sketch, "E2.3.1.72", {"position": v(3508.7, 737.63) * mm});
            skLineSegment(sketch, "E2.3.1.73", {"start": v(4058.7, 1086.1) * mm, "end": v(4142.55, 1116.55) * mm});
            skLineSegment(sketch, "E2.3.1.74", {"start": v(4210.85, 1277.59) * mm, "end": v(4195.3, 1189.74) * mm});
            skLineSegment(sketch, "E2.3.1.75", {"start": v(4410.18, 1189.74) * mm, "end": v(4326.32, 1159.29) * mm});
            skLineSegment(sketch, "E2.3.1.76", {"start": v(3828.25, 1216.7) * mm, "end": v(3843.8, 1304.54) * mm});
            skLineSegment(sketch, "E2.3.1.77", {"start": v(3980.4, 752.86) * mm, "end": v(3896.55, 722.4) * mm});
            skLineSegment(sketch, "E2.3.1.78", {"start": v(3781.08, 840.7) * mm, "end": v(3765.52, 752.86) * mm});
            skLineSegment(sketch, "E2.3.1.79", {"start": v(4142.55, 1116.55) * mm, "end": v(4210.85, 1059.15) * mm});
            skLineSegment(sketch, "E2.3.1.80", {"start": v(4142.55, 898.11) * mm, "end": v(4210.85, 840.7) * mm});
            skLineSegment(sketch, "E2.3.1.81", {"start": v(3765.52, 1189.74) * mm, "end": v(3681.66, 1159.29) * mm});
            skLineSegment(sketch, "E2.3.1.82", {"start": v(3765.52, 971.3) * mm, "end": v(3681.66, 940.85) * mm});
            skLineSegment(sketch, "E2.3.1.83", {"start": v(4326.32, 1159.29) * mm, "end": v(4258.02, 1216.7) * mm});
            skLineSegment(sketch, "E2.3.1.84", {"start": v(4326.32, 940.85) * mm, "end": v(4258.02, 998.25) * mm});
            skLineSegment(sketch, "E2.3.1.85", {"start": v(4410.18, 971.3) * mm, "end": v(4326.32, 940.85) * mm});
            skLineSegment(sketch, "E2.3.1.86", {"start": v(4210.85, 1059.15) * mm, "end": v(4195.3, 971.3) * mm});
            skLineSegment(sketch, "E2.3.1.87", {"start": v(4195.3, 1189.74) * mm, "end": v(4111.43, 1159.29) * mm});
            skLineSegment(sketch, "E2.3.1.88", {"start": v(4410.18, 752.86) * mm, "end": v(4326.32, 722.4) * mm});
            skLineSegment(sketch, "E2.3.1.89", {"start": v(4210.85, 840.7) * mm, "end": v(4195.3, 752.86) * mm});
            skLineSegment(sketch, "E2.3.1.90", {"start": v(3681.66, 1159.29) * mm, "end": v(3613.36, 1216.7) * mm});
            skLineSegment(sketch, "E2.3.1.91", {"start": v(4258.02, 1216.7) * mm, "end": v(4273.58, 1304.54) * mm});
            skLineSegment(sketch, "E2.3.1.92", {"start": v(3765.52, 752.86) * mm, "end": v(3681.66, 722.4) * mm});
            skLineSegment(sketch, "E2.3.1.93", {"start": v(4326.32, 722.4) * mm, "end": v(4258.02, 779.81) * mm});
            skLineSegment(sketch, "E2.3.1.94", {"start": v(3927.67, 1116.55) * mm, "end": v(3995.97, 1059.15) * mm});
            skLineSegment(sketch, "E2.3.1.95", {"start": v(3613.36, 1216.7) * mm, "end": v(3628.92, 1304.54) * mm});
            skLineSegment(sketch, "E2.3.1.96", {"start": v(3613.36, 998.25) * mm, "end": v(3628.92, 1086.1) * mm});
            skLineSegment(sketch, "E2.3.1.97", {"start": v(3550.64, 1189.74) * mm, "end": v(3466.78, 1159.29) * mm});
            skLineSegment(sketch, "E2.3.1.98", {"start": v(3550.64, 752.86) * mm, "end": v(3466.78, 722.4) * mm});
            skLineSegment(sketch, "E2.3.1.99", {"start": v(3398.48, 779.81) * mm, "end": v(3414.04, 867.66) * mm});
            skLineSegment(sketch, "E2.3.1.100", {"start": v(3497.9, 898.11) * mm, "end": v(3566.2, 840.7) * mm});
            skLineSegment(sketch, "E2.3.1.101", {"start": v(3566.2, 840.7) * mm, "end": v(3550.64, 752.86) * mm});
            skLineSegment(sketch, "E2.3.1.102", {"start": v(3550.64, 971.3) * mm, "end": v(3466.78, 940.85) * mm});
            skLineSegment(sketch, "E2.3.1.103", {"start": v(4357.44, 1116.55) * mm, "end": v(4425.74, 1059.15) * mm});
            skLineSegment(sketch, "E2.3.1.104", {"start": v(3681.66, 722.4) * mm, "end": v(3613.36, 779.81) * mm});
            skLineSegment(sketch, "E2.3.1.105", {"start": v(4258.02, 779.81) * mm, "end": v(4273.58, 867.66) * mm});
            skLineSegment(sketch, "E2.3.1.106", {"start": v(4195.3, 971.3) * mm, "end": v(4111.43, 940.85) * mm});
            skLineSegment(sketch, "E2.3.1.107", {"start": v(4043.13, 1216.7) * mm, "end": v(4058.7, 1304.54) * mm});
            skLineSegment(sketch, "E2.3.1.108", {"start": v(4195.3, 752.86) * mm, "end": v(4111.43, 722.4) * mm});
            skLineSegment(sketch, "E2.3.1.109", {"start": v(3628.92, 1086.1) * mm, "end": v(3712.78, 1116.55) * mm});
            skLineSegment(sketch, "E2.3.1.110", {"start": v(3712.78, 1335) * mm, "end": v(3781.08, 1277.59) * mm});
            skLineSegment(sketch, "E2.3.1.111", {"start": v(3613.36, 779.81) * mm, "end": v(3628.92, 867.66) * mm});
            skLineSegment(sketch, "E2.3.1.112", {"start": v(4273.58, 867.66) * mm, "end": v(4357.44, 898.11) * mm});
            skLineSegment(sketch, "E2.3.1.113", {"start": v(3398.48, 1216.7) * mm, "end": v(3414.04, 1304.54) * mm});
            skLineSegment(sketch, "E2.3.1.114", {"start": v(4111.43, 722.4) * mm, "end": v(4043.13, 779.81) * mm});
            skLineSegment(sketch, "E2.3.1.115", {"start": v(3712.78, 1116.55) * mm, "end": v(3781.08, 1059.15) * mm});
            skLineSegment(sketch, "E2.3.1.116", {"start": v(3980.4, 1189.74) * mm, "end": v(3896.55, 1159.29) * mm});
            skLineSegment(sketch, "E2.3.1.117", {"start": v(3781.08, 1277.59) * mm, "end": v(3765.52, 1189.74) * mm});
            skLineSegment(sketch, "E2.3.1.118", {"start": v(4043.13, 998.25) * mm, "end": v(4058.7, 1086.1) * mm});
            skLineSegment(sketch, "E2.3.1.119", {"start": v(4043.13, 779.81) * mm, "end": v(4058.7, 867.66) * mm});
            skLineSegment(sketch, "E2.3.1.120", {"start": v(3980.4, 971.3) * mm, "end": v(3896.55, 940.85) * mm});
            skLineSegment(sketch, "E2.3.1.121", {"start": v(3781.08, 1059.15) * mm, "end": v(3765.52, 971.3) * mm});
            skLineSegment(sketch, "E2.3.2.0", {"start": v(4425.74, 1650.97) * mm, "end": v(4410.18, 1563.12) * mm});
            skLineSegment(sketch, "E2.3.2.1", {"start": v(3398.48, 1590.07) * mm, "end": v(3398.48, 1808.51) * mm, "construction": true});
            skLineSegment(sketch, "E2.3.2.2", {"start": v(3712.78, 1708.37) * mm, "end": v(3781.08, 1650.97) * mm});
            skCircle(sketch, "E2.3.2.3", {"center": v(3912.1, 1620.52) * mm, "radius": 77.26 * mm, "construction": true});
            skLineSegment(sketch, "E2.3.2.4", {"start": v(3896.55, 1969.55) * mm, "end": v(3828.25, 2026.95) * mm});
            skPoint(sketch, "E2.3.2.5", {"position": v(4368.25, 1766.33) * mm});
            skPoint(sketch, "E2.3.2.6", {"position": v(3723.6, 1984.77) * mm});
            skLineSegment(sketch, "E2.3.2.7", {"start": v(3497.9, 2145.25) * mm, "end": v(3566.2, 2087.85) * mm});
            skLineSegment(sketch, "E2.3.2.8", {"start": v(4058.7, 1677.92) * mm, "end": v(4142.55, 1708.37) * mm});
            skLineSegment(sketch, "E2.3.2.9", {"start": v(3896.55, 1751.1) * mm, "end": v(3828.25, 1808.51) * mm});
            skCircle(sketch, "E2.3.2.10", {"center": v(3697.22, 2057.4) * mm, "radius": 77.26 * mm, "construction": true});
            skPoint(sketch, "E2.3.2.11", {"position": v(3508.7, 1984.77) * mm});
            skPoint(sketch, "E2.3.2.12", {"position": v(4153.36, 1766.33) * mm});
            skCircle(sketch, "E2.3.2.13", {"center": v(4341.88, 1838.96) * mm, "radius": 77.26 * mm, "construction": true});
            skLineSegment(sketch, "E2.3.2.14", {"start": v(3566.2, 2087.85) * mm, "end": v(3550.64, 2000) * mm});
            skCircle(sketch, "E2.3.2.15", {"center": v(4127, 2057.4) * mm, "radius": 77.26 * mm, "construction": true});
            skCircle(sketch, "E2.3.2.16", {"center": v(4341.88, 1620.52) * mm, "radius": 77.26 * mm, "construction": true});
            skLineSegment(sketch, "E2.3.2.17", {"start": v(3927.67, 2145.25) * mm, "end": v(3995.97, 2087.85) * mm});
            skLineSegment(sketch, "E2.3.2.18", {"start": v(3828.25, 1590.07) * mm, "end": v(3843.8, 1677.92) * mm});
            skLineSegment(sketch, "E2.3.2.19", {"start": v(3828.25, 1808.51) * mm, "end": v(3843.8, 1896.36) * mm});
            skPoint(sketch, "E2.3.2.20", {"position": v(4153.36, 1547.9) * mm});
            skPoint(sketch, "E2.3.2.21", {"position": v(3508.7, 1766.33) * mm});
            skPoint(sketch, "E2.3.2.22", {"position": v(3938.48, 1547.9) * mm});
            skPoint(sketch, "E2.3.2.23", {"position": v(4368.25, 1984.77) * mm});
            skLineSegment(sketch, "E2.3.2.24", {"start": v(3843.8, 2114.8) * mm, "end": v(3927.67, 2145.25) * mm});
            skLineSegment(sketch, "E2.3.2.25", {"start": v(3896.55, 1532.67) * mm, "end": v(3828.25, 1590.07) * mm});
            skCircle(sketch, "E2.3.2.26", {"center": v(3697.22, 1838.96) * mm, "radius": 77.26 * mm, "construction": true});
            skCircle(sketch, "E2.3.2.27", {"center": v(3697.22, 1620.52) * mm, "radius": 77.26 * mm, "construction": true});
            skLineSegment(sketch, "E2.3.2.28", {"start": v(3995.97, 2087.85) * mm, "end": v(3980.4, 2000) * mm});
            skLineSegment(sketch, "E2.3.2.29", {"start": v(3843.8, 1896.36) * mm, "end": v(3927.67, 1926.81) * mm});
            skLineSegment(sketch, "E2.3.2.30", {"start": v(3843.8, 1677.92) * mm, "end": v(3927.67, 1708.37) * mm});
            skLineSegment(sketch, "E2.3.2.31", {"start": v(3681.66, 1751.1) * mm, "end": v(3613.36, 1808.51) * mm});
            skLineSegment(sketch, "E2.3.2.32", {"start": v(4258.02, 1808.51) * mm, "end": v(4273.58, 1896.36) * mm});
            skPoint(sketch, "E2.3.2.33", {"position": v(3723.6, 1547.9) * mm});
            skPoint(sketch, "E2.3.2.34", {"position": v(4153.36, 1984.77) * mm});
            skLineSegment(sketch, "E2.3.2.35", {"start": v(4111.43, 1969.55) * mm, "end": v(4043.13, 2026.95) * mm});
            skCircle(sketch, "E2.3.2.36", {"center": v(4127, 1838.96) * mm, "radius": 77.26 * mm, "construction": true});
            skCircle(sketch, "E2.3.2.37", {"center": v(4127, 1620.52) * mm, "radius": 77.26 * mm, "construction": true});
            skLineSegment(sketch, "E2.3.2.38", {"start": v(3927.67, 1708.37) * mm, "end": v(3995.97, 1650.97) * mm});
            skLineSegment(sketch, "E2.3.2.39", {"start": v(4273.58, 2114.8) * mm, "end": v(4357.44, 2145.25) * mm});
            skLineSegment(sketch, "E2.3.2.40", {"start": v(4273.58, 1896.36) * mm, "end": v(4357.44, 1926.81) * mm});
            skLineSegment(sketch, "E2.3.2.41", {"start": v(3566.2, 1869.4) * mm, "end": v(3550.64, 1781.56) * mm});
            skCircle(sketch, "E2.3.2.42", {"center": v(3482.34, 2057.4) * mm, "radius": 77.26 * mm, "construction": true});
            skCircle(sketch, "E2.3.2.43", {"center": v(3482.34, 1620.52) * mm, "radius": 77.26 * mm, "construction": true});
            skLineSegment(sketch, "E2.3.2.44", {"start": v(3466.78, 1532.67) * mm, "end": v(3398.48, 1590.07) * mm});
            skLineSegment(sketch, "E2.3.2.45", {"start": v(3414.04, 1677.92) * mm, "end": v(3497.9, 1708.37) * mm});
            skCircle(sketch, "E2.3.2.46", {"center": v(3482.34, 1838.96) * mm, "radius": 77.26 * mm, "construction": true});
            skLineSegment(sketch, "E2.3.2.47", {"start": v(3466.78, 1751.1) * mm, "end": v(3398.48, 1808.51) * mm});
            skLineSegment(sketch, "E2.3.2.48", {"start": v(3398.48, 1808.51) * mm, "end": v(3414.04, 1896.36) * mm});
            skLineSegment(sketch, "E2.3.2.49", {"start": v(3414.04, 1896.36) * mm, "end": v(3497.9, 1926.81) * mm});
            skLineSegment(sketch, "E2.3.2.50", {"start": v(3497.9, 1926.81) * mm, "end": v(3566.2, 1869.4) * mm});
            skPoint(sketch, "E2.3.2.51", {"position": v(3938.48, 1766.33) * mm});
            skLineSegment(sketch, "E2.3.2.52", {"start": v(3995.97, 1869.4) * mm, "end": v(3980.4, 1781.56) * mm});
            skLineSegment(sketch, "E2.3.2.53", {"start": v(3628.92, 2114.8) * mm, "end": v(3712.78, 2145.25) * mm});
            skLineSegment(sketch, "E2.3.2.54", {"start": v(4357.44, 2145.25) * mm, "end": v(4425.74, 2087.85) * mm});
            skLineSegment(sketch, "E2.3.2.55", {"start": v(3466.78, 1969.55) * mm, "end": v(3398.48, 2026.95) * mm});
            skLineSegment(sketch, "E2.3.2.56", {"start": v(3995.97, 1650.97) * mm, "end": v(3980.4, 1563.12) * mm});
            skCircle(sketch, "E2.3.2.57", {"center": v(3912.1, 2057.4) * mm, "radius": 77.26 * mm, "construction": true});
            skLineSegment(sketch, "E2.3.2.58", {"start": v(4425.74, 2087.85) * mm, "end": v(4410.18, 2000) * mm});
            skLineSegment(sketch, "E2.3.2.59", {"start": v(4111.43, 1751.1) * mm, "end": v(4043.13, 1808.51) * mm});
            skPoint(sketch, "E2.3.2.60", {"position": v(3723.6, 1766.33) * mm});
            skPoint(sketch, "E2.3.2.61", {"position": v(4368.25, 1547.9) * mm});
            skLineSegment(sketch, "E2.3.2.62", {"start": v(4058.7, 2114.8) * mm, "end": v(4142.55, 2145.25) * mm});
            skCircle(sketch, "E2.3.2.63", {"center": v(3912.1, 1838.96) * mm, "radius": 77.26 * mm, "construction": true});
            skLineSegment(sketch, "E2.3.2.64", {"start": v(4425.74, 1869.4) * mm, "end": v(4410.18, 1781.56) * mm});
            skLineSegment(sketch, "E2.3.2.65", {"start": v(3628.92, 1677.92) * mm, "end": v(3712.78, 1708.37) * mm});
            skLineSegment(sketch, "E2.3.2.66", {"start": v(3398.48, 1590.07) * mm, "end": v(3613.36, 1590.07) * mm, "construction": true});
            skLineSegment(sketch, "E2.3.2.67", {"start": v(4357.44, 1708.37) * mm, "end": v(4425.74, 1650.97) * mm});
            skLineSegment(sketch, "E2.3.2.68", {"start": v(3414.04, 2114.8) * mm, "end": v(3497.9, 2145.25) * mm});
            skLineSegment(sketch, "E2.3.2.69", {"start": v(4142.55, 2145.25) * mm, "end": v(4210.85, 2087.85) * mm});
            skCircle(sketch, "E2.3.2.70", {"center": v(4341.88, 2057.4) * mm, "radius": 77.26 * mm, "construction": true});
            skPoint(sketch, "E2.3.2.71", {"position": v(3938.48, 1984.77) * mm});
            skPoint(sketch, "E2.3.2.72", {"position": v(3508.7, 1547.9) * mm});
            skLineSegment(sketch, "E2.3.2.73", {"start": v(4058.7, 1896.36) * mm, "end": v(4142.55, 1926.81) * mm});
            skLineSegment(sketch, "E2.3.2.74", {"start": v(4210.85, 2087.85) * mm, "end": v(4195.3, 2000) * mm});
            skLineSegment(sketch, "E2.3.2.75", {"start": v(4410.18, 2000) * mm, "end": v(4326.32, 1969.55) * mm});
            skLineSegment(sketch, "E2.3.2.76", {"start": v(3828.25, 2026.95) * mm, "end": v(3843.8, 2114.8) * mm});
            skLineSegment(sketch, "E2.3.2.77", {"start": v(3980.4, 1563.12) * mm, "end": v(3896.55, 1532.67) * mm});
            skLineSegment(sketch, "E2.3.2.78", {"start": v(3781.08, 1650.97) * mm, "end": v(3765.52, 1563.12) * mm});
            skLineSegment(sketch, "E2.3.2.79", {"start": v(4142.55, 1926.81) * mm, "end": v(4210.85, 1869.4) * mm});
            skLineSegment(sketch, "E2.3.2.80", {"start": v(4142.55, 1708.37) * mm, "end": v(4210.85, 1650.97) * mm});
            skLineSegment(sketch, "E2.3.2.81", {"start": v(3765.52, 2000) * mm, "end": v(3681.66, 1969.55) * mm});
            skLineSegment(sketch, "E2.3.2.82", {"start": v(3765.52, 1781.56) * mm, "end": v(3681.66, 1751.1) * mm});
            skLineSegment(sketch, "E2.3.2.83", {"start": v(4326.32, 1969.55) * mm, "end": v(4258.02, 2026.95) * mm});
            skLineSegment(sketch, "E2.3.2.84", {"start": v(4326.32, 1751.1) * mm, "end": v(4258.02, 1808.51) * mm});
            skLineSegment(sketch, "E2.3.2.85", {"start": v(4410.18, 1781.56) * mm, "end": v(4326.32, 1751.1) * mm});
            skLineSegment(sketch, "E2.3.2.86", {"start": v(4210.85, 1869.4) * mm, "end": v(4195.3, 1781.56) * mm});
            skLineSegment(sketch, "E2.3.2.87", {"start": v(4195.3, 2000) * mm, "end": v(4111.43, 1969.55) * mm});
            skLineSegment(sketch, "E2.3.2.88", {"start": v(4410.18, 1563.12) * mm, "end": v(4326.32, 1532.67) * mm});
            skLineSegment(sketch, "E2.3.2.89", {"start": v(4210.85, 1650.97) * mm, "end": v(4195.3, 1563.12) * mm});
            skLineSegment(sketch, "E2.3.2.90", {"start": v(3681.66, 1969.55) * mm, "end": v(3613.36, 2026.95) * mm});
            skLineSegment(sketch, "E2.3.2.91", {"start": v(4258.02, 2026.95) * mm, "end": v(4273.58, 2114.8) * mm});
            skLineSegment(sketch, "E2.3.2.92", {"start": v(3765.52, 1563.12) * mm, "end": v(3681.66, 1532.67) * mm});
            skLineSegment(sketch, "E2.3.2.93", {"start": v(4326.32, 1532.67) * mm, "end": v(4258.02, 1590.07) * mm});
            skLineSegment(sketch, "E2.3.2.94", {"start": v(3927.67, 1926.81) * mm, "end": v(3995.97, 1869.4) * mm});
            skLineSegment(sketch, "E2.3.2.95", {"start": v(3613.36, 2026.95) * mm, "end": v(3628.92, 2114.8) * mm});
            skLineSegment(sketch, "E2.3.2.96", {"start": v(3613.36, 1808.51) * mm, "end": v(3628.92, 1896.36) * mm});
            skLineSegment(sketch, "E2.3.2.97", {"start": v(3550.64, 2000) * mm, "end": v(3466.78, 1969.55) * mm});
            skLineSegment(sketch, "E2.3.2.98", {"start": v(3550.64, 1563.12) * mm, "end": v(3466.78, 1532.67) * mm});
            skLineSegment(sketch, "E2.3.2.99", {"start": v(3398.48, 1590.07) * mm, "end": v(3414.04, 1677.92) * mm});
            skLineSegment(sketch, "E2.3.2.100", {"start": v(3497.9, 1708.37) * mm, "end": v(3566.2, 1650.97) * mm});
            skLineSegment(sketch, "E2.3.2.101", {"start": v(3566.2, 1650.97) * mm, "end": v(3550.64, 1563.12) * mm});
            skLineSegment(sketch, "E2.3.2.102", {"start": v(3550.64, 1781.56) * mm, "end": v(3466.78, 1751.1) * mm});
            skLineSegment(sketch, "E2.3.2.103", {"start": v(4357.44, 1926.81) * mm, "end": v(4425.74, 1869.4) * mm});
            skLineSegment(sketch, "E2.3.2.104", {"start": v(3681.66, 1532.67) * mm, "end": v(3613.36, 1590.07) * mm});
            skLineSegment(sketch, "E2.3.2.105", {"start": v(4258.02, 1590.07) * mm, "end": v(4273.58, 1677.92) * mm});
            skLineSegment(sketch, "E2.3.2.106", {"start": v(4195.3, 1781.56) * mm, "end": v(4111.43, 1751.1) * mm});
            skLineSegment(sketch, "E2.3.2.107", {"start": v(4043.13, 2026.95) * mm, "end": v(4058.7, 2114.8) * mm});
            skLineSegment(sketch, "E2.3.2.108", {"start": v(4195.3, 1563.12) * mm, "end": v(4111.43, 1532.67) * mm});
            skLineSegment(sketch, "E2.3.2.109", {"start": v(3628.92, 1896.36) * mm, "end": v(3712.78, 1926.81) * mm});
            skLineSegment(sketch, "E2.3.2.110", {"start": v(3712.78, 2145.25) * mm, "end": v(3781.08, 2087.85) * mm});
            skLineSegment(sketch, "E2.3.2.111", {"start": v(3613.36, 1590.07) * mm, "end": v(3628.92, 1677.92) * mm});
            skLineSegment(sketch, "E2.3.2.112", {"start": v(4273.58, 1677.92) * mm, "end": v(4357.44, 1708.37) * mm});
            skLineSegment(sketch, "E2.3.2.113", {"start": v(3398.48, 2026.95) * mm, "end": v(3414.04, 2114.8) * mm});
            skLineSegment(sketch, "E2.3.2.114", {"start": v(4111.43, 1532.67) * mm, "end": v(4043.13, 1590.07) * mm});
            skLineSegment(sketch, "E2.3.2.115", {"start": v(3712.78, 1926.81) * mm, "end": v(3781.08, 1869.4) * mm});
            skLineSegment(sketch, "E2.3.2.116", {"start": v(3980.4, 2000) * mm, "end": v(3896.55, 1969.55) * mm});
            skLineSegment(sketch, "E2.3.2.117", {"start": v(3781.08, 2087.85) * mm, "end": v(3765.52, 2000) * mm});
            skLineSegment(sketch, "E2.3.2.118", {"start": v(4043.13, 1808.51) * mm, "end": v(4058.7, 1896.36) * mm});
            skLineSegment(sketch, "E2.3.2.119", {"start": v(4043.13, 1590.07) * mm, "end": v(4058.7, 1677.92) * mm});
            skLineSegment(sketch, "E2.3.2.120", {"start": v(3980.4, 1781.56) * mm, "end": v(3896.55, 1751.1) * mm});
            skLineSegment(sketch, "E2.3.2.121", {"start": v(3781.08, 1869.4) * mm, "end": v(3765.52, 1781.56) * mm});
            skLineSegment(sketch, "E2.4.0.0", {"start": v(5586.52, 30.45) * mm, "end": v(5570.96, -57.4) * mm});
            skLineSegment(sketch, "E2.4.0.1", {"start": v(4559.26, -30.45) * mm, "end": v(4559.26, 188) * mm, "construction": true});
            skLineSegment(sketch, "E2.4.0.2", {"start": v(4873.56, 87.85) * mm, "end": v(4941.86, 30.45) * mm});
            skCircle(sketch, "E2.4.0.3", {"center": v(5072.89, 0) * mm, "radius": 77.26 * mm, "construction": true});
            skLineSegment(sketch, "E2.4.0.4", {"start": v(5057.33, 349.03) * mm, "end": v(4989.03, 406.43) * mm});
            skPoint(sketch, "E2.4.0.5", {"position": v(5529.03, 145.81) * mm});
            skPoint(sketch, "E2.4.0.6", {"position": v(4884.37, 364.25) * mm});
            skLineSegment(sketch, "E2.4.0.7", {"start": v(4658.68, 524.73) * mm, "end": v(4726.98, 467.33) * mm});
            skLineSegment(sketch, "E2.4.0.8", {"start": v(5219.47, 57.4) * mm, "end": v(5303.33, 87.85) * mm});
            skLineSegment(sketch, "E2.4.0.9", {"start": v(5057.33, 130.59) * mm, "end": v(4989.03, 188) * mm});
            skCircle(sketch, "E2.4.0.10", {"center": v(4858, 436.88) * mm, "radius": 77.26 * mm, "construction": true});
            skPoint(sketch, "E2.4.0.11", {"position": v(4669.49, 364.25) * mm});
            skPoint(sketch, "E2.4.0.12", {"position": v(5314.14, 145.81) * mm});
            skCircle(sketch, "E2.4.0.13", {"center": v(5502.66, 218.44) * mm, "radius": 77.26 * mm, "construction": true});
            skLineSegment(sketch, "E2.4.0.14", {"start": v(4726.98, 467.33) * mm, "end": v(4711.42, 379.48) * mm});
            skCircle(sketch, "E2.4.0.15", {"center": v(5287.77, 436.88) * mm, "radius": 77.26 * mm, "construction": true});
            skCircle(sketch, "E2.4.0.16", {"center": v(5502.66, 0) * mm, "radius": 77.26 * mm, "construction": true});
            skLineSegment(sketch, "E2.4.0.17", {"start": v(5088.45, 524.73) * mm, "end": v(5156.75, 467.33) * mm});
            skLineSegment(sketch, "E2.4.0.18", {"start": v(4989.03, -30.45) * mm, "end": v(5004.59, 57.4) * mm});
            skLineSegment(sketch, "E2.4.0.19", {"start": v(4989.03, 188) * mm, "end": v(5004.59, 275.84) * mm});
            skPoint(sketch, "E2.4.0.20", {"position": v(5314.14, -72.63) * mm});
            skPoint(sketch, "E2.4.0.21", {"position": v(4669.49, 145.81) * mm});
            skPoint(sketch, "E2.4.0.22", {"position": v(5099.26, -72.63) * mm});
            skPoint(sketch, "E2.4.0.23", {"position": v(5529.03, 364.25) * mm});
            skLineSegment(sketch, "E2.4.0.24", {"start": v(5004.59, 494.28) * mm, "end": v(5088.45, 524.73) * mm});
            skLineSegment(sketch, "E2.4.0.25", {"start": v(5057.33, -87.85) * mm, "end": v(4989.03, -30.45) * mm});
            skCircle(sketch, "E2.4.0.26", {"center": v(4858, 218.44) * mm, "radius": 77.26 * mm, "construction": true});
            skCircle(sketch, "E2.4.0.27", {"center": v(4858, 0) * mm, "radius": 77.26 * mm, "construction": true});
            skLineSegment(sketch, "E2.4.0.28", {"start": v(5156.75, 467.33) * mm, "end": v(5141.19, 379.48) * mm});
            skLineSegment(sketch, "E2.4.0.29", {"start": v(5004.59, 275.84) * mm, "end": v(5088.45, 306.3) * mm});
            skLineSegment(sketch, "E2.4.0.30", {"start": v(5004.59, 57.4) * mm, "end": v(5088.45, 87.85) * mm});
            skLineSegment(sketch, "E2.4.0.31", {"start": v(4842.44, 130.59) * mm, "end": v(4774.14, 188) * mm});
            skLineSegment(sketch, "E2.4.0.32", {"start": v(5418.8, 188) * mm, "end": v(5434.36, 275.84) * mm});
            skPoint(sketch, "E2.4.0.33", {"position": v(4884.37, -72.63) * mm});
            skPoint(sketch, "E2.4.0.34", {"position": v(5314.14, 364.25) * mm});
            skLineSegment(sketch, "E2.4.0.35", {"start": v(5272.21, 349.03) * mm, "end": v(5203.91, 406.43) * mm});
            skCircle(sketch, "E2.4.0.36", {"center": v(5287.77, 218.44) * mm, "radius": 77.26 * mm, "construction": true});
            skCircle(sketch, "E2.4.0.37", {"center": v(5287.77, 0) * mm, "radius": 77.26 * mm, "construction": true});
            skLineSegment(sketch, "E2.4.0.38", {"start": v(5088.45, 87.85) * mm, "end": v(5156.75, 30.45) * mm});
            skLineSegment(sketch, "E2.4.0.39", {"start": v(5434.36, 494.28) * mm, "end": v(5518.22, 524.73) * mm});
            skLineSegment(sketch, "E2.4.0.40", {"start": v(5434.36, 275.84) * mm, "end": v(5518.22, 306.3) * mm});
            skLineSegment(sketch, "E2.4.0.41", {"start": v(4726.98, 248.89) * mm, "end": v(4711.42, 161.04) * mm});
            skCircle(sketch, "E2.4.0.42", {"center": v(4643.12, 436.88) * mm, "radius": 77.26 * mm, "construction": true});
            skCircle(sketch, "E2.4.0.43", {"center": v(4643.12, 0) * mm, "radius": 77.26 * mm, "construction": true});
            skLineSegment(sketch, "E2.4.0.44", {"start": v(4627.56, -87.85) * mm, "end": v(4559.26, -30.45) * mm});
            skLineSegment(sketch, "E2.4.0.45", {"start": v(4574.82, 57.4) * mm, "end": v(4658.68, 87.85) * mm});
            skCircle(sketch, "E2.4.0.46", {"center": v(4643.12, 218.44) * mm, "radius": 77.26 * mm, "construction": true});
            skLineSegment(sketch, "E2.4.0.47", {"start": v(4627.56, 130.59) * mm, "end": v(4559.26, 188) * mm});
            skLineSegment(sketch, "E2.4.0.48", {"start": v(4559.26, 188) * mm, "end": v(4574.82, 275.84) * mm});
            skLineSegment(sketch, "E2.4.0.49", {"start": v(4574.82, 275.84) * mm, "end": v(4658.68, 306.3) * mm});
            skLineSegment(sketch, "E2.4.0.50", {"start": v(4658.68, 306.3) * mm, "end": v(4726.98, 248.89) * mm});
            skPoint(sketch, "E2.4.0.51", {"position": v(5099.26, 145.81) * mm});
            skLineSegment(sketch, "E2.4.0.52", {"start": v(5156.75, 248.89) * mm, "end": v(5141.19, 161.04) * mm});
            skLineSegment(sketch, "E2.4.0.53", {"start": v(4789.7, 494.28) * mm, "end": v(4873.56, 524.73) * mm});
            skLineSegment(sketch, "E2.4.0.54", {"start": v(5518.22, 524.73) * mm, "end": v(5586.52, 467.33) * mm});
            skLineSegment(sketch, "E2.4.0.55", {"start": v(4627.56, 349.03) * mm, "end": v(4559.26, 406.43) * mm});
            skLineSegment(sketch, "E2.4.0.56", {"start": v(5156.75, 30.45) * mm, "end": v(5141.19, -57.4) * mm});
            skCircle(sketch, "E2.4.0.57", {"center": v(5072.89, 436.88) * mm, "radius": 77.26 * mm, "construction": true});
            skLineSegment(sketch, "E2.4.0.58", {"start": v(5586.52, 467.33) * mm, "end": v(5570.96, 379.48) * mm});
            skLineSegment(sketch, "E2.4.0.59", {"start": v(5272.21, 130.59) * mm, "end": v(5203.91, 188) * mm});
            skPoint(sketch, "E2.4.0.60", {"position": v(4884.37, 145.81) * mm});
            skPoint(sketch, "E2.4.0.61", {"position": v(5529.03, -72.63) * mm});
            skLineSegment(sketch, "E2.4.0.62", {"start": v(5219.47, 494.28) * mm, "end": v(5303.33, 524.73) * mm});
            skCircle(sketch, "E2.4.0.63", {"center": v(5072.89, 218.44) * mm, "radius": 77.26 * mm, "construction": true});
            skLineSegment(sketch, "E2.4.0.64", {"start": v(5586.52, 248.89) * mm, "end": v(5570.96, 161.04) * mm});
            skLineSegment(sketch, "E2.4.0.65", {"start": v(4789.7, 57.4) * mm, "end": v(4873.56, 87.85) * mm});
            skLineSegment(sketch, "E2.4.0.66", {"start": v(4559.26, -30.45) * mm, "end": v(4774.14, -30.45) * mm, "construction": true});
            skLineSegment(sketch, "E2.4.0.67", {"start": v(5518.22, 87.85) * mm, "end": v(5586.52, 30.45) * mm});
            skLineSegment(sketch, "E2.4.0.68", {"start": v(4574.82, 494.28) * mm, "end": v(4658.68, 524.73) * mm});
            skLineSegment(sketch, "E2.4.0.69", {"start": v(5303.33, 524.73) * mm, "end": v(5371.63, 467.33) * mm});
            skCircle(sketch, "E2.4.0.70", {"center": v(5502.66, 436.88) * mm, "radius": 77.26 * mm, "construction": true});
            skPoint(sketch, "E2.4.0.71", {"position": v(5099.26, 364.25) * mm});
            skPoint(sketch, "E2.4.0.72", {"position": v(4669.49, -72.63) * mm});
            skLineSegment(sketch, "E2.4.0.73", {"start": v(5219.47, 275.84) * mm, "end": v(5303.33, 306.3) * mm});
            skLineSegment(sketch, "E2.4.0.74", {"start": v(5371.63, 467.33) * mm, "end": v(5356.07, 379.48) * mm});
            skLineSegment(sketch, "E2.4.0.75", {"start": v(5570.96, 379.48) * mm, "end": v(5487.1, 349.03) * mm});
            skLineSegment(sketch, "E2.4.0.76", {"start": v(4989.03, 406.43) * mm, "end": v(5004.59, 494.28) * mm});
            skLineSegment(sketch, "E2.4.0.77", {"start": v(5141.19, -57.4) * mm, "end": v(5057.33, -87.85) * mm});
            skLineSegment(sketch, "E2.4.0.78", {"start": v(4941.86, 30.45) * mm, "end": v(4926.3, -57.4) * mm});
            skLineSegment(sketch, "E2.4.0.79", {"start": v(5303.33, 306.3) * mm, "end": v(5371.63, 248.89) * mm});
            skLineSegment(sketch, "E2.4.0.80", {"start": v(5303.33, 87.85) * mm, "end": v(5371.63, 30.45) * mm});
            skLineSegment(sketch, "E2.4.0.81", {"start": v(4926.3, 379.48) * mm, "end": v(4842.44, 349.03) * mm});
            skLineSegment(sketch, "E2.4.0.82", {"start": v(4926.3, 161.04) * mm, "end": v(4842.44, 130.59) * mm});
            skLineSegment(sketch, "E2.4.0.83", {"start": v(5487.1, 349.03) * mm, "end": v(5418.8, 406.43) * mm});
            skLineSegment(sketch, "E2.4.0.84", {"start": v(5487.1, 130.59) * mm, "end": v(5418.8, 188) * mm});
            skLineSegment(sketch, "E2.4.0.85", {"start": v(5570.96, 161.04) * mm, "end": v(5487.1, 130.59) * mm});
            skLineSegment(sketch, "E2.4.0.86", {"start": v(5371.63, 248.89) * mm, "end": v(5356.07, 161.04) * mm});
            skLineSegment(sketch, "E2.4.0.87", {"start": v(5356.07, 379.48) * mm, "end": v(5272.21, 349.03) * mm});
            skLineSegment(sketch, "E2.4.0.88", {"start": v(5570.96, -57.4) * mm, "end": v(5487.1, -87.85) * mm});
            skLineSegment(sketch, "E2.4.0.89", {"start": v(5371.63, 30.45) * mm, "end": v(5356.07, -57.4) * mm});
            skLineSegment(sketch, "E2.4.0.90", {"start": v(4842.44, 349.03) * mm, "end": v(4774.14, 406.43) * mm});
            skLineSegment(sketch, "E2.4.0.91", {"start": v(5418.8, 406.43) * mm, "end": v(5434.36, 494.28) * mm});
            skLineSegment(sketch, "E2.4.0.92", {"start": v(4926.3, -57.4) * mm, "end": v(4842.44, -87.85) * mm});
            skLineSegment(sketch, "E2.4.0.93", {"start": v(5487.1, -87.85) * mm, "end": v(5418.8, -30.45) * mm});
            skLineSegment(sketch, "E2.4.0.94", {"start": v(5088.45, 306.3) * mm, "end": v(5156.75, 248.89) * mm});
            skLineSegment(sketch, "E2.4.0.95", {"start": v(4774.14, 406.43) * mm, "end": v(4789.7, 494.28) * mm});
            skLineSegment(sketch, "E2.4.0.96", {"start": v(4774.14, 188) * mm, "end": v(4789.7, 275.84) * mm});
            skLineSegment(sketch, "E2.4.0.97", {"start": v(4711.42, 379.48) * mm, "end": v(4627.56, 349.03) * mm});
            skLineSegment(sketch, "E2.4.0.98", {"start": v(4711.42, -57.4) * mm, "end": v(4627.56, -87.85) * mm});
            skLineSegment(sketch, "E2.4.0.99", {"start": v(4559.26, -30.45) * mm, "end": v(4574.82, 57.4) * mm});
            skLineSegment(sketch, "E2.4.0.100", {"start": v(4658.68, 87.85) * mm, "end": v(4726.98, 30.45) * mm});
            skLineSegment(sketch, "E2.4.0.101", {"start": v(4726.98, 30.45) * mm, "end": v(4711.42, -57.4) * mm});
            skLineSegment(sketch, "E2.4.0.102", {"start": v(4711.42, 161.04) * mm, "end": v(4627.56, 130.59) * mm});
            skLineSegment(sketch, "E2.4.0.103", {"start": v(5518.22, 306.3) * mm, "end": v(5586.52, 248.89) * mm});
            skLineSegment(sketch, "E2.4.0.104", {"start": v(4842.44, -87.85) * mm, "end": v(4774.14, -30.45) * mm});
            skLineSegment(sketch, "E2.4.0.105", {"start": v(5418.8, -30.45) * mm, "end": v(5434.36, 57.4) * mm});
            skLineSegment(sketch, "E2.4.0.106", {"start": v(5356.07, 161.04) * mm, "end": v(5272.21, 130.59) * mm});
            skLineSegment(sketch, "E2.4.0.107", {"start": v(5203.91, 406.43) * mm, "end": v(5219.47, 494.28) * mm});
            skLineSegment(sketch, "E2.4.0.108", {"start": v(5356.07, -57.4) * mm, "end": v(5272.21, -87.85) * mm});
            skLineSegment(sketch, "E2.4.0.109", {"start": v(4789.7, 275.84) * mm, "end": v(4873.56, 306.3) * mm});
            skLineSegment(sketch, "E2.4.0.110", {"start": v(4873.56, 524.73) * mm, "end": v(4941.86, 467.33) * mm});
            skLineSegment(sketch, "E2.4.0.111", {"start": v(4774.14, -30.45) * mm, "end": v(4789.7, 57.4) * mm});
            skLineSegment(sketch, "E2.4.0.112", {"start": v(5434.36, 57.4) * mm, "end": v(5518.22, 87.85) * mm});
            skLineSegment(sketch, "E2.4.0.113", {"start": v(4559.26, 406.43) * mm, "end": v(4574.82, 494.28) * mm});
            skLineSegment(sketch, "E2.4.0.114", {"start": v(5272.21, -87.85) * mm, "end": v(5203.91, -30.45) * mm});
            skLineSegment(sketch, "E2.4.0.115", {"start": v(4873.56, 306.3) * mm, "end": v(4941.86, 248.89) * mm});
            skLineSegment(sketch, "E2.4.0.116", {"start": v(5141.19, 379.48) * mm, "end": v(5057.33, 349.03) * mm});
            skLineSegment(sketch, "E2.4.0.117", {"start": v(4941.86, 467.33) * mm, "end": v(4926.3, 379.48) * mm});
            skLineSegment(sketch, "E2.4.0.118", {"start": v(5203.91, 188) * mm, "end": v(5219.47, 275.84) * mm});
            skLineSegment(sketch, "E2.4.0.119", {"start": v(5203.91, -30.45) * mm, "end": v(5219.47, 57.4) * mm});
            skLineSegment(sketch, "E2.4.0.120", {"start": v(5141.19, 161.04) * mm, "end": v(5057.33, 130.59) * mm});
            skLineSegment(sketch, "E2.4.0.121", {"start": v(4941.86, 248.89) * mm, "end": v(4926.3, 161.04) * mm});
            skLineSegment(sketch, "E2.4.1.0", {"start": v(5586.52, 840.7) * mm, "end": v(5570.96, 752.86) * mm});
            skLineSegment(sketch, "E2.4.1.1", {"start": v(4559.26, 779.81) * mm, "end": v(4559.26, 998.25) * mm, "construction": true});
            skLineSegment(sketch, "E2.4.1.2", {"start": v(4873.56, 898.11) * mm, "end": v(4941.86, 840.7) * mm});
            skCircle(sketch, "E2.4.1.3", {"center": v(5072.89, 810.26) * mm, "radius": 77.26 * mm, "construction": true});
            skLineSegment(sketch, "E2.4.1.4", {"start": v(5057.33, 1159.29) * mm, "end": v(4989.03, 1216.7) * mm});
            skPoint(sketch, "E2.4.1.5", {"position": v(5529.03, 956.07) * mm});
            skPoint(sketch, "E2.4.1.6", {"position": v(4884.37, 1174.51) * mm});
            skLineSegment(sketch, "E2.4.1.7", {"start": v(4658.68, 1335) * mm, "end": v(4726.98, 1277.59) * mm});
            skLineSegment(sketch, "E2.4.1.8", {"start": v(5219.47, 867.66) * mm, "end": v(5303.33, 898.11) * mm});
            skLineSegment(sketch, "E2.4.1.9", {"start": v(5057.33, 940.85) * mm, "end": v(4989.03, 998.25) * mm});
            skCircle(sketch, "E2.4.1.10", {"center": v(4858, 1247.14) * mm, "radius": 77.26 * mm, "construction": true});
            skPoint(sketch, "E2.4.1.11", {"position": v(4669.49, 1174.51) * mm});
            skPoint(sketch, "E2.4.1.12", {"position": v(5314.14, 956.07) * mm});
            skCircle(sketch, "E2.4.1.13", {"center": v(5502.66, 1028.7) * mm, "radius": 77.26 * mm, "construction": true});
            skLineSegment(sketch, "E2.4.1.14", {"start": v(4726.98, 1277.59) * mm, "end": v(4711.42, 1189.74) * mm});
            skCircle(sketch, "E2.4.1.15", {"center": v(5287.77, 1247.14) * mm, "radius": 77.26 * mm, "construction": true});
            skCircle(sketch, "E2.4.1.16", {"center": v(5502.66, 810.26) * mm, "radius": 77.26 * mm, "construction": true});
            skLineSegment(sketch, "E2.4.1.17", {"start": v(5088.45, 1335) * mm, "end": v(5156.75, 1277.59) * mm});
            skLineSegment(sketch, "E2.4.1.18", {"start": v(4989.03, 779.81) * mm, "end": v(5004.59, 867.66) * mm});
            skLineSegment(sketch, "E2.4.1.19", {"start": v(4989.03, 998.25) * mm, "end": v(5004.59, 1086.1) * mm});
            skPoint(sketch, "E2.4.1.20", {"position": v(5314.14, 737.63) * mm});
            skPoint(sketch, "E2.4.1.21", {"position": v(4669.49, 956.07) * mm});
            skPoint(sketch, "E2.4.1.22", {"position": v(5099.26, 737.63) * mm});
            skPoint(sketch, "E2.4.1.23", {"position": v(5529.03, 1174.51) * mm});
            skLineSegment(sketch, "E2.4.1.24", {"start": v(5004.59, 1304.54) * mm, "end": v(5088.45, 1335) * mm});
            skLineSegment(sketch, "E2.4.1.25", {"start": v(5057.33, 722.4) * mm, "end": v(4989.03, 779.81) * mm});
            skCircle(sketch, "E2.4.1.26", {"center": v(4858, 1028.7) * mm, "radius": 77.26 * mm, "construction": true});
            skCircle(sketch, "E2.4.1.27", {"center": v(4858, 810.26) * mm, "radius": 77.26 * mm, "construction": true});
            skLineSegment(sketch, "E2.4.1.28", {"start": v(5156.75, 1277.59) * mm, "end": v(5141.19, 1189.74) * mm});
            skLineSegment(sketch, "E2.4.1.29", {"start": v(5004.59, 1086.1) * mm, "end": v(5088.45, 1116.55) * mm});
            skLineSegment(sketch, "E2.4.1.30", {"start": v(5004.59, 867.66) * mm, "end": v(5088.45, 898.11) * mm});
            skLineSegment(sketch, "E2.4.1.31", {"start": v(4842.44, 940.85) * mm, "end": v(4774.14, 998.25) * mm});
            skLineSegment(sketch, "E2.4.1.32", {"start": v(5418.8, 998.25) * mm, "end": v(5434.36, 1086.1) * mm});
            skPoint(sketch, "E2.4.1.33", {"position": v(4884.37, 737.63) * mm});
            skPoint(sketch, "E2.4.1.34", {"position": v(5314.14, 1174.51) * mm});
            skLineSegment(sketch, "E2.4.1.35", {"start": v(5272.21, 1159.29) * mm, "end": v(5203.91, 1216.7) * mm});
            skCircle(sketch, "E2.4.1.36", {"center": v(5287.77, 1028.7) * mm, "radius": 77.26 * mm, "construction": true});
            skCircle(sketch, "E2.4.1.37", {"center": v(5287.77, 810.26) * mm, "radius": 77.26 * mm, "construction": true});
            skLineSegment(sketch, "E2.4.1.38", {"start": v(5088.45, 898.11) * mm, "end": v(5156.75, 840.7) * mm});
            skLineSegment(sketch, "E2.4.1.39", {"start": v(5434.36, 1304.54) * mm, "end": v(5518.22, 1335) * mm});
            skLineSegment(sketch, "E2.4.1.40", {"start": v(5434.36, 1086.1) * mm, "end": v(5518.22, 1116.55) * mm});
            skLineSegment(sketch, "E2.4.1.41", {"start": v(4726.98, 1059.15) * mm, "end": v(4711.42, 971.3) * mm});
            skCircle(sketch, "E2.4.1.42", {"center": v(4643.12, 1247.14) * mm, "radius": 77.26 * mm, "construction": true});
            skCircle(sketch, "E2.4.1.43", {"center": v(4643.12, 810.26) * mm, "radius": 77.26 * mm, "construction": true});
            skLineSegment(sketch, "E2.4.1.44", {"start": v(4627.56, 722.4) * mm, "end": v(4559.26, 779.81) * mm});
            skLineSegment(sketch, "E2.4.1.45", {"start": v(4574.82, 867.66) * mm, "end": v(4658.68, 898.11) * mm});
            skCircle(sketch, "E2.4.1.46", {"center": v(4643.12, 1028.7) * mm, "radius": 77.26 * mm, "construction": true});
            skLineSegment(sketch, "E2.4.1.47", {"start": v(4627.56, 940.85) * mm, "end": v(4559.26, 998.25) * mm});
            skLineSegment(sketch, "E2.4.1.48", {"start": v(4559.26, 998.25) * mm, "end": v(4574.82, 1086.1) * mm});
            skLineSegment(sketch, "E2.4.1.49", {"start": v(4574.82, 1086.1) * mm, "end": v(4658.68, 1116.55) * mm});
            skLineSegment(sketch, "E2.4.1.50", {"start": v(4658.68, 1116.55) * mm, "end": v(4726.98, 1059.15) * mm});
            skPoint(sketch, "E2.4.1.51", {"position": v(5099.26, 956.07) * mm});
            skLineSegment(sketch, "E2.4.1.52", {"start": v(5156.75, 1059.15) * mm, "end": v(5141.19, 971.3) * mm});
            skLineSegment(sketch, "E2.4.1.53", {"start": v(4789.7, 1304.54) * mm, "end": v(4873.56, 1335) * mm});
            skLineSegment(sketch, "E2.4.1.54", {"start": v(5518.22, 1335) * mm, "end": v(5586.52, 1277.59) * mm});
            skLineSegment(sketch, "E2.4.1.55", {"start": v(4627.56, 1159.29) * mm, "end": v(4559.26, 1216.7) * mm});
            skLineSegment(sketch, "E2.4.1.56", {"start": v(5156.75, 840.7) * mm, "end": v(5141.19, 752.86) * mm});
            skCircle(sketch, "E2.4.1.57", {"center": v(5072.89, 1247.14) * mm, "radius": 77.26 * mm, "construction": true});
            skLineSegment(sketch, "E2.4.1.58", {"start": v(5586.52, 1277.59) * mm, "end": v(5570.96, 1189.74) * mm});
            skLineSegment(sketch, "E2.4.1.59", {"start": v(5272.21, 940.85) * mm, "end": v(5203.91, 998.25) * mm});
            skPoint(sketch, "E2.4.1.60", {"position": v(4884.37, 956.07) * mm});
            skPoint(sketch, "E2.4.1.61", {"position": v(5529.03, 737.63) * mm});
            skLineSegment(sketch, "E2.4.1.62", {"start": v(5219.47, 1304.54) * mm, "end": v(5303.33, 1335) * mm});
            skCircle(sketch, "E2.4.1.63", {"center": v(5072.89, 1028.7) * mm, "radius": 77.26 * mm, "construction": true});
            skLineSegment(sketch, "E2.4.1.64", {"start": v(5586.52, 1059.15) * mm, "end": v(5570.96, 971.3) * mm});
            skLineSegment(sketch, "E2.4.1.65", {"start": v(4789.7, 867.66) * mm, "end": v(4873.56, 898.11) * mm});
            skLineSegment(sketch, "E2.4.1.66", {"start": v(4559.26, 779.81) * mm, "end": v(4774.14, 779.81) * mm, "construction": true});
            skLineSegment(sketch, "E2.4.1.67", {"start": v(5518.22, 898.11) * mm, "end": v(5586.52, 840.7) * mm});
            skLineSegment(sketch, "E2.4.1.68", {"start": v(4574.82, 1304.54) * mm, "end": v(4658.68, 1335) * mm});
            skLineSegment(sketch, "E2.4.1.69", {"start": v(5303.33, 1335) * mm, "end": v(5371.63, 1277.59) * mm});
            skCircle(sketch, "E2.4.1.70", {"center": v(5502.66, 1247.14) * mm, "radius": 77.26 * mm, "construction": true});
            skPoint(sketch, "E2.4.1.71", {"position": v(5099.26, 1174.51) * mm});
            skPoint(sketch, "E2.4.1.72", {"position": v(4669.49, 737.63) * mm});
            skLineSegment(sketch, "E2.4.1.73", {"start": v(5219.47, 1086.1) * mm, "end": v(5303.33, 1116.55) * mm});
            skLineSegment(sketch, "E2.4.1.74", {"start": v(5371.63, 1277.59) * mm, "end": v(5356.07, 1189.74) * mm});
            skLineSegment(sketch, "E2.4.1.75", {"start": v(5570.96, 1189.74) * mm, "end": v(5487.1, 1159.29) * mm});
            skLineSegment(sketch, "E2.4.1.76", {"start": v(4989.03, 1216.7) * mm, "end": v(5004.59, 1304.54) * mm});
            skLineSegment(sketch, "E2.4.1.77", {"start": v(5141.19, 752.86) * mm, "end": v(5057.33, 722.4) * mm});
            skLineSegment(sketch, "E2.4.1.78", {"start": v(4941.86, 840.7) * mm, "end": v(4926.3, 752.86) * mm});
            skLineSegment(sketch, "E2.4.1.79", {"start": v(5303.33, 1116.55) * mm, "end": v(5371.63, 1059.15) * mm});
            skLineSegment(sketch, "E2.4.1.80", {"start": v(5303.33, 898.11) * mm, "end": v(5371.63, 840.7) * mm});
            skLineSegment(sketch, "E2.4.1.81", {"start": v(4926.3, 1189.74) * mm, "end": v(4842.44, 1159.29) * mm});
            skLineSegment(sketch, "E2.4.1.82", {"start": v(4926.3, 971.3) * mm, "end": v(4842.44, 940.85) * mm});
            skLineSegment(sketch, "E2.4.1.83", {"start": v(5487.1, 1159.29) * mm, "end": v(5418.8, 1216.7) * mm});
            skLineSegment(sketch, "E2.4.1.84", {"start": v(5487.1, 940.85) * mm, "end": v(5418.8, 998.25) * mm});
            skLineSegment(sketch, "E2.4.1.85", {"start": v(5570.96, 971.3) * mm, "end": v(5487.1, 940.85) * mm});
            skLineSegment(sketch, "E2.4.1.86", {"start": v(5371.63, 1059.15) * mm, "end": v(5356.07, 971.3) * mm});
            skLineSegment(sketch, "E2.4.1.87", {"start": v(5356.07, 1189.74) * mm, "end": v(5272.21, 1159.29) * mm});
            skLineSegment(sketch, "E2.4.1.88", {"start": v(5570.96, 752.86) * mm, "end": v(5487.1, 722.4) * mm});
            skLineSegment(sketch, "E2.4.1.89", {"start": v(5371.63, 840.7) * mm, "end": v(5356.07, 752.86) * mm});
            skLineSegment(sketch, "E2.4.1.90", {"start": v(4842.44, 1159.29) * mm, "end": v(4774.14, 1216.7) * mm});
            skLineSegment(sketch, "E2.4.1.91", {"start": v(5418.8, 1216.7) * mm, "end": v(5434.36, 1304.54) * mm});
            skLineSegment(sketch, "E2.4.1.92", {"start": v(4926.3, 752.86) * mm, "end": v(4842.44, 722.4) * mm});
            skLineSegment(sketch, "E2.4.1.93", {"start": v(5487.1, 722.4) * mm, "end": v(5418.8, 779.81) * mm});
            skLineSegment(sketch, "E2.4.1.94", {"start": v(5088.45, 1116.55) * mm, "end": v(5156.75, 1059.15) * mm});
            skLineSegment(sketch, "E2.4.1.95", {"start": v(4774.14, 1216.7) * mm, "end": v(4789.7, 1304.54) * mm});
            skLineSegment(sketch, "E2.4.1.96", {"start": v(4774.14, 998.25) * mm, "end": v(4789.7, 1086.1) * mm});
            skLineSegment(sketch, "E2.4.1.97", {"start": v(4711.42, 1189.74) * mm, "end": v(4627.56, 1159.29) * mm});
            skLineSegment(sketch, "E2.4.1.98", {"start": v(4711.42, 752.86) * mm, "end": v(4627.56, 722.4) * mm});
            skLineSegment(sketch, "E2.4.1.99", {"start": v(4559.26, 779.81) * mm, "end": v(4574.82, 867.66) * mm});
            skLineSegment(sketch, "E2.4.1.100", {"start": v(4658.68, 898.11) * mm, "end": v(4726.98, 840.7) * mm});
            skLineSegment(sketch, "E2.4.1.101", {"start": v(4726.98, 840.7) * mm, "end": v(4711.42, 752.86) * mm});
            skLineSegment(sketch, "E2.4.1.102", {"start": v(4711.42, 971.3) * mm, "end": v(4627.56, 940.85) * mm});
            skLineSegment(sketch, "E2.4.1.103", {"start": v(5518.22, 1116.55) * mm, "end": v(5586.52, 1059.15) * mm});
            skLineSegment(sketch, "E2.4.1.104", {"start": v(4842.44, 722.4) * mm, "end": v(4774.14, 779.81) * mm});
            skLineSegment(sketch, "E2.4.1.105", {"start": v(5418.8, 779.81) * mm, "end": v(5434.36, 867.66) * mm});
            skLineSegment(sketch, "E2.4.1.106", {"start": v(5356.07, 971.3) * mm, "end": v(5272.21, 940.85) * mm});
            skLineSegment(sketch, "E2.4.1.107", {"start": v(5203.91, 1216.7) * mm, "end": v(5219.47, 1304.54) * mm});
            skLineSegment(sketch, "E2.4.1.108", {"start": v(5356.07, 752.86) * mm, "end": v(5272.21, 722.4) * mm});
            skLineSegment(sketch, "E2.4.1.109", {"start": v(4789.7, 1086.1) * mm, "end": v(4873.56, 1116.55) * mm});
            skLineSegment(sketch, "E2.4.1.110", {"start": v(4873.56, 1335) * mm, "end": v(4941.86, 1277.59) * mm});
            skLineSegment(sketch, "E2.4.1.111", {"start": v(4774.14, 779.81) * mm, "end": v(4789.7, 867.66) * mm});
            skLineSegment(sketch, "E2.4.1.112", {"start": v(5434.36, 867.66) * mm, "end": v(5518.22, 898.11) * mm});
            skLineSegment(sketch, "E2.4.1.113", {"start": v(4559.26, 1216.7) * mm, "end": v(4574.82, 1304.54) * mm});
            skLineSegment(sketch, "E2.4.1.114", {"start": v(5272.21, 722.4) * mm, "end": v(5203.91, 779.81) * mm});
            skLineSegment(sketch, "E2.4.1.115", {"start": v(4873.56, 1116.55) * mm, "end": v(4941.86, 1059.15) * mm});
            skLineSegment(sketch, "E2.4.1.116", {"start": v(5141.19, 1189.74) * mm, "end": v(5057.33, 1159.29) * mm});
            skLineSegment(sketch, "E2.4.1.117", {"start": v(4941.86, 1277.59) * mm, "end": v(4926.3, 1189.74) * mm});
            skLineSegment(sketch, "E2.4.1.118", {"start": v(5203.91, 998.25) * mm, "end": v(5219.47, 1086.1) * mm});
            skLineSegment(sketch, "E2.4.1.119", {"start": v(5203.91, 779.81) * mm, "end": v(5219.47, 867.66) * mm});
            skLineSegment(sketch, "E2.4.1.120", {"start": v(5141.19, 971.3) * mm, "end": v(5057.33, 940.85) * mm});
            skLineSegment(sketch, "E2.4.1.121", {"start": v(4941.86, 1059.15) * mm, "end": v(4926.3, 971.3) * mm});
            skLineSegment(sketch, "E2.4.2.0", {"start": v(5586.52, 1650.97) * mm, "end": v(5570.96, 1563.12) * mm});
            skLineSegment(sketch, "E2.4.2.1", {"start": v(4559.26, 1590.07) * mm, "end": v(4559.26, 1808.51) * mm, "construction": true});
            skLineSegment(sketch, "E2.4.2.2", {"start": v(4873.56, 1708.37) * mm, "end": v(4941.86, 1650.97) * mm});
            skCircle(sketch, "E2.4.2.3", {"center": v(5072.89, 1620.52) * mm, "radius": 77.26 * mm, "construction": true});
            skLineSegment(sketch, "E2.4.2.4", {"start": v(5057.33, 1969.55) * mm, "end": v(4989.03, 2026.95) * mm});
            skPoint(sketch, "E2.4.2.5", {"position": v(5529.03, 1766.33) * mm});
            skPoint(sketch, "E2.4.2.6", {"position": v(4884.37, 1984.77) * mm});
            skLineSegment(sketch, "E2.4.2.7", {"start": v(4658.68, 2145.25) * mm, "end": v(4726.98, 2087.85) * mm});
            skLineSegment(sketch, "E2.4.2.8", {"start": v(5219.47, 1677.92) * mm, "end": v(5303.33, 1708.37) * mm});
            skLineSegment(sketch, "E2.4.2.9", {"start": v(5057.33, 1751.1) * mm, "end": v(4989.03, 1808.51) * mm});
            skCircle(sketch, "E2.4.2.10", {"center": v(4858, 2057.4) * mm, "radius": 77.26 * mm, "construction": true});
            skPoint(sketch, "E2.4.2.11", {"position": v(4669.49, 1984.77) * mm});
            skPoint(sketch, "E2.4.2.12", {"position": v(5314.14, 1766.33) * mm});
            skCircle(sketch, "E2.4.2.13", {"center": v(5502.66, 1838.96) * mm, "radius": 77.26 * mm, "construction": true});
            skLineSegment(sketch, "E2.4.2.14", {"start": v(4726.98, 2087.85) * mm, "end": v(4711.42, 2000) * mm});
            skCircle(sketch, "E2.4.2.15", {"center": v(5287.77, 2057.4) * mm, "radius": 77.26 * mm, "construction": true});
            skCircle(sketch, "E2.4.2.16", {"center": v(5502.66, 1620.52) * mm, "radius": 77.26 * mm, "construction": true});
            skLineSegment(sketch, "E2.4.2.17", {"start": v(5088.45, 2145.25) * mm, "end": v(5156.75, 2087.85) * mm});
            skLineSegment(sketch, "E2.4.2.18", {"start": v(4989.03, 1590.07) * mm, "end": v(5004.59, 1677.92) * mm});
            skLineSegment(sketch, "E2.4.2.19", {"start": v(4989.03, 1808.51) * mm, "end": v(5004.59, 1896.36) * mm});
            skPoint(sketch, "E2.4.2.20", {"position": v(5314.14, 1547.9) * mm});
            skPoint(sketch, "E2.4.2.21", {"position": v(4669.49, 1766.33) * mm});
            skPoint(sketch, "E2.4.2.22", {"position": v(5099.26, 1547.9) * mm});
            skPoint(sketch, "E2.4.2.23", {"position": v(5529.03, 1984.77) * mm});
            skLineSegment(sketch, "E2.4.2.24", {"start": v(5004.59, 2114.8) * mm, "end": v(5088.45, 2145.25) * mm});
            skLineSegment(sketch, "E2.4.2.25", {"start": v(5057.33, 1532.67) * mm, "end": v(4989.03, 1590.07) * mm});
            skCircle(sketch, "E2.4.2.26", {"center": v(4858, 1838.96) * mm, "radius": 77.26 * mm, "construction": true});
            skCircle(sketch, "E2.4.2.27", {"center": v(4858, 1620.52) * mm, "radius": 77.26 * mm, "construction": true});
            skLineSegment(sketch, "E2.4.2.28", {"start": v(5156.75, 2087.85) * mm, "end": v(5141.19, 2000) * mm});
            skLineSegment(sketch, "E2.4.2.29", {"start": v(5004.59, 1896.36) * mm, "end": v(5088.45, 1926.81) * mm});
            skLineSegment(sketch, "E2.4.2.30", {"start": v(5004.59, 1677.92) * mm, "end": v(5088.45, 1708.37) * mm});
            skLineSegment(sketch, "E2.4.2.31", {"start": v(4842.44, 1751.1) * mm, "end": v(4774.14, 1808.51) * mm});
            skLineSegment(sketch, "E2.4.2.32", {"start": v(5418.8, 1808.51) * mm, "end": v(5434.36, 1896.36) * mm});
            skPoint(sketch, "E2.4.2.33", {"position": v(4884.37, 1547.9) * mm});
            skPoint(sketch, "E2.4.2.34", {"position": v(5314.14, 1984.77) * mm});
            skLineSegment(sketch, "E2.4.2.35", {"start": v(5272.21, 1969.55) * mm, "end": v(5203.91, 2026.95) * mm});
            skCircle(sketch, "E2.4.2.36", {"center": v(5287.77, 1838.96) * mm, "radius": 77.26 * mm, "construction": true});
            skCircle(sketch, "E2.4.2.37", {"center": v(5287.77, 1620.52) * mm, "radius": 77.26 * mm, "construction": true});
            skLineSegment(sketch, "E2.4.2.38", {"start": v(5088.45, 1708.37) * mm, "end": v(5156.75, 1650.97) * mm});
            skLineSegment(sketch, "E2.4.2.39", {"start": v(5434.36, 2114.8) * mm, "end": v(5518.22, 2145.25) * mm});
            skLineSegment(sketch, "E2.4.2.40", {"start": v(5434.36, 1896.36) * mm, "end": v(5518.22, 1926.81) * mm});
            skLineSegment(sketch, "E2.4.2.41", {"start": v(4726.98, 1869.4) * mm, "end": v(4711.42, 1781.56) * mm});
            skCircle(sketch, "E2.4.2.42", {"center": v(4643.12, 2057.4) * mm, "radius": 77.26 * mm, "construction": true});
            skCircle(sketch, "E2.4.2.43", {"center": v(4643.12, 1620.52) * mm, "radius": 77.26 * mm, "construction": true});
            skLineSegment(sketch, "E2.4.2.44", {"start": v(4627.56, 1532.67) * mm, "end": v(4559.26, 1590.07) * mm});
            skLineSegment(sketch, "E2.4.2.45", {"start": v(4574.82, 1677.92) * mm, "end": v(4658.68, 1708.37) * mm});
            skCircle(sketch, "E2.4.2.46", {"center": v(4643.12, 1838.96) * mm, "radius": 77.26 * mm, "construction": true});
            skLineSegment(sketch, "E2.4.2.47", {"start": v(4627.56, 1751.1) * mm, "end": v(4559.26, 1808.51) * mm});
            skLineSegment(sketch, "E2.4.2.48", {"start": v(4559.26, 1808.51) * mm, "end": v(4574.82, 1896.36) * mm});
            skLineSegment(sketch, "E2.4.2.49", {"start": v(4574.82, 1896.36) * mm, "end": v(4658.68, 1926.81) * mm});
            skLineSegment(sketch, "E2.4.2.50", {"start": v(4658.68, 1926.81) * mm, "end": v(4726.98, 1869.4) * mm});
            skPoint(sketch, "E2.4.2.51", {"position": v(5099.26, 1766.33) * mm});
            skLineSegment(sketch, "E2.4.2.52", {"start": v(5156.75, 1869.4) * mm, "end": v(5141.19, 1781.56) * mm});
            skLineSegment(sketch, "E2.4.2.53", {"start": v(4789.7, 2114.8) * mm, "end": v(4873.56, 2145.25) * mm});
            skLineSegment(sketch, "E2.4.2.54", {"start": v(5518.22, 2145.25) * mm, "end": v(5586.52, 2087.85) * mm});
            skLineSegment(sketch, "E2.4.2.55", {"start": v(4627.56, 1969.55) * mm, "end": v(4559.26, 2026.95) * mm});
            skLineSegment(sketch, "E2.4.2.56", {"start": v(5156.75, 1650.97) * mm, "end": v(5141.19, 1563.12) * mm});
            skCircle(sketch, "E2.4.2.57", {"center": v(5072.89, 2057.4) * mm, "radius": 77.26 * mm, "construction": true});
            skLineSegment(sketch, "E2.4.2.58", {"start": v(5586.52, 2087.85) * mm, "end": v(5570.96, 2000) * mm});
            skLineSegment(sketch, "E2.4.2.59", {"start": v(5272.21, 1751.1) * mm, "end": v(5203.91, 1808.51) * mm});
            skPoint(sketch, "E2.4.2.60", {"position": v(4884.37, 1766.33) * mm});
            skPoint(sketch, "E2.4.2.61", {"position": v(5529.03, 1547.9) * mm});
            skLineSegment(sketch, "E2.4.2.62", {"start": v(5219.47, 2114.8) * mm, "end": v(5303.33, 2145.25) * mm});
            skCircle(sketch, "E2.4.2.63", {"center": v(5072.89, 1838.96) * mm, "radius": 77.26 * mm, "construction": true});
            skLineSegment(sketch, "E2.4.2.64", {"start": v(5586.52, 1869.4) * mm, "end": v(5570.96, 1781.56) * mm});
            skLineSegment(sketch, "E2.4.2.65", {"start": v(4789.7, 1677.92) * mm, "end": v(4873.56, 1708.37) * mm});
            skLineSegment(sketch, "E2.4.2.66", {"start": v(4559.26, 1590.07) * mm, "end": v(4774.14, 1590.07) * mm, "construction": true});
            skLineSegment(sketch, "E2.4.2.67", {"start": v(5518.22, 1708.37) * mm, "end": v(5586.52, 1650.97) * mm});
            skLineSegment(sketch, "E2.4.2.68", {"start": v(4574.82, 2114.8) * mm, "end": v(4658.68, 2145.25) * mm});
            skLineSegment(sketch, "E2.4.2.69", {"start": v(5303.33, 2145.25) * mm, "end": v(5371.63, 2087.85) * mm});
            skCircle(sketch, "E2.4.2.70", {"center": v(5502.66, 2057.4) * mm, "radius": 77.26 * mm, "construction": true});
            skPoint(sketch, "E2.4.2.71", {"position": v(5099.26, 1984.77) * mm});
            skPoint(sketch, "E2.4.2.72", {"position": v(4669.49, 1547.9) * mm});
            skLineSegment(sketch, "E2.4.2.73", {"start": v(5219.47, 1896.36) * mm, "end": v(5303.33, 1926.81) * mm});
            skLineSegment(sketch, "E2.4.2.74", {"start": v(5371.63, 2087.85) * mm, "end": v(5356.07, 2000) * mm});
            skLineSegment(sketch, "E2.4.2.75", {"start": v(5570.96, 2000) * mm, "end": v(5487.1, 1969.55) * mm});
            skLineSegment(sketch, "E2.4.2.76", {"start": v(4989.03, 2026.95) * mm, "end": v(5004.59, 2114.8) * mm});
            skLineSegment(sketch, "E2.4.2.77", {"start": v(5141.19, 1563.12) * mm, "end": v(5057.33, 1532.67) * mm});
            skLineSegment(sketch, "E2.4.2.78", {"start": v(4941.86, 1650.97) * mm, "end": v(4926.3, 1563.12) * mm});
            skLineSegment(sketch, "E2.4.2.79", {"start": v(5303.33, 1926.81) * mm, "end": v(5371.63, 1869.4) * mm});
            skLineSegment(sketch, "E2.4.2.80", {"start": v(5303.33, 1708.37) * mm, "end": v(5371.63, 1650.97) * mm});
            skLineSegment(sketch, "E2.4.2.81", {"start": v(4926.3, 2000) * mm, "end": v(4842.44, 1969.55) * mm});
            skLineSegment(sketch, "E2.4.2.82", {"start": v(4926.3, 1781.56) * mm, "end": v(4842.44, 1751.1) * mm});
            skLineSegment(sketch, "E2.4.2.83", {"start": v(5487.1, 1969.55) * mm, "end": v(5418.8, 2026.95) * mm});
            skLineSegment(sketch, "E2.4.2.84", {"start": v(5487.1, 1751.1) * mm, "end": v(5418.8, 1808.51) * mm});
            skLineSegment(sketch, "E2.4.2.85", {"start": v(5570.96, 1781.56) * mm, "end": v(5487.1, 1751.1) * mm});
            skLineSegment(sketch, "E2.4.2.86", {"start": v(5371.63, 1869.4) * mm, "end": v(5356.07, 1781.56) * mm});
            skLineSegment(sketch, "E2.4.2.87", {"start": v(5356.07, 2000) * mm, "end": v(5272.21, 1969.55) * mm});
            skLineSegment(sketch, "E2.4.2.88", {"start": v(5570.96, 1563.12) * mm, "end": v(5487.1, 1532.67) * mm});
            skLineSegment(sketch, "E2.4.2.89", {"start": v(5371.63, 1650.97) * mm, "end": v(5356.07, 1563.12) * mm});
            skLineSegment(sketch, "E2.4.2.90", {"start": v(4842.44, 1969.55) * mm, "end": v(4774.14, 2026.95) * mm});
            skLineSegment(sketch, "E2.4.2.91", {"start": v(5418.8, 2026.95) * mm, "end": v(5434.36, 2114.8) * mm});
            skLineSegment(sketch, "E2.4.2.92", {"start": v(4926.3, 1563.12) * mm, "end": v(4842.44, 1532.67) * mm});
            skLineSegment(sketch, "E2.4.2.93", {"start": v(5487.1, 1532.67) * mm, "end": v(5418.8, 1590.07) * mm});
            skLineSegment(sketch, "E2.4.2.94", {"start": v(5088.45, 1926.81) * mm, "end": v(5156.75, 1869.4) * mm});
            skLineSegment(sketch, "E2.4.2.95", {"start": v(4774.14, 2026.95) * mm, "end": v(4789.7, 2114.8) * mm});
            skLineSegment(sketch, "E2.4.2.96", {"start": v(4774.14, 1808.51) * mm, "end": v(4789.7, 1896.36) * mm});
            skLineSegment(sketch, "E2.4.2.97", {"start": v(4711.42, 2000) * mm, "end": v(4627.56, 1969.55) * mm});
            skLineSegment(sketch, "E2.4.2.98", {"start": v(4711.42, 1563.12) * mm, "end": v(4627.56, 1532.67) * mm});
            skLineSegment(sketch, "E2.4.2.99", {"start": v(4559.26, 1590.07) * mm, "end": v(4574.82, 1677.92) * mm});
            skLineSegment(sketch, "E2.4.2.100", {"start": v(4658.68, 1708.37) * mm, "end": v(4726.98, 1650.97) * mm});
            skLineSegment(sketch, "E2.4.2.101", {"start": v(4726.98, 1650.97) * mm, "end": v(4711.42, 1563.12) * mm});
            skLineSegment(sketch, "E2.4.2.102", {"start": v(4711.42, 1781.56) * mm, "end": v(4627.56, 1751.1) * mm});
            skLineSegment(sketch, "E2.4.2.103", {"start": v(5518.22, 1926.81) * mm, "end": v(5586.52, 1869.4) * mm});
            skLineSegment(sketch, "E2.4.2.104", {"start": v(4842.44, 1532.67) * mm, "end": v(4774.14, 1590.07) * mm});
            skLineSegment(sketch, "E2.4.2.105", {"start": v(5418.8, 1590.07) * mm, "end": v(5434.36, 1677.92) * mm});
            skLineSegment(sketch, "E2.4.2.106", {"start": v(5356.07, 1781.56) * mm, "end": v(5272.21, 1751.1) * mm});
            skLineSegment(sketch, "E2.4.2.107", {"start": v(5203.91, 2026.95) * mm, "end": v(5219.47, 2114.8) * mm});
            skLineSegment(sketch, "E2.4.2.108", {"start": v(5356.07, 1563.12) * mm, "end": v(5272.21, 1532.67) * mm});
            skLineSegment(sketch, "E2.4.2.109", {"start": v(4789.7, 1896.36) * mm, "end": v(4873.56, 1926.81) * mm});
            skLineSegment(sketch, "E2.4.2.110", {"start": v(4873.56, 2145.25) * mm, "end": v(4941.86, 2087.85) * mm});
            skLineSegment(sketch, "E2.4.2.111", {"start": v(4774.14, 1590.07) * mm, "end": v(4789.7, 1677.92) * mm});
            skLineSegment(sketch, "E2.4.2.112", {"start": v(5434.36, 1677.92) * mm, "end": v(5518.22, 1708.37) * mm});
            skLineSegment(sketch, "E2.4.2.113", {"start": v(4559.26, 2026.95) * mm, "end": v(4574.82, 2114.8) * mm});
            skLineSegment(sketch, "E2.4.2.114", {"start": v(5272.21, 1532.67) * mm, "end": v(5203.91, 1590.07) * mm});
            skLineSegment(sketch, "E2.4.2.115", {"start": v(4873.56, 1926.81) * mm, "end": v(4941.86, 1869.4) * mm});
            skLineSegment(sketch, "E2.4.2.116", {"start": v(5141.19, 2000) * mm, "end": v(5057.33, 1969.55) * mm});
            skLineSegment(sketch, "E2.4.2.117", {"start": v(4941.86, 2087.85) * mm, "end": v(4926.3, 2000) * mm});
            skLineSegment(sketch, "E2.4.2.118", {"start": v(5203.91, 1808.51) * mm, "end": v(5219.47, 1896.36) * mm});
            skLineSegment(sketch, "E2.4.2.119", {"start": v(5203.91, 1590.07) * mm, "end": v(5219.47, 1677.92) * mm});
            skLineSegment(sketch, "E2.4.2.120", {"start": v(5141.19, 1781.56) * mm, "end": v(5057.33, 1751.1) * mm});
            skLineSegment(sketch, "E2.4.2.121", {"start": v(4941.86, 1869.4) * mm, "end": v(4926.3, 1781.56) * mm});
            skLineSegment(sketch, "E2.direction1", {"start": v(-83.86, -30.45) * mm, "end": v(1076.92, -30.45) * mm, "construction": true});
            skLineSegment(sketch, "E2.direction2", {"start": v(-83.86, -30.45) * mm, "end": v(-83.86, 779.81) * mm, "construction": true});
            skSolve(sketch);
        }
        {
            var Q0;
            Q0 = qSketchRegion(id + "F0", true);
            extrude(context, id + "F1", {"entities" : qUnion([Q0]), "depth" : 381 * mm, "offsetDistance" : 25.4 * mm});
        }
    });
